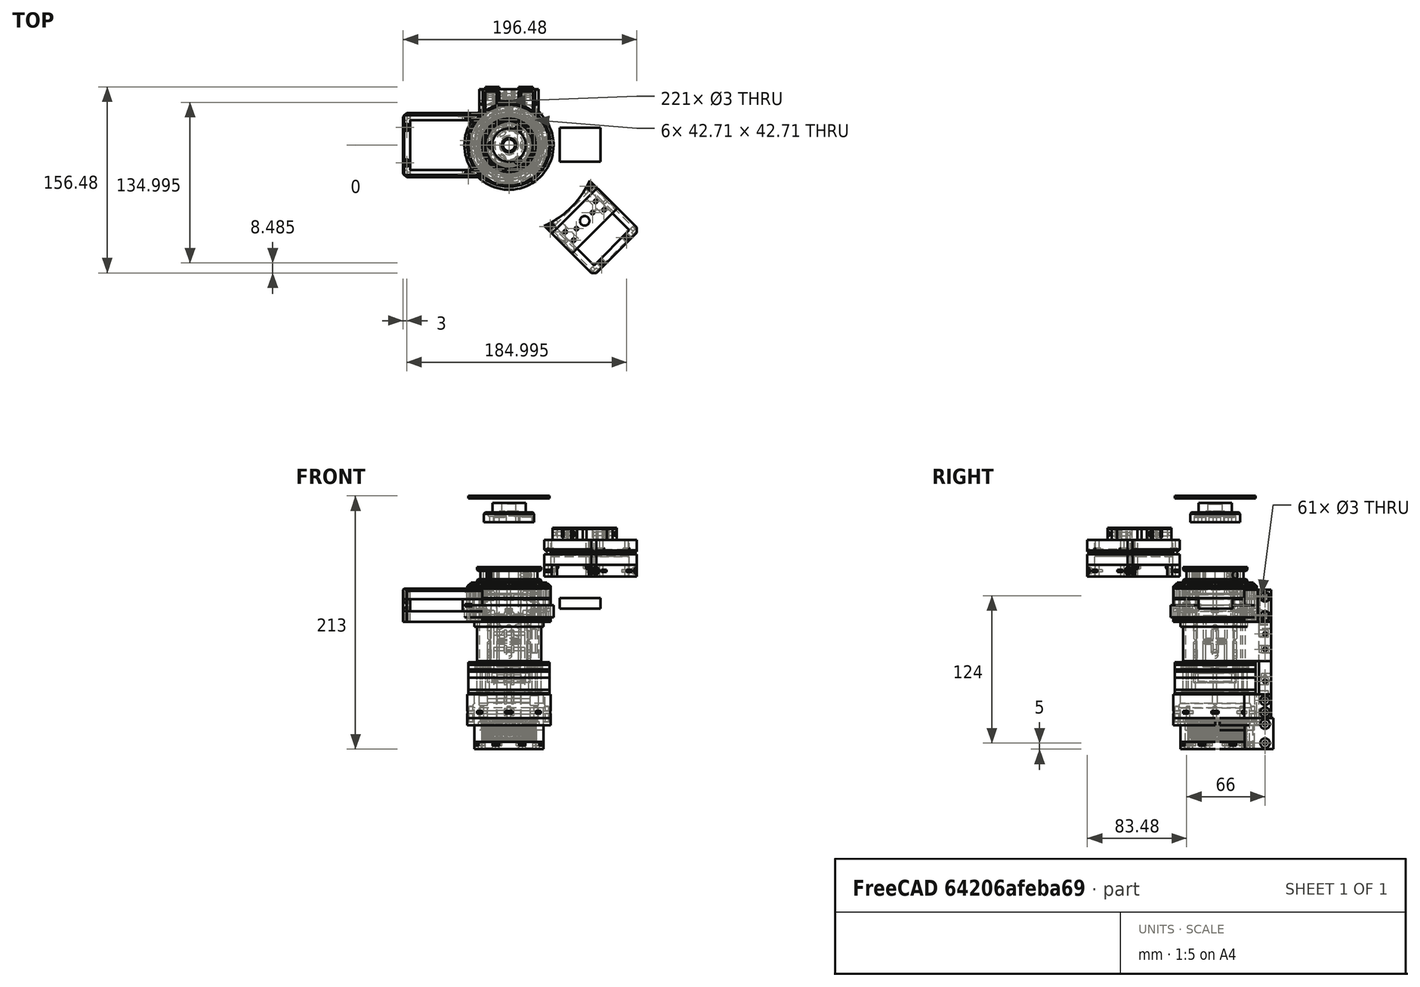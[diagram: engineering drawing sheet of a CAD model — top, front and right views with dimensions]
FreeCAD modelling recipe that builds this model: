
FCSTD DOCUMENT  (FreeCAD 0.19R24276 (Git))
Label: G-midi_rotators_066
License: All rights reserved
LicenseURL: http://en.wikipedia.org/wiki/All_rights_reserved
objects: Part::Cylinder×403, Part::Box×196, Part::Cut×177, Part::Compound×164, Part::FeaturePython×42, Part::Chamfer×41, Mesh::Feature×25, Part::Torus×3
note: 1026 computed .brp shape members not serialized (recipe doc carries the construction recipe); baked Part::Feature solids carry a one-line shape summary decoded from their .brp

FEATURE [Part::Box] Box313  label="Krychle313"
  AttacherType = Attacher::AttachEngine3D
  Height = 7
  Length = 1.4
  Placement = pos=(0,0,-22) rot=(0,0,1;0.099484rad)
  Width = 60
FEATURE [Part::Box] Box314  label="Krychle314"
  AttacherType = Attacher::AttachEngine3D
  Height = 7
  Length = 1.4
  Placement = pos=(0,0,-22) rot=(0,0,-1;0.05236rad)
  Width = 60
FEATURE [Part::FeaturePython] Tube084  # WARN: FeaturePython — macro-defined, semantics opaque (R4)
  AttacherType = Attacher::AttachEngine3D
  Height = 7
  InnerRadius = 20
  OuterRadius = 21.4
  Placement = pos=(0,0,-22) rot=(0,0,1;0rad)
FEATURE [Part::FeaturePython] Tube085  # WARN: FeaturePython — macro-defined, semantics opaque (R4)
  AttacherType = Attacher::AttachEngine3D
  Height = 7
  InnerRadius = 20
  OuterRadius = 21.4
  Placement = pos=(0,0,-22) rot=(0,0,1;0rad)
FEATURE [Part::Box] Box307  label="Krychle307"
  AttacherType = Attacher::AttachEngine3D
  Height = 7
  Length = 60
  Placement = pos=(0,0,-22) rot=(0,0,-1;0.349066rad)
  Width = 60
FEATURE [Part::Box] Box308  label="Krychle308"
  AttacherType = Attacher::AttachEngine3D
  Height = 7
  Length = 60
  Placement = pos=(-56.3816,-20.5212,-22) rot=(0,0,1;0.349066rad)
  Width = 60
FEATURE [Part::Compound] Compound718
  Links = -> [Box307,Box308]
FEATURE [Part::Box] Box309  label="Krychle309"
  AttacherType = Attacher::AttachEngine3D
  Height = 7
  Length = 120
  Placement = pos=(-60,-60,-22) rot=(0,0,-1;0rad)
  Width = 60
FEATURE [Part::Cut] Cut334
  Base = -> Tube085
  Tool = -> Box309
FEATURE [Part::Box] Box310  label="Krychle310"
  AttacherType = Attacher::AttachEngine3D
  Height = 7
  Length = 120
  Placement = pos=(-60,-60,-22) rot=(0,0,-1;0rad)
  Width = 60
FEATURE [Part::Cut] Cut337
  Base = -> Tube084
  Tool = -> Box310
FEATURE [Part::Box] Box311  label="Krychle311"
  AttacherType = Attacher::AttachEngine3D
  Height = 7
  Length = 60
  Placement = pos=(-59.9909,-1.04714,-22) rot=(0,0,1;0.017453rad)
  Width = 60
FEATURE [Part::Box] Box312  label="Krychle312"
  AttacherType = Attacher::AttachEngine3D
  Height = 7
  Length = 60
  Placement = pos=(0,0,-22) rot=(0,0,-1;0.034907rad)
  Width = 60
FEATURE [Part::Compound] Compound719
  Links = -> [Box312,Box311]
FEATURE [Part::Cylinder] Cylinder805  label="Válec805"
  Angle = 360
  AttacherType = Attacher::AttachEngine3D
  Height = 3
  Placement = pos=(0,0,-25) rot=(0,0,1;0rad)
  Radius = 27
FEATURE [Part::Chamfer] Chamfer
  Base = -> Cylinder805
  Edges = 1 edges r=1: [Edge1]
FEATURE [Part::Box] Box315  label="Krychle315"
  AttacherType = Attacher::AttachEngine3D
  Height = 100
  Length = 30.2
  Placement = pos=(0,-21.3546,-30) rot=(0,0,1;0.785398rad)
  Width = 30.2
FEATURE [Part::Cut] Cut340
  Base = -> Chamfer
  Tool = -> Box315
FEATURE [Part::Cylinder] Cylinder806  label="Válec806"
  Angle = 360
  AttacherType = Attacher::AttachEngine3D
  Height = 3
  Placement = pos=(0,0,-15) rot=(0,0,1;0rad)
  Radius = 27
FEATURE [Part::Box] Box316  label="Krychle316"
  AttacherType = Attacher::AttachEngine3D
  Height = 100
  Length = 30.2
  Placement = pos=(0,-21.3546,-30) rot=(0,0,1;0.785398rad)
  Width = 30.2
FEATURE [Part::Cut] Cut341
  Base = -> Cylinder806
  Tool = -> Box316
FEATURE [Part::Chamfer] Chamfer001
  Base = -> Cut341
  Edges = 1 edges r=1: [Edge3]
FEATURE [Part::Box] Box317  label="Krychle317"
  AttacherType = Attacher::AttachEngine3D
  Height = 20
  Length = 6
  Placement = pos=(18,-3,-30) rot=(0,0,1;0rad)
  Width = 6
FEATURE [Part::Cylinder] Cylinder807  label="Válec807"
  Angle = 360
  AttacherType = Attacher::AttachEngine3D
  Height = 20
  Placement = pos=(21,0,-30) rot=(0,0,1;0rad)
  Radius = 1.5
FEATURE [Part::Box] Box318  label="Krychle318"
  AttacherType = Attacher::AttachEngine3D
  Height = 20
  Length = 6
  Placement = pos=(9.89949,-14.1421,-30) rot=(0,0,-1;0.785398rad)
  Width = 6
FEATURE [Part::Cylinder] Cylinder808  label="Válec808"
  Angle = 360
  AttacherType = Attacher::AttachEngine3D
  Height = 20
  Placement = pos=(14.1421,-14.1421,-30) rot=(0,0,-1;0.785398rad)
  Radius = 1.5
FEATURE [Part::Box] Box319  label="Krychle319"
  AttacherType = Attacher::AttachEngine3D
  Height = 20
  Length = 6
  Placement = pos=(-9.89949,14.1421,-30) rot=(0,0,1;2.35619rad)
  Width = 6
FEATURE [Part::Cylinder] Cylinder809  label="Válec809"
  Angle = 360
  AttacherType = Attacher::AttachEngine3D
  Height = 20
  Placement = pos=(-14.1421,14.1421,-30) rot=(0,0,1;2.35619rad)
  Radius = 1.5
FEATURE [Part::Compound] Compound
  Links = -> [Cylinder808,Cylinder809]
FEATURE [Part::Cut] Cut342
  Base = -> Cut340
  Tool = -> Compound
FEATURE [Part::Compound] Compound722
  Links = -> [Box319,Box318]
  Placement = pos=(0,0,-13) rot=(0,0,1;0rad)
FEATURE [Part::Cut] Cut344
  Base = -> Cut342
  Tool = -> Compound722
FEATURE [Part::Cylinder] Cylinder812  label="Válec812"
  Angle = 360
  AttacherType = Attacher::AttachEngine3D
  Height = 3
  Placement = pos=(-14.1421,14.1421,-30) rot=(0,0,1;2.35619rad)
  Radius = 3
FEATURE [Part::Cylinder] Cylinder813  label="Válec813"
  Angle = 360
  AttacherType = Attacher::AttachEngine3D
  Height = 3
  Placement = pos=(14.1421,-14.1421,-30) rot=(0,0,-1;0.785398rad)
  Radius = 3
FEATURE [Part::Compound] Compound723
  Links = -> [Cylinder813,Cylinder812]
  Placement = pos=(0,0,17) rot=(0,0,1;0rad)
FEATURE [Part::Cut] Cut345
  Base = -> Chamfer001
  Tool = -> Compound723
FEATURE [Part::Cylinder] Cylinder814  label="Válec814"
  Angle = 360
  AttacherType = Attacher::AttachEngine3D
  Height = 20
  Placement = pos=(-14.1421,14.1421,-30) rot=(0,0,1;2.35619rad)
  Radius = 1.5
FEATURE [Part::Cylinder] Cylinder815  label="Válec815"
  Angle = 360
  AttacherType = Attacher::AttachEngine3D
  Height = 20
  Placement = pos=(14.1421,-14.1421,-30) rot=(0,0,-1;0.785398rad)
  Radius = 1.5
FEATURE [Part::Compound] Compound724
  Links = -> [Cylinder815,Cylinder814]
FEATURE [Part::Cut] Cut346  label="G-midi_belt-wheel-front"
  Base = -> Cut345
  Placement = pos=(0,0,54) rot=(0,0,1;0rad)
  Tool = -> Compound724
FEATURE [Part::Box] Box320  label="Krychle320"
  AttacherType = Attacher::AttachEngine3D
  Height = 20
  Length = 30.2
  Placement = pos=(-15.1,-15.1,0) rot=(0,0,1;0rad)
  Width = 30.2
FEATURE [Part::Cylinder] Cylinder816  label="Válec816"
  Angle = 360
  AttacherType = Attacher::AttachEngine3D
  Height = 20
  Radius = 24.65
FEATURE [Part::Cut] Cut349
  Base = -> Cylinder816
  Tool = -> Box320
FEATURE [Part::Box] Box001  label="Krychle001"
  AttacherType = Attacher::AttachEngine3D
  Height = 20
  Length = 20
  Placement = pos=(-10,15.1,20) rot=(0,0,1;0rad)
  Width = 3
FEATURE [Part::Box] Box002  label="Krychle002"
  AttacherType = Attacher::AttachEngine3D
  Height = 20
  Length = 20
  Placement = pos=(-15.1,-10,20) rot=(0,0,1;1.5708rad)
  Width = 3
FEATURE [Part::Box] Box003  label="Krychle003"
  AttacherType = Attacher::AttachEngine3D
  Height = 20
  Length = 20
  Placement = pos=(10,-15.1,20) rot=(0,0,1;3.14159rad)
  Width = 3
FEATURE [Part::Box] Box004  label="Krychle004"
  AttacherType = Attacher::AttachEngine3D
  Height = 20
  Length = 20
  Placement = pos=(15.1,10,20) rot=(0,0,-1;1.5708rad)
  Width = 3
FEATURE [Part::Cylinder] Cylinder001  label="Válec001"
  Angle = 360
  AttacherType = Attacher::AttachEngine3D
  Height = 10
  Placement = pos=(0,-12,30) rot=(1,0,0;1.5708rad)
  Radius = 2.5
FEATURE [Part::Cylinder] Cylinder002  label="Válec002"
  Angle = 360
  AttacherType = Attacher::AttachEngine3D
  Height = 10
  Placement = pos=(12,6e-15,30) rot=(0.57735,0.57735,0.57735;2.0944rad)
  Radius = 2.5
FEATURE [Part::Cylinder] Cylinder003  label="Válec003"
  Angle = 360
  AttacherType = Attacher::AttachEngine3D
  Height = 10
  Placement = pos=(-1.5e-14,12,30) rot=(0,0.707107,0.707107;3.14159rad)
  Radius = 2.5
FEATURE [Part::Cylinder] Cylinder004  label="Válec004"
  Angle = 360
  AttacherType = Attacher::AttachEngine3D
  Height = 10
  Placement = pos=(-12,-2.4e-14,30) rot=(-0.57735,0.57735,0.57735;4.18879rad)
  Radius = 2.5
FEATURE [Part::Compound] Compound725
  Links = -> [Box001,Box002,Box003,Box004]
FEATURE [Part::Compound] Compound001
  Links = -> [Cylinder001,Cylinder002,Cylinder003,Cylinder004]
FEATURE [Part::Cut] Cut001
  Base = -> Compound725
  Tool = -> Compound001
FEATURE [Part::Chamfer] Chamfer002
  Base = -> Cut001
  Edges = 5 edges r=2: [Edge3,Edge12,Edge18,Edge27,Edge42]
FEATURE [Part::Chamfer] Chamfer003
  Base = -> Chamfer002
  Edges = 3 edges r=2: [Edge49,Edge63,Edge72]
FEATURE [Part::Chamfer] Chamfer004
  Base = -> Chamfer003
  Edges = 4 edges r=1: [Edge1,Edge29,Edge50,Edge71]
FEATURE [Part::Chamfer] Chamfer006
  Base = -> Cut349
  Edges = 2 edges r=0.5: [Edge9,Edge11]
FEATURE [Part::Chamfer] Chamfer005
  Base = -> Chamfer006
  Edges = 1 edges r=1: [Edge22]
FEATURE [Part::Chamfer] Chamfer007
  Base = -> Chamfer005
  Edges = 1 edges r=0.5: [Edge3]
FEATURE [Part::Compound] Compound002  label="G-midi_rotator-fix1"
  Links = -> [Chamfer004,Chamfer007,Chamfer003]
FEATURE [Part::Box] Box671  label="Krychle671"
  AttacherType = Attacher::AttachEngine3D
  Height = 50
  Length = 42
  Placement = pos=(-21.0011,60.0051,31) rot=(0,0,1;0rad)
  Width = 62
FEATURE [Part::Compound] Compound846
  Links = -> [Box671]
  Placement = pos=(0,0,1) rot=(0,0,1;3.92699rad)
FEATURE [Part::Box] Box672  label="Krychle672"
  AttacherType = Attacher::AttachEngine3D
  Height = 9
  Length = 54
  Placement = pos=(-27.0044,59.998,75) rot=(0,0,1;0rad)
  Width = 68
FEATURE [Part::Cylinder] Cylinder1708  label="Válec1708"
  Angle = 360
  AttacherType = Attacher::AttachEngine3D
  Height = 40
  Placement = pos=(0,0,44) rot=(0,0,1;0rad)
  Radius = 74
FEATURE [Part::Box] Box673  label="Krychle673"
  AttacherType = Attacher::AttachEngine3D
  Height = 10
  Length = 54
  Placement = pos=(-27.0044,59.998,75) rot=(0,0,1;0rad)
  Width = 68
FEATURE [Part::Box] Box674  label="Krychle674"
  AttacherType = Attacher::AttachEngine3D
  Height = 10
  Length = 56
  Placement = pos=(-28,78,75) rot=(0,0,1;0rad)
  Width = 44
FEATURE [Part::Compound] Compound847
  Links = -> [Box672]
  Placement = pos=(0,0,0) rot=(0,0,1;3.92699rad)
FEATURE [Part::Cut] Cut489
  Base = -> Compound847
  Tool = -> Compound846
FEATURE [Part::Cut] Cut490
  Base = -> Cut489
  Tool = -> Cylinder1708
FEATURE [Part::Compound] Compound848
  Links = -> [Box673]
  Placement = pos=(0,0,-10) rot=(0,0,1;3.92699rad)
FEATURE [Part::Compound] Compound849
  Links = -> [Box674]
  Placement = pos=(0,0,-10) rot=(0,0,1;3.92699rad)
FEATURE [Part::Cut] Cut491
  Base = -> Compound848
  Tool = -> Compound849
FEATURE [Part::Chamfer] Chamfer053
  Base = -> Cut490
  Edges = 2 edges r=3: [Edge2,Edge9]
FEATURE [Part::Box] Box675  label="Krychle675"
  AttacherType = Attacher::AttachEngine3D
  Height = 50
  Length = 42
  Placement = pos=(-21.0011,60.0051,31) rot=(0,0,1;0rad)
  Width = 62
FEATURE [Part::Compound] Compound850
  Links = -> [Box675]
  Placement = pos=(0,0,0) rot=(0,0,1;3.92699rad)
FEATURE [Part::Cut] Cut492
  Base = -> Cut491
  Tool = -> Compound850
FEATURE [Part::Cylinder] Cylinder1709  label="Válec1709"
  Angle = 360
  AttacherType = Attacher::AttachEngine3D
  Height = 40
  Placement = pos=(0,0,44) rot=(0,0,1;0rad)
  Radius = 74
FEATURE [Part::Cut] Cut493
  Base = -> Cut492
  Tool = -> Cylinder1709
FEATURE [Part::Chamfer] Chamfer052
  Base = -> Cut493
  Edges = 2 edges r=3: [Edge26,Edge37]
FEATURE [Part::Cylinder] Cylinder1710  label="Válec1710"
  Angle = 360
  AttacherType = Attacher::AttachEngine3D
  Height = 50
  Placement = pos=(-24,140,72) rot=(1,0,0;1.5708rad)
  Radius = 1.5
FEATURE [Part::Compound] Compound851
  Links = -> [Cylinder1710]
  Placement = pos=(0,0,0) rot=(0,0,1;3.92699rad)
FEATURE [Part::Cylinder] Cylinder1711  label="Válec1711"
  Angle = 360
  AttacherType = Attacher::AttachEngine3D
  Height = 50
  Placement = pos=(24,140,72) rot=(1,0,0;1.5708rad)
  Radius = 1.5
FEATURE [Part::Compound] Compound852
  Links = -> [Cylinder1711]
  Placement = pos=(0,0,0) rot=(0,0,1;3.92699rad)
FEATURE [Part::Compound] Compound853
  Links = -> [Compound851,Compound852]
  Placement = pos=(0,0,-2) rot=(0,0,1;0rad)
FEATURE [Part::Cylinder] Cylinder1712  label="Válec1712"
  Angle = 360
  AttacherType = Attacher::AttachEngine3D
  Height = 3
  Placement = pos=(-24,128,72) rot=(1,0,0;1.5708rad)
  Radius = 3
FEATURE [Part::Compound] Compound854
  Links = -> [Cylinder1712]
  Placement = pos=(0,0,0) rot=(0,0,1;3.92699rad)
FEATURE [Part::Cylinder] Cylinder1713  label="Válec1713"
  Angle = 360
  AttacherType = Attacher::AttachEngine3D
  Height = 3
  Placement = pos=(24,128,72) rot=(1,0,0;1.5708rad)
  Radius = 3
FEATURE [Part::Compound] Compound855
  Links = -> [Cylinder1713]
  Placement = pos=(0,0,0) rot=(0,0,1;3.92699rad)
FEATURE [Part::Compound] Compound856
  Links = -> [Compound854,Compound855]
  Placement = pos=(0,0,-2) rot=(0,0,1;0rad)
FEATURE [Part::Box] Box680  label="Krychle680"
  AttacherType = Attacher::AttachEngine3D
  Height = 2
  Length = 6
  Placement = pos=(21,70,-48) rot=(0,0,1;0rad)
  Width = 6
FEATURE [Part::Box] Box681  label="Krychle681"
  AttacherType = Attacher::AttachEngine3D
  Height = 2
  Length = 7
  Placement = pos=(-28,70,-48) rot=(0,0,1;0rad)
  Width = 6
FEATURE [Part::Box] Box682  label="Krychle682"
  AttacherType = Attacher::AttachEngine3D
  Height = 2
  Length = 6
  Placement = pos=(-18,122,-48) rot=(0,0,1;0rad)
  Width = 6
FEATURE [Part::Box] Box683  label="Krychle683"
  AttacherType = Attacher::AttachEngine3D
  Height = 2
  Length = 6
  Placement = pos=(12,122,-48) rot=(0,0,1;0rad)
  Width = 6
FEATURE [Part::Cylinder] Cylinder1718  label="Válec1718"
  Angle = 360
  AttacherType = Attacher::AttachEngine3D
  Height = 60
  Placement = pos=(-15,125,-80) rot=(0,0,1;0rad)
  Radius = 1.5
FEATURE [Part::Cylinder] Cylinder1719  label="Válec1719"
  Angle = 360
  AttacherType = Attacher::AttachEngine3D
  Height = 60
  Placement = pos=(15,125,-80) rot=(0,0,1;0rad)
  Radius = 1.5
FEATURE [Part::Cylinder] Cylinder1720  label="Válec1720"
  Angle = 360
  AttacherType = Attacher::AttachEngine3D
  Height = 60
  Placement = pos=(24,73,-80) rot=(0,0,1;0rad)
  Radius = 1.5
FEATURE [Part::Cylinder] Cylinder1721  label="Válec1721"
  Angle = 360
  AttacherType = Attacher::AttachEngine3D
  Height = 60
  Placement = pos=(-24,73,-80) rot=(0,0,1;0rad)
  Radius = 1.5
FEATURE [Part::Cut] Cut494
  Base = -> Chamfer052
  Tool = -> Compound856
FEATURE [Part::Cut] Cut495
  Base = -> Cut494
  Tool = -> Compound853
FEATURE [Part::Compound] Compound859
  Links = -> [Box681,Box682,Box680,Box683]
  Placement = pos=(0,0,117) rot=(0,0,1;3.92699rad)
FEATURE [Part::Cut] Cut496
  Base = -> Cut495
  Tool = -> Compound859
FEATURE [Part::Compound] Compound860
  Links = -> [Cylinder1720,Cylinder1721,Cylinder1718,Cylinder1719]
  Placement = pos=(0,0,100) rot=(0,0,1;3.92699rad)
FEATURE [Part::Cut] Cut497
  Base = -> Cut496
  Tool = -> Compound860
FEATURE [Part::Box] Box685  label="Krychle685"
  AttacherType = Attacher::AttachEngine3D
  Height = 18
  Length = 42
  Placement = pos=(-21,-23,22) rot=(0,0,1;0rad)
  Width = 8
FEATURE [Part::Compound] Compound862
  Links = -> [Box685]
  Placement = pos=(63.64,-63.64,43) rot=(0,0,1;3.92699rad)
FEATURE [Part::Cylinder] Cylinder1724  label="Válec1724"
  Angle = 360
  AttacherType = Attacher::AttachEngine3D
  Height = 40
  Placement = pos=(0,0,44) rot=(0,0,1;0rad)
  Radius = 74
FEATURE [Part::Cylinder] Cylinder1725  label="Válec1725"
  Angle = 360
  AttacherType = Attacher::AttachEngine3D
  Height = 50
  Placement = pos=(-18,100,72) rot=(1,0,0;1.5708rad)
  Radius = 1.5
FEATURE [Part::Cylinder] Cylinder1726  label="Válec1726"
  Angle = 360
  AttacherType = Attacher::AttachEngine3D
  Height = 50
  Placement = pos=(18,100,72) rot=(1,0,0;1.5708rad)
  Radius = 1.5
FEATURE [Part::Cut] Cut498
  Base = -> Compound862
  Tool = -> Cylinder1724
FEATURE [Part::Compound] Compound868
  Links = -> [Cylinder1726]
  Placement = pos=(0,0,0) rot=(0,0,1;3.92699rad)
FEATURE [Part::Compound] Compound869
  Links = -> [Cylinder1725]
  Placement = pos=(0,0,0) rot=(0,0,1;3.92699rad)
FEATURE [Part::Compound] Compound867
  Links = -> [Compound869,Compound868]
  Placement = pos=(0,0,1) rot=(0,0,1;0rad)
FEATURE [Part::Cut] Cut499
  Base = -> Cut498
  Tool = -> Compound867
FEATURE [Part::Compound] Compound870  label="Base_encoder-lowhold"
  Links = -> [Cut497,Chamfer053,Cut499]
  Placement = pos=(0,0,-31) rot=(0,0,1;0rad)
FEATURE [Part::FeaturePython] Tube011  # WARN: FeaturePython — macro-defined, semantics opaque (R4)
  AttacherType = Attacher::AttachEngine3D
  Height = 10
  InnerRadius = 26
  OuterRadius = 32
FEATURE [Part::Cylinder] Cylinder195  label="Válec195"
  Angle = 360
  AttacherType = Attacher::AttachEngine3D
  Height = 30
  Placement = pos=(29,4e-15,0) rot=(0,0,1;1.5708rad)
  Radius = 1.5
FEATURE [Part::Cylinder] Cylinder196  label="Válec196"
  Angle = 360
  AttacherType = Attacher::AttachEngine3D
  Height = 30
  Placement = pos=(0,-29,0) rot=(0,0,1;0rad)
  Radius = 1.5
FEATURE [Part::Cylinder] Cylinder197  label="Válec197"
  Angle = 360
  AttacherType = Attacher::AttachEngine3D
  Height = 30
  Placement = pos=(20.5061,20.5061,0) rot=(0,0,1;2.35619rad)
  Radius = 1.5
FEATURE [Part::FeaturePython] Tube014  # WARN: FeaturePython — macro-defined, semantics opaque (R4)
  AttacherType = Attacher::AttachEngine3D
  Height = 3
  InnerRadius = 23
  OuterRadius = 32
  Placement = pos=(0,0,-3) rot=(0,0,1;0rad)
FEATURE [Part::Cylinder] Cylinder198  label="Válec198"
  Angle = 360
  AttacherType = Attacher::AttachEngine3D
  Height = 30
  Placement = pos=(20.5061,-20.5061,0) rot=(0,0,1;0.785398rad)
  Radius = 1.5
FEATURE [Part::Cylinder] Cylinder199  label="Válec199"
  Angle = 360
  AttacherType = Attacher::AttachEngine3D
  Height = 30
  Placement = pos=(-1.1e-14,29,0) rot=(0,0,1;3.14159rad)
  Radius = 1.5
FEATURE [Part::Cylinder] Cylinder200  label="Válec200"
  Angle = 360
  AttacherType = Attacher::AttachEngine3D
  Height = 30
  Placement = pos=(-20.5061,20.5061,0) rot=(0,0,1;3.92699rad)
  Radius = 1.5
FEATURE [Part::Cylinder] Cylinder201  label="Válec201"
  Angle = 360
  AttacherType = Attacher::AttachEngine3D
  Height = 30
  Placement = pos=(-29,-1.1e-14,0) rot=(0,0,-1;1.5708rad)
  Radius = 1.5
FEATURE [Part::Cylinder] Cylinder202  label="Válec202"
  Angle = 360
  AttacherType = Attacher::AttachEngine3D
  Height = 30
  Placement = pos=(-20.5061,-20.5061,0) rot=(0,0,-1;0.785398rad)
  Radius = 1.5
FEATURE [Part::Compound] Compound545
  Links = -> [Cylinder196,Cylinder198,Cylinder195,Cylinder197,Cylinder199,Cylinder200,Cylinder201,Cylinder202]
FEATURE [Part::Cut] Cut319
  Base = -> Tube011
  Tool = -> Compound545
FEATURE [Part::Box] Box084  label="Krychle084"
  AttacherType = Attacher::AttachEngine3D
  Height = 2
  Length = 6
  Placement = pos=(-3,-32,4) rot=(0,0,1;0rad)
  Width = 6
FEATURE [Part::Box] Box085  label="Krychle085"
  AttacherType = Attacher::AttachEngine3D
  Height = 2
  Length = 6
  Placement = pos=(20.5061,-24.7487,4) rot=(0,0,1;0.785398rad)
  Width = 6
FEATURE [Part::Box] Box086  label="Krychle086"
  AttacherType = Attacher::AttachEngine3D
  Height = 2
  Length = 6
  Placement = pos=(32,-3,4) rot=(0,0,1;1.5708rad)
  Width = 6
FEATURE [Part::Compound] Compound548
  Links = -> [Tube014,Cut319]
FEATURE [Part::Box] Box087  label="Krychle087"
  AttacherType = Attacher::AttachEngine3D
  Height = 2
  Length = 6
  Placement = pos=(24.7487,20.5061,4) rot=(0,0,1;2.35619rad)
  Width = 6
FEATURE [Part::Box] Box088  label="Krychle088"
  AttacherType = Attacher::AttachEngine3D
  Height = 2
  Length = 6
  Placement = pos=(3,32,4) rot=(0,0,1;3.14159rad)
  Width = 6
FEATURE [Part::Box] Box089  label="Krychle089"
  AttacherType = Attacher::AttachEngine3D
  Height = 2
  Length = 6
  Placement = pos=(-20.5061,24.7487,4) rot=(0,0,1;3.92699rad)
  Width = 6
FEATURE [Part::Box] Box090  label="Krychle090"
  AttacherType = Attacher::AttachEngine3D
  Height = 2
  Length = 6
  Placement = pos=(-32,3,4) rot=(0,0,-1;1.5708rad)
  Width = 6
FEATURE [Part::Box] Box091  label="Krychle091"
  AttacherType = Attacher::AttachEngine3D
  Height = 2
  Length = 6
  Placement = pos=(-24.7487,-20.5061,4) rot=(0,0,-1;0.785398rad)
  Width = 6
FEATURE [Part::Compound] Compound549
  Links = -> [Box084,Box085,Box086,Box087,Box088,Box089,Box090,Box091]
FEATURE [Part::Cut] Cut321
  Base = -> Compound548
  Tool = -> Compound549
FEATURE [Part::Box] Box093  label="Krychle093"
  AttacherType = Attacher::AttachEngine3D
  Height = 26
  Length = 40
  Placement = pos=(-20,15,-3) rot=(0,0,1;0rad)
  Width = 30
FEATURE [Part::Box] Box094  label="Krychle094"
  AttacherType = Attacher::AttachEngine3D
  Height = 26
  Length = 16
  Placement = pos=(-8,20,-3) rot=(0,0,1;0rad)
  Width = 25
FEATURE [Part::Cut] Cut322
  Base = -> Box093
  Tool = -> Box094
FEATURE [Part::Cylinder] Cylinder211  label="Válec211"
  Angle = 360
  AttacherType = Attacher::AttachEngine3D
  Height = 40
  Placement = pos=(0,0,-8) rot=(0,0,1;0rad)
  Radius = 32
FEATURE [Part::Cut] Cut323
  Base = -> Cut322
  Tool = -> Cylinder211
FEATURE [Part::Cylinder] Cylinder212  label="Válec212"
  Angle = 360
  AttacherType = Attacher::AttachEngine3D
  Height = 20
  Placement = pos=(-32,38,2) rot=(0,1,0;1.5708rad)
  Radius = 4
FEATURE [Part::Cylinder] Cylinder214  label="Válec214"
  Angle = 360
  AttacherType = Attacher::AttachEngine3D
  Height = 20
  Placement = pos=(-24,38,2) rot=(0,1,0;1.5708rad)
  Radius = 1.5
FEATURE [Part::Cylinder] Cylinder216  label="Válec216"
  Angle = 360
  AttacherType = Attacher::AttachEngine3D
  Height = 20
  Placement = pos=(-24,38,18) rot=(0,1,0;1.5708rad)
  Radius = 1.5
FEATURE [Part::Compound] Compound551
  Links = -> [Cylinder214,Cylinder216]
FEATURE [Part::Cut] Cut324
  Base = -> Cut323
  Tool = -> Compound551
FEATURE [Part::Cylinder] Cylinder217  label="Válec217"
  Angle = 360
  AttacherType = Attacher::AttachEngine3D
  Height = 20
  Placement = pos=(-32,38,18) rot=(0,1,0;1.5708rad)
  Radius = 4
FEATURE [Part::Compound] Compound550
  Links = -> [Cylinder217,Cylinder212]
FEATURE [Part::Cut] Cut325
  Base = -> Cut324
  Tool = -> Compound550
FEATURE [Part::Cylinder] Cylinder218  label="Válec218"
  Angle = 360
  AttacherType = Attacher::AttachEngine3D
  Height = 20
  Placement = pos=(12,38,18) rot=(0,1,0;1.5708rad)
  Radius = 4
FEATURE [Part::Cylinder] Cylinder219  label="Válec219"
  Angle = 360
  AttacherType = Attacher::AttachEngine3D
  Height = 20
  Placement = pos=(12,38,2) rot=(0,1,0;1.5708rad)
  Radius = 4
FEATURE [Part::Cylinder] Cylinder220  label="Válec220"
  Angle = 360
  AttacherType = Attacher::AttachEngine3D
  Height = 20
  Placement = pos=(4,38,2) rot=(0,1,0;1.5708rad)
  Radius = 1.5
FEATURE [Part::Cylinder] Cylinder221  label="Válec221"
  Angle = 360
  AttacherType = Attacher::AttachEngine3D
  Height = 20
  Placement = pos=(4,38,18) rot=(0,1,0;1.5708rad)
  Radius = 1.5
FEATURE [Part::Compound] Compound552
  Links = -> [Cylinder218,Cylinder219]
FEATURE [Part::Cut] Cut326
  Base = -> Cut325
  Tool = -> Compound552
FEATURE [Part::Compound] Compound553
  Links = -> [Cylinder220,Cylinder221]
FEATURE [Part::Cut] Cut327
  Base = -> Cut326
  Tool = -> Compound553
FEATURE [Part::Compound] Compound572  label="adapto_midi_lozohold"
  Links = -> [Cut327,Cut321]
FEATURE [Part::Box] Box686  label="Krychle686"
  AttacherType = Attacher::AttachEngine3D
  Height = 10
  Length = 54
  Placement = pos=(-27.0044,59.998,75) rot=(0,0,1;0rad)
  Width = 68
FEATURE [Part::Box] Box688  label="Krychle688"
  AttacherType = Attacher::AttachEngine3D
  Height = 50
  Length = 42
  Placement = pos=(-21,58,38) rot=(0,0,1;0rad)
  Width = 64
FEATURE [Part::Cut] Cut500
  Base = -> Box686
  Tool = -> Box688
FEATURE [Part::Cylinder] Cylinder1727  label="Válec1727"
  Angle = 360
  AttacherType = Attacher::AttachEngine3D
  Height = 3
  Placement = pos=(-24,128,72) rot=(1,0,0;1.5708rad)
  Radius = 3
FEATURE [Part::Cylinder] Cylinder1728  label="Válec1728"
  Angle = 360
  AttacherType = Attacher::AttachEngine3D
  Height = 3
  Placement = pos=(24,128,72) rot=(1,0,0;1.5708rad)
  Radius = 3
FEATURE [Part::Compound] Compound871
  Links = -> [Cylinder1727,Cylinder1728]
  Placement = pos=(0,0,8) rot=(0,0,1;0rad)
FEATURE [Part::Box] Box689  label="Krychle689"
  AttacherType = Attacher::AttachEngine3D
  Height = 2
  Length = 7
  Placement = pos=(-28,70,-48) rot=(0,0,1;0rad)
  Width = 6
FEATURE [Part::Box] Box690  label="Krychle690"
  AttacherType = Attacher::AttachEngine3D
  Height = 2
  Length = 6
  Placement = pos=(-18,122,-48) rot=(0,0,1;0rad)
  Width = 6
FEATURE [Part::Box] Box691  label="Krychle691"
  AttacherType = Attacher::AttachEngine3D
  Height = 2
  Length = 6
  Placement = pos=(21,70,-48) rot=(0,0,1;0rad)
  Width = 6
FEATURE [Part::Box] Box692  label="Krychle692"
  AttacherType = Attacher::AttachEngine3D
  Height = 2
  Length = 6
  Placement = pos=(12,122,-48) rot=(0,0,1;0rad)
  Width = 6
FEATURE [Part::Compound] Compound872
  Links = -> [Box689,Box690,Box691,Box692]
  Placement = pos=(0,0,127) rot=(0,0,1;0rad)
FEATURE [Part::Cylinder] Cylinder1729  label="Válec1729"
  Angle = 360
  AttacherType = Attacher::AttachEngine3D
  Height = 50
  Placement = pos=(-24,140,72) rot=(1,0,0;1.5708rad)
  Radius = 1.5
FEATURE [Part::Cylinder] Cylinder1730  label="Válec1730"
  Angle = 360
  AttacherType = Attacher::AttachEngine3D
  Height = 50
  Placement = pos=(24,140,72) rot=(1,0,0;1.5708rad)
  Radius = 1.5
FEATURE [Part::Compound] Compound873
  Links = -> [Cylinder1729,Cylinder1730]
  Placement = pos=(0,0,8) rot=(0,0,1;0rad)
FEATURE [Part::Cylinder] Cylinder1731  label="Válec1731"
  Angle = 360
  AttacherType = Attacher::AttachEngine3D
  Height = 60
  Placement = pos=(24,73,-80) rot=(0,0,1;0rad)
  Radius = 1.5
FEATURE [Part::Cylinder] Cylinder1732  label="Válec1732"
  Angle = 360
  AttacherType = Attacher::AttachEngine3D
  Height = 60
  Placement = pos=(-24,73,-80) rot=(0,0,1;0rad)
  Radius = 1.5
FEATURE [Part::Cylinder] Cylinder1733  label="Válec1733"
  Angle = 360
  AttacherType = Attacher::AttachEngine3D
  Height = 60
  Placement = pos=(-15,125,-80) rot=(0,0,1;0rad)
  Radius = 1.5
FEATURE [Part::Cylinder] Cylinder1734  label="Válec1734"
  Angle = 360
  AttacherType = Attacher::AttachEngine3D
  Height = 60
  Placement = pos=(15,125,-80) rot=(0,0,1;0rad)
  Radius = 1.5
FEATURE [Part::Compound] Compound874
  Links = -> [Cylinder1731,Cylinder1732,Cylinder1733,Cylinder1734]
  Placement = pos=(0,0,120) rot=(0,0,1;0rad)
FEATURE [Part::Box] Box693  label="Krychle693"
  AttacherType = Attacher::AttachEngine3D
  Height = 10
  Length = 56
  Placement = pos=(-28,78,75) rot=(0,0,1;0rad)
  Width = 44
FEATURE [Part::Cut] Cut501
  Base = -> Cut500
  Tool = -> Box693
FEATURE [Part::Box] Box694  label="Krychle694"
  AttacherType = Attacher::AttachEngine3D
  Height = 9
  Length = 54
  Placement = pos=(-27.0044,59.998,75) rot=(0,0,1;0rad)
  Width = 68
FEATURE [Part::Box] Box695  label="Krychle695"
  AttacherType = Attacher::AttachEngine3D
  Height = 50
  Length = 42
  Placement = pos=(-21,58,40) rot=(0,0,1;0rad)
  Width = 64
FEATURE [Part::Cut] Cut502
  Base = -> Box694
  Placement = pos=(0,0,-9) rot=(0,0,1;0rad)
  Tool = -> Box695
FEATURE [Part::Cylinder] Cylinder1735  label="Válec1735"
  Angle = 360
  AttacherType = Attacher::AttachEngine3D
  Height = 60
  Placement = pos=(15,125,-80) rot=(0,0,1;0rad)
  Radius = 1.5
FEATURE [Part::Cylinder] Cylinder1736  label="Válec1736"
  Angle = 360
  AttacherType = Attacher::AttachEngine3D
  Height = 60
  Placement = pos=(24,73,-80) rot=(0,0,1;0rad)
  Radius = 1.5
FEATURE [Part::Cylinder] Cylinder1737  label="Válec1737"
  Angle = 360
  AttacherType = Attacher::AttachEngine3D
  Height = 60
  Placement = pos=(-24,73,-80) rot=(0,0,1;0rad)
  Radius = 1.5
FEATURE [Part::Cylinder] Cylinder1738  label="Válec1738"
  Angle = 360
  AttacherType = Attacher::AttachEngine3D
  Height = 60
  Placement = pos=(-15,125,-80) rot=(0,0,1;0rad)
  Radius = 1.5
FEATURE [Part::Compound] Compound875
  Links = -> [Cylinder1736,Cylinder1737,Cylinder1738,Cylinder1735]
  Placement = pos=(0,0,120) rot=(0,0,1;0rad)
FEATURE [Part::Cut] Cut503
  Base = -> Cut501
  Tool = -> Compound875
FEATURE [Part::Cut] Cut504
  Base = -> Cut503
  Tool = -> Compound872
FEATURE [Part::Chamfer] Chamfer054
  Base = -> Cut504
  Edges = 2 edges r=3: [Edge32,Edge43]
FEATURE [Part::Cut] Cut505
  Base = -> Chamfer054
  Tool = -> Compound871
FEATURE [Part::Cut] Cut506
  Base = -> Cut505
  Tool = -> Compound873
FEATURE [Part::Chamfer] Chamfer055
  Base = -> Cut502
  Edges = 2 edges r=3: [Edge3,Edge15]
FEATURE [Part::Cut] Cut507
  Base = -> Chamfer055
  Tool = -> Compound874
FEATURE [Part::Compound] Compound876
  Links = -> [Cut506,Cut507]
  Placement = pos=(-39,0,-69) rot=(0,0,-1;1.5708rad)
FEATURE [Part::Cylinder] Cylinder1739  label="Válec1739"
  Angle = 360
  AttacherType = Attacher::AttachEngine3D
  Height = 19
  Placement = pos=(0,0,-3) rot=(0,0,1;0rad)
  Radius = 35
FEATURE [Part::FeaturePython] Tube086  # WARN: FeaturePython — macro-defined, semantics opaque (R4)
  AttacherType = Attacher::AttachEngine3D
  Height = 16
  InnerRadius = 29.1
  OuterRadius = 35
FEATURE [Part::FeaturePython] Tube087  # WARN: FeaturePython — macro-defined, semantics opaque (R4)
  AttacherType = Attacher::AttachEngine3D
  Height = 10
  InnerRadius = 31.5
  OuterRadius = 37.5
FEATURE [Part::FeaturePython] Tube088  # WARN: FeaturePython — macro-defined, semantics opaque (R4)
  AttacherType = Attacher::AttachEngine3D
  Height = 3
  InnerRadius = 26
  OuterRadius = 35
  Placement = pos=(0,0,-3) rot=(0,0,1;0rad)
FEATURE [Part::Cylinder] Cylinder1740  label="Válec1740"
  Angle = 360
  AttacherType = Attacher::AttachEngine3D
  Height = 30
  Placement = pos=(0,-32,0) rot=(0,0,1;0rad)
  Radius = 1.5
FEATURE [Part::Box] Box696  label="Krychle696"
  AttacherType = Attacher::AttachEngine3D
  Height = 2
  Length = 6
  Placement = pos=(-3,-35,6) rot=(0,0,1;0rad)
  Width = 6
FEATURE [Part::Cylinder] Cylinder1741  label="Válec1741"
  Angle = 360
  AttacherType = Attacher::AttachEngine3D
  Height = 30
  Placement = pos=(22.6274,-22.6274,0) rot=(0,0,1;0.785398rad)
  Radius = 1.5
FEATURE [Part::Cylinder] Cylinder1742  label="Válec1742"
  Angle = 360
  AttacherType = Attacher::AttachEngine3D
  Height = 30
  Placement = pos=(32,0,0) rot=(0,0,1;1.5708rad)
  Radius = 1.5
FEATURE [Part::Cylinder] Cylinder1743  label="Válec1743"
  Angle = 360
  AttacherType = Attacher::AttachEngine3D
  Height = 30
  Placement = pos=(22.6274,22.6274,0) rot=(0,0,1;2.35619rad)
  Radius = 1.5
FEATURE [Part::Cylinder] Cylinder1744  label="Válec1744"
  Angle = 360
  AttacherType = Attacher::AttachEngine3D
  Height = 30
  Placement = pos=(-1e-14,32,0) rot=(0,0,1;3.14159rad)
  Radius = 1.5
FEATURE [Part::Cylinder] Cylinder1745  label="Válec1745"
  Angle = 360
  AttacherType = Attacher::AttachEngine3D
  Height = 30
  Placement = pos=(-22.6274,22.6274,0) rot=(0,0,1;3.92699rad)
  Radius = 1.5
FEATURE [Part::Cylinder] Cylinder1746  label="Válec1746"
  Angle = 360
  AttacherType = Attacher::AttachEngine3D
  Height = 30
  Placement = pos=(-32,-1.1e-14,0) rot=(0,0,-1;1.5708rad)
  Radius = 1.5
FEATURE [Part::Cylinder] Cylinder1747  label="Válec1747"
  Angle = 360
  AttacherType = Attacher::AttachEngine3D
  Height = 30
  Placement = pos=(-22.6274,-22.6274,0) rot=(0,0,-1;0.785398rad)
  Radius = 1.5
FEATURE [Part::Compound] Compound877
  Links = -> [Cylinder1740,Cylinder1741,Cylinder1742,Cylinder1743,Cylinder1744,Cylinder1745,Cylinder1746,Cylinder1747]
FEATURE [Part::Box] Box697  label="Krychle697"
  AttacherType = Attacher::AttachEngine3D
  Height = 2
  Length = 6
  Placement = pos=(22.6274,-26.8701,6) rot=(0,0,1;0.785398rad)
  Width = 6
FEATURE [Part::Box] Box698  label="Krychle698"
  AttacherType = Attacher::AttachEngine3D
  Height = 2
  Length = 6
  Placement = pos=(35,-3,6) rot=(0,0,1;1.5708rad)
  Width = 6
FEATURE [Part::Box] Box699  label="Krychle699"
  AttacherType = Attacher::AttachEngine3D
  Height = 2
  Length = 6
  Placement = pos=(26.8701,22.6274,6) rot=(0,0,1;2.35619rad)
  Width = 6
FEATURE [Part::Box] Box700  label="Krychle700"
  AttacherType = Attacher::AttachEngine3D
  Height = 2
  Length = 6
  Placement = pos=(3,35,6) rot=(0,0,1;3.14159rad)
  Width = 6
FEATURE [Part::Box] Box701  label="Krychle701"
  AttacherType = Attacher::AttachEngine3D
  Height = 2
  Length = 6
  Placement = pos=(-22.6274,26.8701,6) rot=(0,0,1;3.92699rad)
  Width = 6
FEATURE [Part::Box] Box702  label="Krychle702"
  AttacherType = Attacher::AttachEngine3D
  Height = 2
  Length = 6
  Placement = pos=(-35,3,6) rot=(0,0,-1;1.5708rad)
  Width = 6
FEATURE [Part::Box] Box703  label="Krychle703"
  AttacherType = Attacher::AttachEngine3D
  Height = 2
  Length = 6
  Placement = pos=(-26.8701,-22.6274,6) rot=(0,0,-1;0.785398rad)
  Width = 6
FEATURE [Part::Compound] Compound878
  Links = -> [Box696,Box697,Box703,Box702,Box701,Box700,Box699,Box698]
FEATURE [Part::FeaturePython] Tube013  # WARN: FeaturePython — macro-defined, semantics opaque (R4)
  AttacherType = Attacher::AttachEngine3D
  Height = 3
  InnerRadius = 23
  OuterRadius = 32
  Placement = pos=(0,0,20) rot=(0,0,1;0rad)
FEATURE [Part::FeaturePython] Tube012  # WARN: FeaturePython — macro-defined, semantics opaque (R4)
  AttacherType = Attacher::AttachEngine3D
  Height = 10
  InnerRadius = 26
  OuterRadius = 32
  Placement = pos=(0,0,10) rot=(0,0,1;0rad)
FEATURE [Part::Cylinder] Cylinder204  label="Válec204"
  Angle = 360
  AttacherType = Attacher::AttachEngine3D
  Height = 3
  Placement = pos=(0,-29,20) rot=(0,0,1;0rad)
  Radius = 3
FEATURE [Part::Cylinder] Cylinder189  label="Válec189"
  Angle = 360
  AttacherType = Attacher::AttachEngine3D
  Height = 30
  Placement = pos=(29,4e-15,0) rot=(0,0,1;1.5708rad)
  Radius = 1.5
FEATURE [Part::Cylinder] Cylinder187  label="Válec187"
  Angle = 360
  AttacherType = Attacher::AttachEngine3D
  Height = 30
  Placement = pos=(0,-29,0) rot=(0,0,1;0rad)
  Radius = 1.5
FEATURE [Part::Cylinder] Cylinder193  label="Válec193"
  Angle = 360
  AttacherType = Attacher::AttachEngine3D
  Height = 30
  Placement = pos=(-29,-1.1e-14,0) rot=(0,0,-1;1.5708rad)
  Radius = 1.5
FEATURE [Part::Cylinder] Cylinder188  label="Válec188"
  Angle = 360
  AttacherType = Attacher::AttachEngine3D
  Height = 30
  Placement = pos=(20.5061,-20.5061,0) rot=(0,0,1;0.785398rad)
  Radius = 1.5
FEATURE [Part::Cylinder] Cylinder191  label="Válec191"
  Angle = 360
  AttacherType = Attacher::AttachEngine3D
  Height = 30
  Placement = pos=(-1.1e-14,29,0) rot=(0,0,1;3.14159rad)
  Radius = 1.5
FEATURE [Part::Cylinder] Cylinder192  label="Válec192"
  Angle = 360
  AttacherType = Attacher::AttachEngine3D
  Height = 30
  Placement = pos=(-20.5061,20.5061,0) rot=(0,0,1;3.92699rad)
  Radius = 1.5
FEATURE [Part::Cylinder] Cylinder190  label="Válec190"
  Angle = 360
  AttacherType = Attacher::AttachEngine3D
  Height = 30
  Placement = pos=(20.5061,20.5061,0) rot=(0,0,1;2.35619rad)
  Radius = 1.5
FEATURE [Part::Cylinder] Cylinder194  label="Válec194"
  Angle = 360
  AttacherType = Attacher::AttachEngine3D
  Height = 30
  Placement = pos=(-20.5061,-20.5061,0) rot=(0,0,-1;0.785398rad)
  Radius = 1.5
FEATURE [Part::Compound] Compound544
  Links = -> [Cylinder187,Cylinder188,Cylinder189,Cylinder190,Cylinder191,Cylinder192,Cylinder193,Cylinder194]
FEATURE [Part::Cut] Cut318
  Base = -> Tube012
  Tool = -> Compound544
FEATURE [Part::Cylinder] Cylinder203  label="Válec203"
  Angle = 360
  AttacherType = Attacher::AttachEngine3D
  Height = 3
  Placement = pos=(29,4e-15,20) rot=(0,0,1;1.5708rad)
  Radius = 3
FEATURE [Part::Cylinder] Cylinder206  label="Válec206"
  Angle = 360
  AttacherType = Attacher::AttachEngine3D
  Height = 3
  Placement = pos=(20.51,-20.51,20) rot=(0,0,1;0.785398rad)
  Radius = 3
FEATURE [Part::Cylinder] Cylinder208  label="Válec208"
  Angle = 360
  AttacherType = Attacher::AttachEngine3D
  Height = 3
  Placement = pos=(-20.51,20.51,20) rot=(0,0,1;3.92699rad)
  Radius = 3
FEATURE [Part::Cylinder] Cylinder205  label="Válec205"
  Angle = 360
  AttacherType = Attacher::AttachEngine3D
  Height = 3
  Placement = pos=(20.51,20.51,20) rot=(0,0,1;2.35619rad)
  Radius = 3
FEATURE [Part::Cylinder] Cylinder210  label="Válec210"
  Angle = 360
  AttacherType = Attacher::AttachEngine3D
  Height = 3
  Placement = pos=(-20.51,-20.51,20) rot=(0,0,-1;0.785398rad)
  Radius = 3
FEATURE [Part::Cylinder] Cylinder209  label="Válec209"
  Angle = 360
  AttacherType = Attacher::AttachEngine3D
  Height = 3
  Placement = pos=(-29,0,20) rot=(0,0,-1;1.5708rad)
  Radius = 3
FEATURE [Part::Cylinder] Cylinder207  label="Válec207"
  Angle = 360
  AttacherType = Attacher::AttachEngine3D
  Height = 3
  Placement = pos=(0,29,20) rot=(0,0,1;3.14159rad)
  Radius = 3
FEATURE [Part::Compound] Compound546
  Links = -> [Cylinder204,Cylinder206,Cylinder203,Cylinder205,Cylinder207,Cylinder208,Cylinder209,Cylinder210]
FEATURE [Part::Cut] Cut320
  Base = -> Tube013
  Tool = -> Compound546
FEATURE [Part::Compound] Compound547  label="adapto_midi_lozofixo"
  Links = -> [Cut318,Cut320]
  Placement = pos=(0,0,6) rot=(0,0,1;0rad)
FEATURE [Part::FeaturePython] Tube089  # WARN: FeaturePython — macro-defined, semantics opaque (R4)
  AttacherType = Attacher::AttachEngine3D
  Height = 9
  InnerRadius = 29.1
  OuterRadius = 35
  Placement = pos=(0,0,16) rot=(0,0,1;0rad)
FEATURE [Part::Cylinder] Cylinder1748  label="Válec1748"
  Angle = 360
  AttacherType = Attacher::AttachEngine3D
  Height = 30
  Placement = pos=(-22.6274,22.6274,0) rot=(0,0,1;3.92699rad)
  Radius = 1.5
FEATURE [Part::Cylinder] Cylinder1749  label="Válec1749"
  Angle = 360
  AttacherType = Attacher::AttachEngine3D
  Height = 30
  Placement = pos=(-22.6274,-22.6274,0) rot=(0,0,-1;0.785398rad)
  Radius = 1.5
FEATURE [Part::Cylinder] Cylinder1750  label="Válec1750"
  Angle = 360
  AttacherType = Attacher::AttachEngine3D
  Height = 30
  Placement = pos=(-1e-14,32,0) rot=(0,0,1;3.14159rad)
  Radius = 1.5
FEATURE [Part::Cylinder] Cylinder1751  label="Válec1751"
  Angle = 360
  AttacherType = Attacher::AttachEngine3D
  Height = 30
  Placement = pos=(-32,-1.1e-14,0) rot=(0,0,-1;1.5708rad)
  Radius = 1.5
FEATURE [Part::Cylinder] Cylinder1752  label="Válec1752"
  Angle = 360
  AttacherType = Attacher::AttachEngine3D
  Height = 30
  Placement = pos=(22.6274,-22.6274,0) rot=(0,0,1;0.785398rad)
  Radius = 1.5
FEATURE [Part::Cylinder] Cylinder1753  label="Válec1753"
  Angle = 360
  AttacherType = Attacher::AttachEngine3D
  Height = 30
  Placement = pos=(32,0,0) rot=(0,0,1;1.5708rad)
  Radius = 1.5
FEATURE [Part::Cylinder] Cylinder1754  label="Válec1754"
  Angle = 360
  AttacherType = Attacher::AttachEngine3D
  Height = 30
  Placement = pos=(22.6274,22.6274,0) rot=(0,0,1;2.35619rad)
  Radius = 1.5
FEATURE [Part::Cylinder] Cylinder1755  label="Válec1755"
  Angle = 360
  AttacherType = Attacher::AttachEngine3D
  Height = 30
  Placement = pos=(0,-32,0) rot=(0,0,1;0rad)
  Radius = 1.5
FEATURE [Part::Compound] Compound879
  Links = -> [Cylinder1755,Cylinder1752,Cylinder1753,Cylinder1754,Cylinder1750,Cylinder1748,Cylinder1751,Cylinder1749]
FEATURE [Part::Cylinder] Cylinder1756  label="Válec1756"
  Angle = 360
  AttacherType = Attacher::AttachEngine3D
  Height = 3
  Placement = pos=(-22.6274,22.6274,0) rot=(0,0,1;3.92699rad)
  Radius = 3
FEATURE [Part::Cylinder] Cylinder1757  label="Válec1757"
  Angle = 360
  AttacherType = Attacher::AttachEngine3D
  Height = 3
  Placement = pos=(-22.6274,-22.6274,0) rot=(0,0,-1;0.785398rad)
  Radius = 3
FEATURE [Part::Cylinder] Cylinder1758  label="Válec1758"
  Angle = 360
  AttacherType = Attacher::AttachEngine3D
  Height = 3
  Placement = pos=(-1e-14,32,0) rot=(0,0,1;3.14159rad)
  Radius = 3
FEATURE [Part::Cylinder] Cylinder1759  label="Válec1759"
  Angle = 360
  AttacherType = Attacher::AttachEngine3D
  Height = 3
  Placement = pos=(-32,-1.1e-14,0) rot=(0,0,-1;1.5708rad)
  Radius = 3
FEATURE [Part::Cylinder] Cylinder1760  label="Válec1760"
  Angle = 360
  AttacherType = Attacher::AttachEngine3D
  Height = 3
  Placement = pos=(22.6274,-22.6274,0) rot=(0,0,1;0.785398rad)
  Radius = 3
FEATURE [Part::Cylinder] Cylinder1761  label="Válec1761"
  Angle = 360
  AttacherType = Attacher::AttachEngine3D
  Height = 3
  Placement = pos=(32,0,0) rot=(0,0,1;1.5708rad)
  Radius = 3
FEATURE [Part::Cylinder] Cylinder1762  label="Válec1762"
  Angle = 360
  AttacherType = Attacher::AttachEngine3D
  Height = 3
  Placement = pos=(22.6274,22.6274,0) rot=(0,0,1;2.35619rad)
  Radius = 3
FEATURE [Part::Cylinder] Cylinder1763  label="Válec1763"
  Angle = 360
  AttacherType = Attacher::AttachEngine3D
  Height = 3
  Placement = pos=(0,-32,0) rot=(0,0,1;0rad)
  Radius = 3
FEATURE [Part::Compound] Compound880
  Links = -> [Cylinder1763,Cylinder1760,Cylinder1761,Cylinder1762,Cylinder1758,Cylinder1756,Cylinder1759,Cylinder1757]
  Placement = pos=(0,0,27) rot=(0,0,1;0rad)
FEATURE [Part::FeaturePython] Tube090  # WARN: FeaturePython — macro-defined, semantics opaque (R4)
  AttacherType = Attacher::AttachEngine3D
  Height = 4
  InnerRadius = 26
  OuterRadius = 35
  Placement = pos=(0,0,25) rot=(0,0,1;0rad)
FEATURE [Part::Cut] Cut508
  Base = -> Tube089
  Tool = -> Compound879
FEATURE [Part::Cylinder] Cylinder1764  label="Válec1764"
  Angle = 360
  AttacherType = Attacher::AttachEngine3D
  Height = 30
  Placement = pos=(22.6274,22.6274,0) rot=(0,0,1;2.35619rad)
  Radius = 1.5
FEATURE [Part::Cylinder] Cylinder1765  label="Válec1765"
  Angle = 360
  AttacherType = Attacher::AttachEngine3D
  Height = 30
  Placement = pos=(-22.6274,22.6274,0) rot=(0,0,1;3.92699rad)
  Radius = 1.5
FEATURE [Part::Cylinder] Cylinder1766  label="Válec1766"
  Angle = 360
  AttacherType = Attacher::AttachEngine3D
  Height = 30
  Placement = pos=(-22.6274,-22.6274,0) rot=(0,0,-1;0.785398rad)
  Radius = 1.5
FEATURE [Part::Cylinder] Cylinder1767  label="Válec1767"
  Angle = 360
  AttacherType = Attacher::AttachEngine3D
  Height = 30
  Placement = pos=(-1e-14,32,0) rot=(0,0,1;3.14159rad)
  Radius = 1.5
FEATURE [Part::Cylinder] Cylinder1768  label="Válec1768"
  Angle = 360
  AttacherType = Attacher::AttachEngine3D
  Height = 30
  Placement = pos=(32,0,0) rot=(0,0,1;1.5708rad)
  Radius = 1.5
FEATURE [Part::Cylinder] Cylinder1769  label="Válec1769"
  Angle = 360
  AttacherType = Attacher::AttachEngine3D
  Height = 30
  Placement = pos=(-32,-1.1e-14,0) rot=(0,0,-1;1.5708rad)
  Radius = 1.5
FEATURE [Part::Cylinder] Cylinder1770  label="Válec1770"
  Angle = 360
  AttacherType = Attacher::AttachEngine3D
  Height = 30
  Placement = pos=(22.6274,-22.6274,0) rot=(0,0,1;0.785398rad)
  Radius = 1.5
FEATURE [Part::Cylinder] Cylinder1771  label="Válec1771"
  Angle = 360
  AttacherType = Attacher::AttachEngine3D
  Height = 30
  Placement = pos=(0,-32,0) rot=(0,0,1;0rad)
  Radius = 1.5
FEATURE [Part::Compound] Compound881
  Links = -> [Cylinder1771,Cylinder1770,Cylinder1768,Cylinder1764,Cylinder1767,Cylinder1765,Cylinder1769,Cylinder1766]
FEATURE [Part::Cut] Cut511
  Base = -> Tube086
  Tool = -> Compound881
FEATURE [Part::Cut] Cut512
  Base = -> Cut511
  Tool = -> Compound878
FEATURE [Part::Box] Box646  label="Krychle646"
  AttacherType = Attacher::AttachEngine3D
  Height = 9
  Length = 28.8
  Placement = pos=(-14.4,-14,34) rot=(0,0,1;0rad)
  Width = 34.4
FEATURE [Part::Box] Box651  label="Krychle651"
  AttacherType = Attacher::AttachEngine3D
  Height = 9
  Length = 42
  Placement = pos=(-21,-12,34) rot=(0,0,1;0rad)
  Width = 24
FEATURE [Part::Box] Box653  label="Krychle653"
  AttacherType = Attacher::AttachEngine3D
  Height = 1
  Length = 54
  Placement = pos=(-27,-12,34) rot=(0,0,1;0rad)
  Width = 24
FEATURE [Part::Cylinder] Cylinder1643  label="Válec1643"
  Angle = 360
  AttacherType = Attacher::AttachEngine3D
  Height = 1
  Placement = pos=(63.64,-63.64,76) rot=(0,0,1;3.92699rad)
  Radius = 4
FEATURE [Part::Compound] Compound804
  Links = -> [Box646]
  Placement = pos=(63.64,-63.64,33) rot=(0,0,1;3.92699rad)
FEATURE [Part::Compound] Compound811
  Links = -> [Box653]
  Placement = pos=(63.64,-63.64,42) rot=(0,0,1;3.92699rad)
FEATURE [Part::Cut] Cut470
  Base = -> Compound811
  Tool = -> Cylinder1643
FEATURE [Part::Box] Box659  label="Krychle659"
  AttacherType = Attacher::AttachEngine3D
  Height = 9
  Length = 42
  Placement = pos=(-21,-14,34) rot=(0,0,1;0rad)
  Width = 28
FEATURE [Part::Box] Box660  label="Krychle660"
  AttacherType = Attacher::AttachEngine3D
  Height = 9
  Length = 54
  Placement = pos=(-27,-12,34) rot=(0,0,1;0rad)
  Width = 24
FEATURE [Part::Compound] Compound824
  Links = -> [Box659]
  Placement = pos=(63.64,-63.64,33) rot=(0,0,1;3.92699rad)
FEATURE [Part::Compound] Compound825
  Links = -> [Box660]
  Placement = pos=(63.64,-63.64,33) rot=(0,0,1;3.92699rad)
FEATURE [Part::Cut] Cut475
  Base = -> Compound825
  Tool = -> Compound824
FEATURE [Part::Cylinder] Cylinder1621  label="Válec1621"
  Angle = 360
  AttacherType = Attacher::AttachEngine3D
  Height = 60
  Placement = pos=(18,95,-57) rot=(0,0,1;0rad)
  Radius = 1.5
FEATURE [Part::Cylinder] Cylinder1676  label="Válec1676"
  Angle = 360
  AttacherType = Attacher::AttachEngine3D
  Height = 60
  Placement = pos=(-18,95,-57) rot=(0,0,1;0rad)
  Radius = 1.5
FEATURE [Part::Cylinder] Cylinder1674  label="Válec1674"
  Angle = 360
  AttacherType = Attacher::AttachEngine3D
  Height = 60
  Placement = pos=(18,85,-57) rot=(0,0,1;0rad)
  Radius = 1.5
FEATURE [Part::Cylinder] Cylinder1675  label="Válec1675"
  Angle = 360
  AttacherType = Attacher::AttachEngine3D
  Height = 60
  Placement = pos=(-18,85,-57) rot=(0,0,1;0rad)
  Radius = 1.5
FEATURE [Part::Compound] Compound806
  Links = -> [Cylinder1621,Cylinder1674,Cylinder1675,Cylinder1676]
  Placement = pos=(0,0,100) rot=(0,0,1;3.92699rad)
FEATURE [Part::Cylinder] Cylinder1670  label="Válec1670"
  Angle = 360
  AttacherType = Attacher::AttachEngine3D
  Height = 20
  Placement = pos=(15.75,114,39.48) rot=(0,0.707107,0.707107;3.14159rad)
  Radius = 1.5
FEATURE [Part::Cylinder] Cylinder1671  label="Válec1671"
  Angle = 360
  AttacherType = Attacher::AttachEngine3D
  Height = 20
  Placement = pos=(15.75,114,58.525) rot=(0,0.707107,0.707107;3.14159rad)
  Radius = 1.5
FEATURE [Part::Compound] Compound826
  Links = -> [Cylinder1670,Cylinder1671]
  Placement = pos=(-49,0,-96) rot=(0.57735,0.57735,0.57735;2.0944rad)
FEATURE [Part::Compound] Compound827
  Links = -> [Compound826]
  Placement = pos=(52.33,-52.33,52) rot=(0,0,1;3.92699rad)
FEATURE [Part::Cut] Cut477
  Base = -> Cut470
  Tool = -> Compound827
FEATURE [Part::Cylinder] Cylinder1683  label="Válec1683"
  Angle = 360
  AttacherType = Attacher::AttachEngine3D
  Height = 60
  Placement = pos=(18,95,-57) rot=(0,0,1;0rad)
  Radius = 1.5
FEATURE [Part::Cylinder] Cylinder1681  label="Válec1681"
  Angle = 360
  AttacherType = Attacher::AttachEngine3D
  Height = 60
  Placement = pos=(-18,85,-57) rot=(0,0,1;0rad)
  Radius = 1.5
FEATURE [Part::Cylinder] Cylinder1684  label="Válec1684"
  Angle = 360
  AttacherType = Attacher::AttachEngine3D
  Height = 60
  Placement = pos=(18,85,-57) rot=(0,0,1;0rad)
  Radius = 1.5
FEATURE [Part::Cylinder] Cylinder1682  label="Válec1682"
  Angle = 360
  AttacherType = Attacher::AttachEngine3D
  Height = 60
  Placement = pos=(-18,95,-57) rot=(0,0,1;0rad)
  Radius = 1.5
FEATURE [Part::Compound] Compound831
  Links = -> [Cylinder1683,Cylinder1684,Cylinder1681,Cylinder1682]
  Placement = pos=(0,0,100) rot=(0,0,1;3.92699rad)
FEATURE [Part::Cut] Cut480
  Base = -> Cut477
  Tool = -> Compound831
FEATURE [Part::Cylinder] Cylinder1772  label="Válec1772"
  Angle = 360
  AttacherType = Attacher::AttachEngine3D
  Height = 100
  Placement = pos=(-24,110,72) rot=(1,0,0;1.5708rad)
  Radius = 1.5
FEATURE [Part::Compound] Compound839
  Links = -> [Cylinder1772]
  Placement = pos=(0,0,0) rot=(0,0,1;3.92699rad)
FEATURE [Part::Cylinder] Cylinder1697  label="Válec1697"
  Angle = 360
  AttacherType = Attacher::AttachEngine3D
  Height = 100
  Placement = pos=(24,110,72) rot=(1,0,0;1.5708rad)
  Radius = 1.5
FEATURE [Part::Compound] Compound840
  Links = -> [Cylinder1697]
  Placement = pos=(0,0,0) rot=(0,0,1;3.92699rad)
FEATURE [Part::Box] Box704  label="Krychle704"
  AttacherType = Attacher::AttachEngine3D
  Height = 6
  Length = 6
  Placement = pos=(21,90,69) rot=(0,0,1;0rad)
  Width = 2
FEATURE [Part::Compound] Compound837
  Links = -> [Box704]
  Placement = pos=(0,0,0) rot=(0,0,1;3.92699rad)
FEATURE [Part::Box] Box665  label="Krychle665"
  AttacherType = Attacher::AttachEngine3D
  Height = 6
  Length = 6
  Placement = pos=(-27,90,69) rot=(0,0,1;0rad)
  Width = 2
FEATURE [Part::Compound] Compound838
  Links = -> [Box665]
  Placement = pos=(0,0,0) rot=(0,0,1;3.92699rad)
FEATURE [Part::Compound] Compound842
  Links = -> [Compound839,Compound840]
FEATURE [Part::Compound] Compound841
  Links = -> [Compound837,Compound838]
FEATURE [Part::Compound] Compound809
  Links = -> [Box651]
  Placement = pos=(63.64,-63.64,33) rot=(0,0,1;3.92699rad)
FEATURE [Part::Cut] Cut469
  Base = -> Compound809
  Tool = -> Compound804
FEATURE [Part::Compound] Compound835
  Links = -> [Cut469,Cut475]
FEATURE [Part::Cut] Cut483
  Base = -> Compound835
  Tool = -> Compound806
FEATURE [Part::Compound] Compound836  label="Base_encoder-sidehold2"
  Links = -> [Cut483,Cut480]
FEATURE [Part::Cut] Cut484
  Base = -> Compound836
  Tool = -> Compound841
FEATURE [Part::Cut] Cut485  label="Base_encoder-sidehold004"
  Base = -> Cut484
  Tool = -> Compound842
FEATURE [Part::Chamfer] Chamfer049
  Base = -> Cut485
  Edges = 4 edges r=1: [Edge48,Edge82,Edge99,Edge114]
FEATURE [Part::Chamfer] Chamfer050
  Base = -> Chamfer049
  Edges = 2 edges r=1: [Edge3,Edge68]
FEATURE [Part::Chamfer] Chamfer051  label="Base_encoder-sidehold"
  Base = -> Chamfer050
  Edges = 2 edges r=1: [Edge69,Edge97]
  Placement = pos=(0,0,-2) rot=(0,0,1;0rad)
FEATURE [Part::Box] Box705  label="Krychle705"
  AttacherType = Attacher::AttachEngine3D
  Height = 9
  Length = 28.8
  Placement = pos=(77,-14,7) rot=(0,0,1;1.5708rad)
  Width = 34.4
FEATURE [Part::Cylinder] Cylinder1773  label="Válec1773"
  Angle = 360
  AttacherType = Attacher::AttachEngine3D
  Height = 3
  Placement = pos=(-15,125,-80) rot=(0,0,1;0rad)
  Radius = 3
FEATURE [Part::Cylinder] Cylinder1774  label="Válec1774"
  Angle = 360
  AttacherType = Attacher::AttachEngine3D
  Height = 60
  Placement = pos=(-15,125,-80) rot=(0,0,1;0rad)
  Radius = 1.5
FEATURE [Part::Cylinder] Cylinder1775  label="Válec1775"
  Angle = 360
  AttacherType = Attacher::AttachEngine3D
  Height = 60
  Placement = pos=(15,125,-80) rot=(0,0,1;0rad)
  Radius = 1.5
FEATURE [Part::Box] Box706  label="Krychle706"
  AttacherType = Attacher::AttachEngine3D
  Height = 50
  Length = 42
  Placement = pos=(-21.0011,60.0051,31) rot=(0,0,1;0rad)
  Width = 62
FEATURE [Part::Compound] Compound883
  Links = -> [Box706]
  Placement = pos=(0,0,0) rot=(0,0,1;3.92699rad)
FEATURE [Part::Cylinder] Cylinder1777  label="Válec1777"
  Angle = 360
  AttacherType = Attacher::AttachEngine3D
  Height = 3
  Placement = pos=(24,73,-80) rot=(0,0,1;0rad)
  Radius = 3
FEATURE [Part::Cylinder] Cylinder1778  label="Válec1778"
  Angle = 360
  AttacherType = Attacher::AttachEngine3D
  Height = 60
  Placement = pos=(-24,73,-80) rot=(0,0,1;0rad)
  Radius = 1.5
FEATURE [Part::Cylinder] Cylinder1779  label="Válec1779"
  Angle = 360
  AttacherType = Attacher::AttachEngine3D
  Height = 40
  Placement = pos=(0,0,44) rot=(0,0,1;0rad)
  Radius = 74
FEATURE [Part::Box] Box708  label="Krychle708"
  AttacherType = Attacher::AttachEngine3D
  Height = 10
  Length = 54
  Placement = pos=(-27.0044,59.998,75) rot=(0,0,1;0rad)
  Width = 68
FEATURE [Part::Compound] Compound884
  Links = -> [Box708]
  Placement = pos=(0,0,-20) rot=(0,0,1;3.92699rad)
FEATURE [Part::Cut] Cut513
  Base = -> Compound884
  Tool = -> Compound883
FEATURE [Part::Cylinder] Cylinder1781  label="Válec1781"
  Angle = 360
  AttacherType = Attacher::AttachEngine3D
  Height = 3
  Placement = pos=(-24,73,-80) rot=(0,0,1;0rad)
  Radius = 3
FEATURE [Part::Cylinder] Cylinder1782  label="Válec1782"
  Angle = 360
  AttacherType = Attacher::AttachEngine3D
  Height = 3
  Placement = pos=(15,125,-80) rot=(0,0,1;0rad)
  Radius = 3
FEATURE [Part::Compound] Compound885
  Links = -> [Cylinder1777,Cylinder1781,Cylinder1773,Cylinder1782]
  Placement = pos=(0,0,135) rot=(0,0,1;3.92699rad)
FEATURE [Part::Cylinder] Cylinder1783  label="Válec1783"
  Angle = 360
  AttacherType = Attacher::AttachEngine3D
  Height = 60
  Placement = pos=(24,73,-80) rot=(0,0,1;0rad)
  Radius = 1.5
FEATURE [Part::Compound] Compound886
  Links = -> [Cylinder1783,Cylinder1778,Cylinder1774,Cylinder1775]
  Placement = pos=(0,0,100) rot=(0,0,1;3.92699rad)
FEATURE [Part::Cut] Cut517
  Base = -> Cut513
  Tool = -> Cylinder1779
FEATURE [Part::Chamfer] Chamfer057
  Base = -> Cut517
  Edges = 2 edges r=3: [Edge2,Edge13]
FEATURE [Part::Chamfer] Chamfer056
  Base = -> Chamfer057
  Edges = 2 edges r=2: [Edge3,Edge22]
FEATURE [Part::Chamfer] Chamfer058
  Base = -> Chamfer056
  Edges = 1 edges r=1: [Edge27]
FEATURE [Part::Cut] Cut516
  Base = -> Chamfer058
  Tool = -> Compound886
FEATURE [Part::Cut] Cut518
  Base = -> Cut516
  Tool = -> Compound885
FEATURE [Part::Box] Box709  label="Krychle709"
  AttacherType = Attacher::AttachEngine3D
  Height = 9
  Length = 54
  Placement = pos=(-27.0044,59.998,75) rot=(0,0,1;0rad)
  Width = 68
FEATURE [Part::Box] Box710  label="Krychle710"
  AttacherType = Attacher::AttachEngine3D
  Height = 50
  Length = 42
  Placement = pos=(-21,58,38) rot=(0,0,1;0rad)
  Width = 64
FEATURE [Part::Cut] Cut519
  Base = -> Box709
  Tool = -> Box710
FEATURE [Part::Cylinder] Cylinder1784  label="Válec1784"
  Angle = 360
  AttacherType = Attacher::AttachEngine3D
  Height = 60
  Placement = pos=(24,73,-80) rot=(0,0,1;0rad)
  Radius = 1.5
FEATURE [Part::Cylinder] Cylinder1785  label="Válec1785"
  Angle = 360
  AttacherType = Attacher::AttachEngine3D
  Height = 60
  Placement = pos=(-24,73,-80) rot=(0,0,1;0rad)
  Radius = 1.5
FEATURE [Part::Cylinder] Cylinder1786  label="Válec1786"
  Angle = 360
  AttacherType = Attacher::AttachEngine3D
  Height = 60
  Placement = pos=(-15,125,-80) rot=(0,0,1;0rad)
  Radius = 1.5
FEATURE [Part::Cylinder] Cylinder1787  label="Válec1787"
  Angle = 360
  AttacherType = Attacher::AttachEngine3D
  Height = 60
  Placement = pos=(15,125,-80) rot=(0,0,1;0rad)
  Radius = 1.5
FEATURE [Part::Compound] Compound887
  Links = -> [Cylinder1784,Cylinder1785,Cylinder1786,Cylinder1787]
  Placement = pos=(0,0,120) rot=(0,0,1;0rad)
FEATURE [Part::Cylinder] Cylinder1788  label="Válec1788"
  Angle = 360
  AttacherType = Attacher::AttachEngine3D
  Height = 3
  Placement = pos=(24,73,-80) rot=(0,0,1;0rad)
  Radius = 3
FEATURE [Part::Cylinder] Cylinder1789  label="Válec1789"
  Angle = 360
  AttacherType = Attacher::AttachEngine3D
  Height = 3
  Placement = pos=(-24,73,-80) rot=(0,0,1;0rad)
  Radius = 3
FEATURE [Part::Cylinder] Cylinder1790  label="Válec1790"
  Angle = 360
  AttacherType = Attacher::AttachEngine3D
  Height = 3
  Placement = pos=(-15,125,-80) rot=(0,0,1;0rad)
  Radius = 3
FEATURE [Part::Cylinder] Cylinder1791  label="Válec1791"
  Angle = 360
  AttacherType = Attacher::AttachEngine3D
  Height = 3
  Placement = pos=(15,125,-80) rot=(0,0,1;0rad)
  Radius = 3
FEATURE [Part::Compound] Compound888
  Links = -> [Cylinder1788,Cylinder1789,Cylinder1790,Cylinder1791]
  Placement = pos=(0,0,161) rot=(0,0,1;0rad)
FEATURE [Part::Chamfer] Chamfer059
  Base = -> Cut519
  Edges = 2 edges r=3: [Edge3,Edge15]
FEATURE [Part::Chamfer] Chamfer060
  Base = -> Chamfer059
  Edges = 2 edges r=2: [Edge1,Edge12]
FEATURE [Part::Chamfer] Chamfer061
  Base = -> Chamfer060
  Edges = 1 edges r=1: [Edge27]
FEATURE [Part::Cut] Cut520
  Base = -> Chamfer061
  Tool = -> Compound887
FEATURE [Part::Cut] Cut521
  Base = -> Cut520
  Placement = pos=(-39,0,-59) rot=(0,0,-1;1.5708rad)
  Tool = -> Compound888
FEATURE [Part::Box] Box183  label="Krychle183"
  AttacherType = Attacher::AttachEngine3D
  Height = 2
  Length = 16
  Placement = pos=(60,2,16) rot=(0,0,1;0rad)
  Width = 6
FEATURE [Part::Box] Box182  label="Krychle182"
  AttacherType = Attacher::AttachEngine3D
  Height = 2
  Length = 16
  Placement = pos=(60,2,10) rot=(0,0,1;0rad)
  Width = 6
FEATURE [Part::Box] Box181  label="Krychle181"
  AttacherType = Attacher::AttachEngine3D
  Height = 20
  Length = 10
  Placement = pos=(97,-29,7) rot=(0,0,1;0rad)
  Width = 108
FEATURE [Part::Box] Box184  label="Krychle184"
  AttacherType = Attacher::AttachEngine3D
  Height = 2
  Length = 16
  Placement = pos=(60,-25,10) rot=(0,0,1;0rad)
  Width = 6
FEATURE [Part::Box] Box185  label="Krychle185"
  AttacherType = Attacher::AttachEngine3D
  Height = 2
  Length = 16
  Placement = pos=(60,-25,16) rot=(0,0,1;0rad)
  Width = 6
FEATURE [Part::Box] Box186  label="Krychle186"
  AttacherType = Attacher::AttachEngine3D
  Height = 2
  Length = 16
  Placement = pos=(60,-36,10) rot=(0,0,1;0rad)
  Width = 6
FEATURE [Part::Box] Box191  label="Krychle191"
  AttacherType = Attacher::AttachEngine3D
  Height = 2
  Length = 16
  Placement = pos=(60,30,10) rot=(0,0,1;0rad)
  Width = 6
FEATURE [Part::Box] Box193  label="Krychle193"
  AttacherType = Attacher::AttachEngine3D
  Height = 2
  Length = 16
  Placement = pos=(60,15,16) rot=(0,0,1;0rad)
  Width = 6
FEATURE [Part::Box] Box195  label="Krychle195"
  AttacherType = Attacher::AttachEngine3D
  Height = 2
  Length = 16
  Placement = pos=(60,46,16) rot=(0,0,1;0rad)
  Width = 6
FEATURE [Part::Box] Box194  label="Krychle194"
  AttacherType = Attacher::AttachEngine3D
  Height = 2
  Length = 16
  Placement = pos=(60,30,16) rot=(0,0,1;0rad)
  Width = 6
FEATURE [Part::Box] Box188  label="Krychle188"
  AttacherType = Attacher::AttachEngine3D
  Height = 2
  Length = 16
  Placement = pos=(60,-51,10) rot=(0,0,1;0rad)
  Width = 6
FEATURE [Part::Box] Box190  label="Krychle190"
  AttacherType = Attacher::AttachEngine3D
  Height = 2
  Length = 16
  Placement = pos=(60,15,10) rot=(0,0,1;0rad)
  Width = 6
FEATURE [Part::Box] Box187  label="Krychle187"
  AttacherType = Attacher::AttachEngine3D
  Height = 2
  Length = 16
  Placement = pos=(60,-36,16) rot=(0,0,1;0rad)
  Width = 6
FEATURE [Part::Box] Box189  label="Krychle189"
  AttacherType = Attacher::AttachEngine3D
  Height = 2
  Length = 16
  Placement = pos=(60,-51,16) rot=(0,0,1;0rad)
  Width = 6
FEATURE [Part::Box] Box192  label="Krychle192"
  AttacherType = Attacher::AttachEngine3D
  Height = 2
  Length = 16
  Placement = pos=(60,46,10) rot=(0,0,1;0rad)
  Width = 6
FEATURE [Part::Compound] Compound585
  Links = -> [Box182,Box183,Box184,Box185,Box186,Box187,Box188,Box189,Box190,Box191,Box192,Box193,Box194,Box195]
  Placement = pos=(39,24,3) rot=(0,0,1;0rad)
FEATURE [Part::Cylinder] Cylinder431  label="Válec431"
  Angle = 360
  AttacherType = Attacher::AttachEngine3D
  Height = 100
  Placement = pos=(24,51,25) rot=(0,1,0;1.5708rad)
  Radius = 5
FEATURE [Part::Cylinder] Cylinder433  label="Válec433"
  Angle = 360
  AttacherType = Attacher::AttachEngine3D
  Height = 100
  Placement = pos=(24,36,34) rot=(0,1,0;1.5708rad)
  Radius = 5
FEATURE [Part::Cylinder] Cylinder437  label="Válec437"
  Angle = 360
  AttacherType = Attacher::AttachEngine3D
  Height = 100
  Placement = pos=(24,23,-5) rot=(0,1,0;1.5708rad)
  Radius = 5
FEATURE [Part::Cylinder] Cylinder442  label="Válec442"
  Angle = 360
  AttacherType = Attacher::AttachEngine3D
  Height = 50
  Placement = pos=(63,-48,-12) rot=(0,0,1;0rad)
  Radius = 1.5
FEATURE [Part::Cylinder] Cylinder434  label="Válec434"
  Angle = 360
  AttacherType = Attacher::AttachEngine3D
  Height = 100
  Placement = pos=(24,-36,34) rot=(0,1,0;1.5708rad)
  Radius = 5
FEATURE [Part::Cylinder] Cylinder440  label="Válec440"
  Angle = 360
  AttacherType = Attacher::AttachEngine3D
  Height = 50
  Placement = pos=(63,-22,-12) rot=(0,0,1;0rad)
  Radius = 1.5
FEATURE [Part::Cylinder] Cylinder435  label="Válec435"
  Angle = 360
  AttacherType = Attacher::AttachEngine3D
  Height = 100
  Placement = pos=(24,-23,-5) rot=(0,1,0;1.5708rad)
  Radius = 5
FEATURE [Part::Cylinder] Cylinder439  label="Válec439"
  Angle = 360
  AttacherType = Attacher::AttachEngine3D
  Height = 50
  Placement = pos=(63,5,-12) rot=(0,0,1;0rad)
  Radius = 1.5
FEATURE [Part::Cylinder] Cylinder445  label="Válec445"
  Angle = 360
  AttacherType = Attacher::AttachEngine3D
  Height = 50
  Placement = pos=(63,49,-12) rot=(0,0,1;0rad)
  Radius = 1.5
FEATURE [Part::Cylinder] Cylinder432  label="Válec432"
  Angle = 360
  AttacherType = Attacher::AttachEngine3D
  Height = 100
  Placement = pos=(24,-51,25) rot=(0,1,0;1.5708rad)
  Radius = 5
FEATURE [Part::Cylinder] Cylinder436  label="Válec436"
  Angle = 360
  AttacherType = Attacher::AttachEngine3D
  Height = 100
  Placement = pos=(24,51,7) rot=(0,1,0;1.5708rad)
  Radius = 5
FEATURE [Part::Cylinder] Cylinder444  label="Válec444"
  Angle = 360
  AttacherType = Attacher::AttachEngine3D
  Height = 50
  Placement = pos=(63,33,-12) rot=(0,0,1;0rad)
  Radius = 1.5
FEATURE [Part::Cylinder] Cylinder438  label="Válec438"
  Angle = 360
  AttacherType = Attacher::AttachEngine3D
  Height = 100
  Placement = pos=(24,-51,7) rot=(0,1,0;1.5708rad)
  Radius = 5
FEATURE [Part::Cylinder] Cylinder441  label="Válec441"
  Angle = 360
  AttacherType = Attacher::AttachEngine3D
  Height = 50
  Placement = pos=(63,-38,-12) rot=(0,0,1;0rad)
  Radius = 1.5
FEATURE [Part::Cylinder] Cylinder443  label="Válec443"
  Angle = 360
  AttacherType = Attacher::AttachEngine3D
  Height = 50
  Placement = pos=(63,18,-12) rot=(0,0,1;0rad)
  Radius = 1.5
FEATURE [Part::Compound] Compound590
  Links = -> [Cylinder439,Cylinder440,Cylinder441,Cylinder442,Cylinder443,Cylinder444,Cylinder445]
  Placement = pos=(39,24,0) rot=(0,0,1;0rad)
FEATURE [Part::Compound] Compound589
  Links = -> [Cylinder431,Cylinder432,Cylinder433,Cylinder434,Cylinder435,Cylinder436,Cylinder437,Cylinder438]
  Placement = pos=(32,0,0) rot=(0,0,1;0rad)
FEATURE [Part::Cut] Cut363
  Base = -> Box181
  Tool = -> Compound589
FEATURE [Part::Cut] Cut364
  Base = -> Cut363
  Tool = -> Compound590
FEATURE [Part::Cut] Cut365  label="subshift"
  Base = -> Cut364
  Placement = pos=(17,144,-56) rot=(0.57735,-0.57735,-0.57735;2.0944rad)
  Tool = -> Compound585
FEATURE [Part::Chamfer] Chamfer062
  Base = -> Tube090
  Edges = 1 edges r=2: [Edge1]
FEATURE [Part::Cut] Cut522
  Base = -> Chamfer062
  Tool = -> Compound877
FEATURE [Part::Cut] Cut523  label="G-midi_bear-fix"
  Base = -> Cut522
  Placement = pos=(0,0,-1) rot=(0,0,1;0rad)
  Tool = -> Compound880
FEATURE [Part::Box] Box711  label="Krychle711"
  AttacherType = Attacher::AttachEngine3D
  Height = 27
  Length = 44
  Placement = pos=(-22,15,-3) rot=(0,0,1;0rad)
  Width = 32
FEATURE [Part::Box] Box712  label="Krychle712"
  AttacherType = Attacher::AttachEngine3D
  Height = 28
  Length = 20.4
  Placement = pos=(-10.2,20,-3) rot=(0,0,1;0rad)
  Width = 27
FEATURE [Part::Cut] Cut524
  Base = -> Box711
  Tool = -> Box712
FEATURE [Part::Cylinder] Cylinder1792  label="Válec1792"
  Angle = 360
  AttacherType = Attacher::AttachEngine3D
  Height = 32
  Placement = pos=(0,0,-3) rot=(0,0,1;0rad)
  Radius = 35
FEATURE [Part::Cylinder] Cylinder1793  label="Válec1793"
  Angle = 360
  AttacherType = Attacher::AttachEngine3D
  Height = 32
  Placement = pos=(0,0,-3) rot=(0,0,1;0rad)
  Radius = 35
FEATURE [Part::Cylinder] Cylinder1794  label="Válec1794"
  Angle = 360
  AttacherType = Attacher::AttachEngine3D
  Height = 32
  Placement = pos=(0,0,-3) rot=(0,0,1;0rad)
  Radius = 35
FEATURE [Part::Cut] Cut525
  Base = -> Cut521
  Placement = pos=(0,0,0) rot=(0,0,1;3.14159rad)
  Tool = -> Cylinder1792
FEATURE [Part::Cut] Cut526
  Base = -> Compound876
  Placement = pos=(0,0,0) rot=(0,0,1;3.14159rad)
  Tool = -> Cylinder1794
FEATURE [Part::Compound] Compound889  label="G-midi_bear-hold-encoder-rear1"
  Links = -> [Cut512,Cut526,Tube088]
  Placement = pos=(0,0,-1) rot=(0,0,1;0rad)
FEATURE [Part::Compound] Compound890  label="G-midi_bear-hold-encoder-front"
  Links = -> [Cut508,Cut525]
  Placement = pos=(0,0,-1) rot=(0,0,1;0rad)
FEATURE [Part::Cut] Cut527
  Base = -> Cut524
  Placement = pos=(0,0,-1) rot=(0,0,1;0rad)
  Tool = -> Cylinder1793
FEATURE [Part::Cylinder] Cylinder1795  label="Válec1795"
  Angle = 360
  AttacherType = Attacher::AttachEngine3D
  Height = 64
  Placement = pos=(-32,42,1) rot=(0,1,0;1.5708rad)
  Radius = 1.5
FEATURE [Part::Cylinder] Cylinder1796  label="Válec1796"
  Angle = 360
  AttacherType = Attacher::AttachEngine3D
  Height = 64
  Placement = pos=(-32,42,17) rot=(0,1,0;1.5708rad)
  Radius = 1.5
FEATURE [Part::Compound] Compound891
  Links = -> [Cylinder1795,Cylinder1796]
FEATURE [Part::Cylinder] Cylinder1797  label="Válec1797"
  Angle = 360
  AttacherType = Attacher::AttachEngine3D
  Height = 16
  Placement = pos=(-34,42,1) rot=(0,1,0;1.5708rad)
  Radius = 4
FEATURE [Part::Cylinder] Cylinder1798  label="Válec1798"
  Angle = 360
  AttacherType = Attacher::AttachEngine3D
  Height = 16
  Placement = pos=(-34,42,17) rot=(0,1,0;1.5708rad)
  Radius = 4
FEATURE [Part::Cylinder] Cylinder1799  label="Válec1799"
  Angle = 360
  AttacherType = Attacher::AttachEngine3D
  Height = 16
  Placement = pos=(18,42,1) rot=(0,1,0;1.5708rad)
  Radius = 4
FEATURE [Part::Cylinder] Cylinder1800  label="Válec1800"
  Angle = 360
  AttacherType = Attacher::AttachEngine3D
  Height = 16
  Placement = pos=(18,42,17) rot=(0,1,0;1.5708rad)
  Radius = 4
FEATURE [Part::Compound] Compound892
  Links = -> [Cylinder1797,Cylinder1800,Cylinder1799,Cylinder1798]
FEATURE [Part::Cut] Cut528
  Base = -> Cut527
  Tool = -> Compound892
FEATURE [Part::Cut] Cut529
  Base = -> Cut528
  Tool = -> Compound891
FEATURE [Part::Box] Box713  label="Krychle713"
  AttacherType = Attacher::AttachEngine3D
  Height = 20
  Length = 20
  Placement = pos=(-10,15.1,20) rot=(0,0,1;0rad)
  Width = 3
FEATURE [Part::Box] Box714  label="Krychle714"
  AttacherType = Attacher::AttachEngine3D
  Height = 20
  Length = 20
  Placement = pos=(-15.1,-10,20) rot=(0,0,1;1.5708rad)
  Width = 3
FEATURE [Part::Box] Box715  label="Krychle715"
  AttacherType = Attacher::AttachEngine3D
  Height = 20
  Length = 20
  Placement = pos=(10,-15.1,20) rot=(0,0,1;3.14159rad)
  Width = 3
FEATURE [Part::Box] Box716  label="Krychle716"
  AttacherType = Attacher::AttachEngine3D
  Height = 20
  Length = 20
  Placement = pos=(15.1,10,20) rot=(0,0,-1;1.5708rad)
  Width = 3
FEATURE [Part::Compound] Compound893
  Links = -> [Box713,Box714,Box715,Box716]
  Placement = pos=(0,0,-2) rot=(0,0,1;0rad)
FEATURE [Part::Cylinder] Cylinder1801  label="Válec1801"
  Angle = 360
  AttacherType = Attacher::AttachEngine3D
  Height = 10
  Placement = pos=(0,-12,30) rot=(1,0,0;1.5708rad)
  Radius = 2.5
FEATURE [Part::Cylinder] Cylinder1802  label="Válec1802"
  Angle = 360
  AttacherType = Attacher::AttachEngine3D
  Height = 10
  Placement = pos=(12,6e-15,30) rot=(0.57735,0.57735,0.57735;2.0944rad)
  Radius = 2.5
FEATURE [Part::Cylinder] Cylinder1803  label="Válec1803"
  Angle = 360
  AttacherType = Attacher::AttachEngine3D
  Height = 10
  Placement = pos=(-1.5e-14,12,30) rot=(0,0.707107,0.707107;3.14159rad)
  Radius = 2.5
FEATURE [Part::Cylinder] Cylinder1804  label="Válec1804"
  Angle = 360
  AttacherType = Attacher::AttachEngine3D
  Height = 10
  Placement = pos=(-12,-2.4e-14,30) rot=(-0.57735,0.57735,0.57735;4.18879rad)
  Radius = 2.5
FEATURE [Part::Compound] Compound894
  Links = -> [Cylinder1801,Cylinder1802,Cylinder1803,Cylinder1804]
  Placement = pos=(0,0,-2) rot=(0,0,1;0rad)
FEATURE [Part::Cut] Cut530
  Base = -> Compound893
  Placement = pos=(0,0,5) rot=(0,0,1;0rad)
  Tool = -> Compound894
FEATURE [Part::Chamfer] Chamfer063
  Base = -> Cut530
  Edges = 5 edges r=2: [Edge18,Edge27,Edge33,Edge42,Edge57]
FEATURE [Part::Chamfer] Chamfer064
  Base = -> Chamfer063
  Edges = 3 edges r=2: [Edge49,Edge63,Edge72]
FEATURE [Part::Chamfer] Chamfer065
  Base = -> Chamfer064
  Edges = 4 edges r=1: [Edge1,Edge29,Edge50,Edge71]
FEATURE [Part::Box] Box717  label="Krychle717"
  AttacherType = Attacher::AttachEngine3D
  Height = 25
  Length = 30.2
  Placement = pos=(-15.1,-15.1,0) rot=(0,0,1;0rad)
  Width = 30.2
FEATURE [Part::Cylinder] Cylinder1805  label="Válec1805"
  Angle = 360
  AttacherType = Attacher::AttachEngine3D
  Height = 25
  Radius = 25.15
FEATURE [Part::Cut] Cut531
  Base = -> Cylinder1805
  Tool = -> Box717
FEATURE [Part::Chamfer] Chamfer067
  Base = -> Cut531
  Edges = 2 edges r=0.5: [Edge9,Edge11]
FEATURE [Part::Chamfer] Chamfer066
  Base = -> Chamfer067
  Edges = 1 edges r=1: [Edge22]
FEATURE [Part::Chamfer] Chamfer068
  Base = -> Chamfer066
  Edges = 1 edges r=0.5: [Edge3]
FEATURE [Part::Compound] Compound895  label="G-midi_rotator-fix"
  Links = -> [Chamfer065,Chamfer068]
  Placement = pos=(0,0,24) rot=(0,1,0;3.14159rad)
FEATURE [Mesh::Feature] Mesh  label="G-midi_bear-fix (Meshed)"
FEATURE [Part::Cylinder] Cylinder154  label="Válec154"
  Angle = 360
  AttacherType = Attacher::AttachEngine3D
  Height = 10
  Placement = pos=(22.6274,22.6274,10) rot=(0,0,-1;0.785398rad)
  Radius = 1.5
FEATURE [Part::Cylinder] Cylinder156  label="Válec156"
  Angle = 360
  AttacherType = Attacher::AttachEngine3D
  Height = 20
  Placement = pos=(4,38,25) rot=(0,1,0;1.5708rad)
  Radius = 1.5
FEATURE [Part::Cylinder] Cylinder157  label="Válec157"
  Angle = 360
  AttacherType = Attacher::AttachEngine3D
  Height = 20
  Placement = pos=(18,38,25) rot=(0,1,0;1.5708rad)
  Radius = 4
FEATURE [Part::Box] Box067  label="Krychle067"
  AttacherType = Attacher::AttachEngine3D
  Height = 20
  Length = 20.4
  Placement = pos=(-10.2,20,10) rot=(0,0,1;0rad)
  Width = 27
FEATURE [Part::Cylinder] Cylinder152  label="Válec152"
  Angle = 360
  AttacherType = Attacher::AttachEngine3D
  Height = 10
  Placement = pos=(22.6274,-22.6274,10) rot=(0,0,1;3.92699rad)
  Radius = 1.5
FEATURE [Part::Box] Box059  label="Krychle059"
  AttacherType = Attacher::AttachEngine3D
  Height = 2
  Length = 6
  Placement = pos=(-22.6274,18.3848,14) rot=(0,0,1;0.785398rad)
  Width = 6
FEATURE [Part::Cylinder] Cylinder151  label="Válec151"
  Angle = 360
  AttacherType = Attacher::AttachEngine3D
  Height = 10
  Placement = pos=(1e-14,-32,10) rot=(0,0,1;3.14159rad)
  Radius = 1.5
FEATURE [Part::Cylinder] Cylinder153  label="Válec153"
  Angle = 360
  AttacherType = Attacher::AttachEngine3D
  Height = 10
  Placement = pos=(32,1.1e-14,10) rot=(0,0,-1;1.5708rad)
  Radius = 1.5
FEATURE [Part::Box] Box063  label="Krychle063"
  AttacherType = Attacher::AttachEngine3D
  Height = 2
  Length = 6
  Placement = pos=(22.6274,-18.3848,14) rot=(0,0,1;3.92699rad)
  Width = 6
FEATURE [Part::Box] Box065  label="Krychle065"
  AttacherType = Attacher::AttachEngine3D
  Height = 2
  Length = 6
  Placement = pos=(18.3848,22.6274,14) rot=(0,0,-1;0.785398rad)
  Width = 6
FEATURE [Part::Box] Box062  label="Krychle062"
  AttacherType = Attacher::AttachEngine3D
  Height = 2
  Length = 6
  Placement = pos=(3,-29,14) rot=(0,0,1;3.14159rad)
  Width = 6
FEATURE [Part::Box] Box060  label="Krychle060"
  AttacherType = Attacher::AttachEngine3D
  Height = 2
  Length = 6
  Placement = pos=(-29,-3,14) rot=(0,0,1;1.5708rad)
  Width = 6
FEATURE [Part::Box] Box061  label="Krychle061"
  AttacherType = Attacher::AttachEngine3D
  Height = 2
  Length = 6
  Placement = pos=(-18.3848,-22.6274,14) rot=(0,0,1;2.35619rad)
  Width = 6
FEATURE [Part::Box] Box064  label="Krychle064"
  AttacherType = Attacher::AttachEngine3D
  Height = 2
  Length = 6
  Placement = pos=(29,3,14) rot=(0,0,-1;1.5708rad)
  Width = 6
FEATURE [Part::Box] Box066  label="Krychle066"
  AttacherType = Attacher::AttachEngine3D
  Height = 20
  Length = 50
  Placement = pos=(-25,15,10) rot=(0,0,1;0rad)
  Width = 32
FEATURE [Part::Cylinder] Cylinder155  label="Válec155"
  Angle = 360
  AttacherType = Attacher::AttachEngine3D
  Height = 20
  Placement = pos=(0,0,10) rot=(0,0,1;0rad)
  Radius = 35
FEATURE [Part::Cut] Cut056
  Base = -> Box066
  Tool = -> Cylinder155
FEATURE [Part::Cut] Cut057
  Base = -> Cut056
  Tool = -> Box067
FEATURE [Part::Cylinder] Cylinder158  label="Válec158"
  Angle = 360
  AttacherType = Attacher::AttachEngine3D
  Height = 20
  Placement = pos=(-24,38,25) rot=(0,1,0;1.5708rad)
  Radius = 1.5
FEATURE [Part::Cylinder] Cylinder159  label="Válec159"
  Angle = 360
  AttacherType = Attacher::AttachEngine3D
  Height = 20
  Placement = pos=(-38,38,25) rot=(0,1,0;1.5708rad)
  Radius = 4
FEATURE [Part::Torus] Torus002  label="Anuloid002"
  Angle1 = -180
  Angle2 = 180
  Angle3 = 360
  AttacherType = Attacher::AttachEngine3D
  Placement = pos=(0,0,23.5) rot=(0,0,1;0rad)
  Radius1 = 28
  Radius2 = 2.2
FEATURE [Part::FeaturePython] Tube009  # WARN: FeaturePython — macro-defined, semantics opaque (R4)
  AttacherType = Attacher::AttachEngine3D
  Height = 20
  InnerRadius = 29
  OuterRadius = 35
  Placement = pos=(0,0,10) rot=(0,0,1;0rad)
FEATURE [Part::Cut] Cut052
  Base = -> Tube009
  Tool = -> Torus002
FEATURE [Part::Cylinder] Cylinder146  label="Válec146"
  Angle = 360
  AttacherType = Attacher::AttachEngine3D
  Height = 10
  Placement = pos=(28,0,23.5) rot=(0,0,1;0rad)
  Radius = 2.2
FEATURE [Part::Cut] Cut053
  Base = -> Cut052
  Tool = -> Cylinder146
FEATURE [Part::Cylinder] Cylinder147  label="Válec147"
  Angle = 360
  AttacherType = Attacher::AttachEngine3D
  Height = 10
  Placement = pos=(0,32,10) rot=(0,0,1;0rad)
  Radius = 1.5
FEATURE [Part::Box] Box058  label="Krychle058"
  AttacherType = Attacher::AttachEngine3D
  Height = 2
  Length = 6
  Placement = pos=(-3,29,14) rot=(0,0,1;0rad)
  Width = 6
FEATURE [Part::Compound] Compound048
  Links = -> [Box059,Box060,Box061,Box062,Box063,Box064,Box065,Box058]
FEATURE [Part::Cylinder] Cylinder148  label="Válec148"
  Angle = 360
  AttacherType = Attacher::AttachEngine3D
  Height = 10
  Placement = pos=(-22.6274,22.6274,10) rot=(0,0,1;0.785398rad)
  Radius = 1.5
FEATURE [Part::Cylinder] Cylinder150  label="Válec150"
  Angle = 360
  AttacherType = Attacher::AttachEngine3D
  Height = 10
  Placement = pos=(-22.6274,-22.6274,10) rot=(0,0,1;2.35619rad)
  Radius = 1.5
FEATURE [Part::Cylinder] Cylinder149  label="Válec149"
  Angle = 360
  AttacherType = Attacher::AttachEngine3D
  Height = 10
  Placement = pos=(-32,0,10) rot=(0,0,1;1.5708rad)
  Radius = 1.5
FEATURE [Part::Compound] Compound047
  Links = -> [Cylinder148,Cylinder149,Cylinder150,Cylinder151,Cylinder152,Cylinder153,Cylinder154,Cylinder147]
FEATURE [Part::Cut] Cut054
  Base = -> Cut053
  Tool = -> Compound047
FEATURE [Part::Cut] Cut055  label="gearovina-midi_loziskovina1"
  Base = -> Cut054
  Tool = -> Compound048
FEATURE [Part::Cylinder] Cylinder116  label="Válec116"
  Angle = 360
  AttacherType = Attacher::AttachEngine3D
  Height = 15
  Placement = pos=(18.3848,-18.3848,-20) rot=(0,0,1;3.92699rad)
  Radius = 1.5
FEATURE [Part::Cylinder] Cylinder117  label="Válec117"
  Angle = 360
  AttacherType = Attacher::AttachEngine3D
  Height = 15
  Placement = pos=(26,1e-14,-20) rot=(0,0,-1;1.5708rad)
  Radius = 1.5
FEATURE [Part::Cylinder] Cylinder115  label="Válec115"
  Angle = 360
  AttacherType = Attacher::AttachEngine3D
  Height = 15
  Placement = pos=(1.1e-14,-26,-20) rot=(0,0,1;3.14159rad)
  Radius = 1.5
FEATURE [Part::Cylinder] Cylinder112  label="Válec112"
  Angle = 360
  AttacherType = Attacher::AttachEngine3D
  Height = 15
  Placement = pos=(-18.3848,18.3848,-20) rot=(0,0,1;0.785398rad)
  Radius = 1.5
FEATURE [Part::Box] Box053  label="Krychle053"
  AttacherType = Attacher::AttachEngine3D
  Height = 2
  Length = 6
  Placement = pos=(23,3,-13) rot=(0,0,-1;1.5708rad)
  Width = 6
FEATURE [Part::Cylinder] Cylinder111  label="Válec111"
  Angle = 360
  AttacherType = Attacher::AttachEngine3D
  Height = 15
  Placement = pos=(0,26,-20) rot=(0,0,1;0rad)
  Radius = 1.5
FEATURE [Part::Cylinder] Cylinder114  label="Válec114"
  Angle = 360
  AttacherType = Attacher::AttachEngine3D
  Height = 15
  Placement = pos=(-18.3848,-18.3848,-20) rot=(0,0,1;2.35619rad)
  Radius = 1.5
FEATURE [Part::Box] Box051  label="Krychle051"
  AttacherType = Attacher::AttachEngine3D
  Height = 2
  Length = 6
  Placement = pos=(3,-23,-13) rot=(0,0,1;3.14159rad)
  Width = 6
FEATURE [Part::Box] Box047  label="Krychle047"
  AttacherType = Attacher::AttachEngine3D
  Height = 2
  Length = 6
  Placement = pos=(-3,23,-13) rot=(0,0,1;0rad)
  Width = 6
FEATURE [Part::Cylinder] Cylinder113  label="Válec113"
  Angle = 360
  AttacherType = Attacher::AttachEngine3D
  Height = 15
  Placement = pos=(-26,-4e-15,-20) rot=(0,0,1;1.5708rad)
  Radius = 1.5
FEATURE [Part::Box] Box048  label="Krychle048"
  AttacherType = Attacher::AttachEngine3D
  Height = 2
  Length = 6
  Placement = pos=(-18.3848,14.1421,-13) rot=(0,0,1;0.785398rad)
  Width = 6
FEATURE [Part::Box] Box049  label="Krychle049"
  AttacherType = Attacher::AttachEngine3D
  Height = 2
  Length = 6
  Placement = pos=(-23,-3,-13) rot=(0,0,1;1.5708rad)
  Width = 6
FEATURE [Part::Box] Box050  label="Krychle050"
  AttacherType = Attacher::AttachEngine3D
  Height = 2
  Length = 6
  Placement = pos=(-14.1421,-18.3848,-13) rot=(0,0,1;2.35619rad)
  Width = 6
FEATURE [Part::Cylinder] Cylinder118  label="Válec118"
  Angle = 360
  AttacherType = Attacher::AttachEngine3D
  Height = 15
  Placement = pos=(18.3848,18.3848,-20) rot=(0,0,-1;0.785398rad)
  Radius = 1.5
FEATURE [Part::Compound] Compound897
  Links = -> [Cylinder111,Cylinder112,Cylinder113,Cylinder114,Cylinder115,Cylinder116,Cylinder117,Cylinder118]
  Placement = pos=(0,0,0) rot=(0,0,1;0.392699rad)
FEATURE [Part::Box] Box052  label="Krychle052"
  AttacherType = Attacher::AttachEngine3D
  Height = 2
  Length = 6
  Placement = pos=(18.3848,-14.1421,-13) rot=(0,0,1;3.92699rad)
  Width = 6
FEATURE [Part::Box] Box054  label="Krychle054"
  AttacherType = Attacher::AttachEngine3D
  Height = 2
  Length = 6
  Placement = pos=(14.1421,18.3848,-13) rot=(0,0,-1;0.785398rad)
  Width = 6
FEATURE [Part::Compound] Compound039
  Links = -> [Box048,Box049,Box050,Box051,Box052,Box053,Box054,Box047]
  Placement = pos=(0,0,0) rot=(0,0,1;0.392699rad)
FEATURE [Part::Cylinder] Cylinder110  label="Válec110"
  Angle = 360
  AttacherType = Attacher::AttachEngine3D
  Height = 10
  Radius = 29
FEATURE [Part::Cylinder] Cylinder122  label="Válec122"
  Angle = 360
  AttacherType = Attacher::AttachEngine3D
  Height = 3
  Placement = pos=(-22.6274,-22.6274,4) rot=(0,0,1;2.35619rad)
  Radius = 3
FEATURE [Part::Cylinder] Cylinder121  label="Válec121"
  Angle = 360
  AttacherType = Attacher::AttachEngine3D
  Height = 3
  Placement = pos=(-32,0,4) rot=(0,0,1;1.5708rad)
  Radius = 3
FEATURE [Part::Cylinder] Cylinder123  label="Válec123"
  Angle = 360
  AttacherType = Attacher::AttachEngine3D
  Height = 3
  Placement = pos=(1e-14,-32,4) rot=(0,0,1;3.14159rad)
  Radius = 3
FEATURE [Part::Cylinder] Cylinder119  label="Válec119"
  Angle = 360
  AttacherType = Attacher::AttachEngine3D
  Height = 3
  Placement = pos=(0,32,4) rot=(0,0,1;0rad)
  Radius = 3
FEATURE [Part::Cylinder] Cylinder109  label="Válec109"
  Angle = 360
  AttacherType = Attacher::AttachEngine3D
  Height = 10
  Radius = 29
FEATURE [Part::Cylinder] Cylinder120  label="Válec120"
  Angle = 360
  AttacherType = Attacher::AttachEngine3D
  Height = 3
  Placement = pos=(-22.6274,22.6274,4) rot=(0,0,1;0.785398rad)
  Radius = 3
FEATURE [Part::Cylinder] Cylinder124  label="Válec124"
  Angle = 360
  AttacherType = Attacher::AttachEngine3D
  Height = 3
  Placement = pos=(22.6274,-22.6274,4) rot=(0,0,1;3.92699rad)
  Radius = 3
FEATURE [Part::Cylinder] Cylinder125  label="Válec125"
  Angle = 360
  AttacherType = Attacher::AttachEngine3D
  Height = 3
  Placement = pos=(32,1.1e-14,4) rot=(0,0,-1;1.5708rad)
  Radius = 3
FEATURE [Part::FeaturePython] wormgear041  # WARN: FeaturePython — macro-defined, semantics opaque (R4)
  AttacherType = Attacher::AttachEngine3D
  Placement = pos=(0,0,0) rot=(0,0,1;1.13796rad)
  beta = 30.9638
  clearance = 0.25
  diameter = 44
  head = 0
  height = 12
  module = 0.8
  pressure_angle = 20
  reverse_pitch = false
  teeth = 33
  version = 0.0.3
FEATURE [Part::Cut] Cut038
  Base = -> Cylinder110
  Placement = pos=(0,0,-10) rot=(0,0,1;0rad)
  Tool = -> wormgear041
FEATURE [Part::FeaturePython] wormgear042  # WARN: FeaturePython — macro-defined, semantics opaque (R4)
  AttacherType = Attacher::AttachEngine3D
  Placement = pos=(0,0,0) rot=(0,0,1;1.13446rad)
  beta = 30.9638
  clearance = 0.25
  diameter = 44
  head = 0
  height = 12
  module = 0.8
  pressure_angle = 20
  reverse_pitch = true
  teeth = 33
  version = 0.0.3
FEATURE [Part::Cut] Cut039
  Base = -> Cylinder109
  Tool = -> wormgear042
FEATURE [Part::Compound] Compound038  label="superokruh"
  Links = -> [Cut038,Cut039]
FEATURE [Part::FeaturePython] Tube008  # WARN: FeaturePython — macro-defined, semantics opaque (R4)
  AttacherType = Attacher::AttachEngine3D
  Height = 6
  InnerRadius = 29
  OuterRadius = 35
  Placement = pos=(0,0,4) rot=(0,0,1;0rad)
FEATURE [Part::Cylinder] Cylinder126  label="Válec126"
  Angle = 360
  AttacherType = Attacher::AttachEngine3D
  Height = 3
  Placement = pos=(22.6274,22.6274,4) rot=(0,0,-1;0.785398rad)
  Radius = 3
FEATURE [Part::Compound] Compound040
  Links = -> [Cylinder119,Cylinder120,Cylinder121,Cylinder122,Cylinder123,Cylinder124,Cylinder125,Cylinder126]
FEATURE [Part::Cut] Cut041
  Base = -> Tube008
  Tool = -> Compound040
FEATURE [Part::Cylinder] Cylinder127  label="Válec127"
  Angle = 360
  AttacherType = Attacher::AttachEngine3D
  Height = 15
  Placement = pos=(0,32,0) rot=(0,0,1;0rad)
  Radius = 1.5
FEATURE [Part::Cylinder] Cylinder129  label="Válec129"
  Angle = 360
  AttacherType = Attacher::AttachEngine3D
  Height = 15
  Placement = pos=(-32,0,0) rot=(0,0,1;1.5708rad)
  Radius = 1.5
FEATURE [Part::Box] Box055  label="Krychle055"
  AttacherType = Attacher::AttachEngine3D
  Height = 26
  Length = 40
  Placement = pos=(-20,15,-16) rot=(0,0,1;0rad)
  Width = 30
FEATURE [Part::Cylinder] Cylinder136  label="Válec136"
  Angle = 360
  AttacherType = Attacher::AttachEngine3D
  Height = 26
  Placement = pos=(0,0,-16) rot=(0,0,1;0rad)
  Radius = 29
FEATURE [Part::Cut] Cut045
  Base = -> Box055
  Tool = -> Cylinder136
FEATURE [Part::Cylinder] Cylinder133  label="Válec133"
  Angle = 360
  AttacherType = Attacher::AttachEngine3D
  Height = 15
  Placement = pos=(32,1.1e-14,0) rot=(0,0,-1;1.5708rad)
  Radius = 1.5
FEATURE [Part::Cylinder] Cylinder132  label="Válec132"
  Angle = 360
  AttacherType = Attacher::AttachEngine3D
  Height = 15
  Placement = pos=(22.6274,-22.6274,0) rot=(0,0,1;3.92699rad)
  Radius = 1.5
FEATURE [Part::Cylinder] Cylinder128  label="Válec128"
  Angle = 360
  AttacherType = Attacher::AttachEngine3D
  Height = 15
  Placement = pos=(-22.6274,22.6274,0) rot=(0,0,1;0.785398rad)
  Radius = 1.5
FEATURE [Part::Cylinder] Cylinder130  label="Válec130"
  Angle = 360
  AttacherType = Attacher::AttachEngine3D
  Height = 15
  Placement = pos=(-22.6274,-22.6274,0) rot=(0,0,1;2.35619rad)
  Radius = 1.5
FEATURE [Part::Cylinder] Cylinder131  label="Válec131"
  Angle = 360
  AttacherType = Attacher::AttachEngine3D
  Height = 15
  Placement = pos=(1e-14,-32,0) rot=(0,0,1;3.14159rad)
  Radius = 1.5
FEATURE [Part::Cylinder] Cylinder134  label="Válec134"
  Angle = 360
  AttacherType = Attacher::AttachEngine3D
  Height = 15
  Placement = pos=(22.6274,22.6274,0) rot=(0,0,-1;0.785398rad)
  Radius = 1.5
FEATURE [Part::Compound] Compound041
  Links = -> [Cylinder127,Cylinder128,Cylinder129,Cylinder130,Cylinder131,Cylinder132,Cylinder133,Cylinder134]
FEATURE [Part::Cut] Cut042
  Base = -> Cut041
  Tool = -> Compound041
FEATURE [Part::Cylinder] Cylinder141  label="Válec141"
  Angle = 360
  AttacherType = Attacher::AttachEngine3D
  Height = 20
  Placement = pos=(-34,38,-11) rot=(0,1,0;1.5708rad)
  Radius = 4
FEATURE [Part::Cylinder] Cylinder142  label="Válec142"
  Angle = 360
  AttacherType = Attacher::AttachEngine3D
  Height = 20
  Placement = pos=(4,38,5) rot=(0,1,0;1.5708rad)
  Radius = 1.5
FEATURE [Part::Cylinder] Cylinder143  label="Válec143"
  Angle = 360
  AttacherType = Attacher::AttachEngine3D
  Height = 20
  Placement = pos=(4,38,-11) rot=(0,1,0;1.5708rad)
  Radius = 1.5
FEATURE [Part::Compound] Compound045
  Links = -> [Cylinder142,Cylinder143]
FEATURE [Part::Cylinder] Cylinder144  label="Válec144"
  Angle = 360
  AttacherType = Attacher::AttachEngine3D
  Height = 20
  Placement = pos=(14,38,5) rot=(0,1,0;1.5708rad)
  Radius = 4
FEATURE [Part::Cylinder] Cylinder138  label="Válec138"
  Angle = 360
  AttacherType = Attacher::AttachEngine3D
  Height = 20
  Placement = pos=(-24,38,5) rot=(0,1,0;1.5708rad)
  Radius = 1.5
FEATURE [Part::Cylinder] Cylinder139  label="Válec139"
  Angle = 360
  AttacherType = Attacher::AttachEngine3D
  Height = 20
  Placement = pos=(-24,38,-11) rot=(0,1,0;1.5708rad)
  Radius = 1.5
FEATURE [Part::Compound] Compound043
  Links = -> [Cylinder138,Cylinder139]
FEATURE [Part::Cylinder] Cylinder140  label="Válec140"
  Angle = 360
  AttacherType = Attacher::AttachEngine3D
  Height = 20
  Placement = pos=(-34,38,5) rot=(0,1,0;1.5708rad)
  Radius = 4
FEATURE [Part::Compound] Compound042
  Links = -> [Cylinder140,Cylinder141]
FEATURE [Part::Cylinder] Cylinder145  label="Válec145"
  Angle = 360
  AttacherType = Attacher::AttachEngine3D
  Height = 20
  Placement = pos=(14,38,-11) rot=(0,1,0;1.5708rad)
  Radius = 4
FEATURE [Part::Compound] Compound044
  Links = -> [Cylinder144,Cylinder145]
FEATURE [Part::Box] Box057  label="Krychle057"
  AttacherType = Attacher::AttachEngine3D
  Height = 26
  Length = 16
  Placement = pos=(-8,20,-16) rot=(0,0,1;0rad)
  Width = 25
FEATURE [Part::Cut] Cut047
  Base = -> Cut045
  Tool = -> Box057
FEATURE [Part::Cut] Cut048
  Base = -> Cut047
  Tool = -> Compound042
FEATURE [Part::Cut] Cut049
  Base = -> Cut048
  Tool = -> Compound043
FEATURE [Part::Cut] Cut050
  Base = -> Cut049
  Tool = -> Compound044
FEATURE [Part::Cut] Cut051
  Base = -> Cut050
  Tool = -> Compound045
FEATURE [Part::Compound] Compound046  label="gearovina_midi_superokruh1"
  Links = -> [Cut051,Cut042,Compound038]
FEATURE [Part::FeaturePython] Tube007  # WARN: FeaturePython — macro-defined, semantics opaque (R4)
  AttacherType = Attacher::AttachEngine3D
  Height = 6
  InnerRadius = 23
  OuterRadius = 29
  Placement = pos=(0,0,-16) rot=(0,0,1;0rad)
FEATURE [Part::Cut] Cut532
  Base = -> Tube007
  Tool = -> Compound897
FEATURE [Part::Cut] Cut311
  Base = -> Cut532
  Tool = -> Compound039
FEATURE [Part::Compound] Compound538  label="gearovina_midi_superokruh"
  Links = -> [Compound046,Cut311]
  Placement = pos=(0,4,-95) rot=(0,0,1;0rad)
FEATURE [Part::Cylinder] Cylinder795  label="Válec795"
  Angle = 360
  AttacherType = Attacher::AttachEngine3D
  Height = 3
  Placement = pos=(0,25.5,3) rot=(0,0,1;0rad)
  Radius = 3
FEATURE [Part::Cylinder] Cylinder797  label="Válec797"
  Angle = 360
  AttacherType = Attacher::AttachEngine3D
  Height = 20
  Placement = pos=(-25.5,-1e-15,-4) rot=(0,0,1;1.5708rad)
  Radius = 1.5
FEATURE [Part::Cylinder] Cylinder799  label="Válec799"
  Angle = 360
  AttacherType = Attacher::AttachEngine3D
  Height = 20
  Placement = pos=(4e-15,-25.5,-4) rot=(0,0,1;3.14159rad)
  Radius = 1.5
FEATURE [Part::Cylinder] Cylinder800  label="Válec800"
  Angle = 360
  AttacherType = Attacher::AttachEngine3D
  Height = 20
  Placement = pos=(18.0312,-18.0312,-4) rot=(0,0,1;3.92699rad)
  Radius = 1.5
FEATURE [Part::Cylinder] Cylinder801  label="Válec801"
  Angle = 360
  AttacherType = Attacher::AttachEngine3D
  Height = 20
  Placement = pos=(25.5,1e-14,-4) rot=(0,0,-1;1.5708rad)
  Radius = 1.5
FEATURE [Part::Cylinder] Cylinder257  label="Válec257"
  Angle = 360
  AttacherType = Attacher::AttachEngine3D
  Height = 6
  Radius = 34
FEATURE [Part::Cylinder] Cylinder794  label="Válec794"
  Angle = 360
  AttacherType = Attacher::AttachEngine3D
  Height = 20
  Placement = pos=(0,25.5,-4) rot=(0,0,1;0rad)
  Radius = 1.5
FEATURE [Part::Cylinder] Cylinder796  label="Válec796"
  Angle = 360
  AttacherType = Attacher::AttachEngine3D
  Height = 20
  Placement = pos=(-18.0312,18.0312,-4) rot=(0,0,1;0.785398rad)
  Radius = 1.5
FEATURE [Part::Cylinder] Cylinder798  label="Válec798"
  Angle = 360
  AttacherType = Attacher::AttachEngine3D
  Height = 20
  Placement = pos=(-18.0312,-18.0312,-4) rot=(0,0,1;2.35619rad)
  Radius = 1.5
FEATURE [Part::Cylinder] Cylinder1806  label="Válec1806"
  Angle = 360
  AttacherType = Attacher::AttachEngine3D
  Height = 3
  Placement = pos=(4e-15,-25.5,3) rot=(0,0,1;3.14159rad)
  Radius = 3
FEATURE [Part::Cylinder] Cylinder1807  label="Válec1807"
  Angle = 360
  AttacherType = Attacher::AttachEngine3D
  Height = 3
  Placement = pos=(25.5,1e-14,3) rot=(0,0,-1;1.5708rad)
  Radius = 3
FEATURE [Part::Cylinder] Cylinder1808  label="Válec1808"
  Angle = 360
  AttacherType = Attacher::AttachEngine3D
  Height = 3
  Placement = pos=(18.0312,18.0312,3) rot=(0,0,-1;0.785398rad)
  Radius = 3
FEATURE [Part::Box] Box005  label="Krychle005"
  AttacherType = Attacher::AttachEngine3D
  Height = 20
  Length = 20
  Placement = pos=(-10,15.1,20) rot=(0,0,1;0rad)
  Width = 3
FEATURE [Part::Box] Box006  label="Krychle006"
  AttacherType = Attacher::AttachEngine3D
  Height = 20
  Length = 20
  Placement = pos=(10,-15.1,20) rot=(0,0,1;3.14159rad)
  Width = 3
FEATURE [Part::Box] Box007  label="Krychle007"
  AttacherType = Attacher::AttachEngine3D
  Height = 20
  Length = 20
  Placement = pos=(-15.1,-10,20) rot=(0,0,1;1.5708rad)
  Width = 3
FEATURE [Part::Box] Box008  label="Krychle008"
  AttacherType = Attacher::AttachEngine3D
  Height = 20
  Length = 20
  Placement = pos=(15.1,10,20) rot=(0,0,-1;1.5708rad)
  Width = 3
FEATURE [Part::Cylinder] Cylinder1809  label="Válec1809"
  Angle = 360
  AttacherType = Attacher::AttachEngine3D
  Height = 10
  Placement = pos=(0,-12,30) rot=(1,0,0;1.5708rad)
  Radius = 2.5
FEATURE [Part::Cylinder] Cylinder1810  label="Válec1810"
  Angle = 360
  AttacherType = Attacher::AttachEngine3D
  Height = 3
  Placement = pos=(18.0312,-18.0312,3) rot=(0,0,1;3.92699rad)
  Radius = 3
FEATURE [Part::Cylinder] Cylinder1811  label="Válec1811"
  Angle = 360
  AttacherType = Attacher::AttachEngine3D
  Height = 10
  Placement = pos=(12,6e-15,30) rot=(0.57735,0.57735,0.57735;2.0944rad)
  Radius = 2.5
FEATURE [Part::Cylinder] Cylinder1812  label="Válec1812"
  Angle = 360
  AttacherType = Attacher::AttachEngine3D
  Height = 10
  Placement = pos=(-12,-2.4e-14,30) rot=(-0.57735,0.57735,0.57735;4.18879rad)
  Radius = 2.5
FEATURE [Part::Cylinder] Cylinder1813  label="Válec1813"
  Angle = 360
  AttacherType = Attacher::AttachEngine3D
  Height = 10
  Placement = pos=(-1.5e-14,12,30) rot=(0,0.707107,0.707107;3.14159rad)
  Radius = 2.5
FEATURE [Part::Cylinder] Cylinder802  label="Válec802"
  Angle = 360
  AttacherType = Attacher::AttachEngine3D
  Height = 20
  Placement = pos=(18.0312,18.0312,-4) rot=(0,0,-1;0.785398rad)
  Radius = 1.5
FEATURE [Part::Cylinder] Cylinder1814  label="Válec1814"
  Angle = 360
  AttacherType = Attacher::AttachEngine3D
  Height = 3
  Placement = pos=(-18.0312,-18.0312,3) rot=(0,0,1;2.35619rad)
  Radius = 3
FEATURE [Part::Cylinder] Cylinder803  label="Válec803"
  Angle = 360
  AttacherType = Attacher::AttachEngine3D
  Height = 3
  Placement = pos=(-18.0312,18.0312,3) rot=(0,0,1;0.785398rad)
  Radius = 3
FEATURE [Part::Cylinder] Cylinder1815  label="Válec1815"
  Angle = 360
  AttacherType = Attacher::AttachEngine3D
  Height = 3
  Placement = pos=(-25.5,-1e-15,3) rot=(0,0,1;1.5708rad)
  Radius = 3
FEATURE [Part::Compound] Compound004
  Links = -> [Cylinder795,Cylinder803,Cylinder1815,Cylinder1814,Cylinder1806,Cylinder1810,Cylinder1807,Cylinder1808]
FEATURE [Part::Cut] Cut002
  Base = -> Cylinder257
  Tool = -> Compound004
FEATURE [Part::Compound] Compound005
  Links = -> [Box005,Box007,Box006,Box008]
  Placement = pos=(0,0,-2) rot=(0,0,1;0rad)
FEATURE [Part::Compound] Compound006
  Links = -> [Cylinder1809,Cylinder1811,Cylinder1813,Cylinder1812]
  Placement = pos=(0,0,-2) rot=(0,0,1;0rad)
FEATURE [Part::Cut] Cut004
  Base = -> Compound005
  Tool = -> Compound006
FEATURE [Part::Chamfer] Chamfer069
  Base = -> Cut004
  Edges = 5 edges r=2: [Edge3,Edge12,Edge18,Edge27,Edge42]
FEATURE [Part::Chamfer] Chamfer070
  Base = -> Chamfer069
  Edges = 3 edges r=2: [Edge49,Edge63,Edge72]
FEATURE [Part::Chamfer] Chamfer008
  Base = -> Chamfer070
  Edges = 4 edges r=1: [Edge1,Edge29,Edge50,Edge71]
  Placement = pos=(0,0,-14) rot=(0,0,1;0rad)
FEATURE [Part::Compound] Compound003
  Links = -> [Cylinder794,Cylinder796,Cylinder797,Cylinder798,Cylinder799,Cylinder800,Cylinder801,Cylinder802]
FEATURE [Part::Cut] Cut003
  Base = -> Cut002
  Tool = -> Compound003
FEATURE [Part::Compound] Compound007  label="hornero_fix_armo"
  Links = -> [Cut003,Chamfer008]
  Placement = pos=(0,0,-46) rot=(0,0,1;0rad)
FEATURE [Part::FeaturePython] Tube003  # WARN: FeaturePython — macro-defined, semantics opaque (R4)
  AttacherType = Attacher::AttachEngine3D
  Height = 10
  InnerRadius = 22.5
  OuterRadius = 34
  Placement = pos=(0,0,-1) rot=(0,0,1;0rad)
FEATURE [Part::FeaturePython] Tube002  # WARN: FeaturePython — macro-defined, semantics opaque (R4)
  AttacherType = Attacher::AttachEngine3D
  Height = 1
  InnerRadius = 22.5
  OuterRadius = 28.5
  Placement = pos=(0,0,-2) rot=(0,0,1;0rad)
FEATURE [Part::Compound] Compound011
  Links = -> [Tube002,Tube003]
FEATURE [Part::Cylinder] Cylinder834  label="Válec834"
  Angle = 360
  AttacherType = Attacher::AttachEngine3D
  Height = 20
  Placement = pos=(18.0312,18.0312,-4) rot=(0,0,-1;0.785398rad)
  Radius = 1.5
FEATURE [Part::Cylinder] Cylinder837  label="Válec837"
  Angle = 360
  AttacherType = Attacher::AttachEngine3D
  Height = 20
  Placement = pos=(4e-15,-25.5,-4) rot=(0,0,1;3.14159rad)
  Radius = 1.5
FEATURE [Part::Cylinder] Cylinder831  label="Válec831"
  Angle = 360
  AttacherType = Attacher::AttachEngine3D
  Height = 20
  Placement = pos=(-18.0312,18.0312,-4) rot=(0,0,1;0.785398rad)
  Radius = 1.5
FEATURE [Part::Cylinder] Cylinder832  label="Válec832"
  Angle = 360
  AttacherType = Attacher::AttachEngine3D
  Height = 20
  Placement = pos=(-18.0312,-18.0312,-4) rot=(0,0,1;2.35619rad)
  Radius = 1.5
FEATURE [Part::Cylinder] Cylinder830  label="Válec830"
  Angle = 360
  AttacherType = Attacher::AttachEngine3D
  Height = 20
  Placement = pos=(0,25.5,-4) rot=(0,0,1;0rad)
  Radius = 1.5
FEATURE [Part::Cylinder] Cylinder836  label="Válec836"
  Angle = 360
  AttacherType = Attacher::AttachEngine3D
  Height = 20
  Placement = pos=(-25.5,-1e-15,-4) rot=(0,0,1;1.5708rad)
  Radius = 1.5
FEATURE [Part::Cylinder] Cylinder835  label="Válec835"
  Angle = 360
  AttacherType = Attacher::AttachEngine3D
  Height = 20
  Placement = pos=(25.5,1e-14,-4) rot=(0,0,-1;1.5708rad)
  Radius = 1.5
FEATURE [Part::Cylinder] Cylinder833  label="Válec833"
  Angle = 360
  AttacherType = Attacher::AttachEngine3D
  Height = 20
  Placement = pos=(18.0312,-18.0312,-4) rot=(0,0,1;3.92699rad)
  Radius = 1.5
FEATURE [Part::Compound] Compound010
  Links = -> [Cylinder830,Cylinder831,Cylinder836,Cylinder832,Cylinder837,Cylinder833,Cylinder835,Cylinder834]
FEATURE [Part::Cut] Cut006  label="hornero_fix_superpodloch"
  Base = -> Compound011
  Placement = pos=(0,0,-60) rot=(0,0,1;0rad)
  Tool = -> Compound010
FEATURE [Part::Cylinder] Cylinder1816  label="Válec1816"
  Angle = 360
  AttacherType = Attacher::AttachEngine3D
  Height = 20
  Placement = pos=(18,38,15) rot=(0,1,0;1.5708rad)
  Radius = 4
FEATURE [Part::Cylinder] Cylinder1817  label="Válec1817"
  Angle = 360
  AttacherType = Attacher::AttachEngine3D
  Height = 20
  Placement = pos=(-38,38,15) rot=(0,1,0;1.5708rad)
  Radius = 4
FEATURE [Part::Compound] Compound049
  Links = -> [Cylinder157,Cylinder159,Cylinder1816,Cylinder1817]
  Placement = pos=(0,4,0) rot=(0,0,1;0rad)
FEATURE [Part::Cut] Cut058
  Base = -> Cut057
  Tool = -> Compound049
FEATURE [Part::Cylinder] Cylinder1818  label="Válec1818"
  Angle = 360
  AttacherType = Attacher::AttachEngine3D
  Height = 20
  Placement = pos=(4,38,15) rot=(0,1,0;1.5708rad)
  Radius = 1.5
FEATURE [Part::Cylinder] Cylinder1819  label="Válec1819"
  Angle = 360
  AttacherType = Attacher::AttachEngine3D
  Height = 20
  Placement = pos=(-24,38,15) rot=(0,1,0;1.5708rad)
  Radius = 1.5
FEATURE [Part::Compound] Compound050
  Links = -> [Cylinder156,Cylinder158,Cylinder1818,Cylinder1819]
  Placement = pos=(0,4,0) rot=(0,0,1;0rad)
FEATURE [Part::Cut] Cut059
  Base = -> Cut058
  Tool = -> Compound050
FEATURE [Part::Compound] Compound051  label="G-midi_bearing-ring"
  Links = -> [Cut059,Cut055]
  Placement = pos=(0,0,-95) rot=(0,1,0;0rad)
FEATURE [Part::Box] Box719  label="Krychle719"
  AttacherType = Attacher::AttachEngine3D
  Height = 28
  Length = 44
  Placement = pos=(-22,20,-4) rot=(0,0,1;0rad)
  Width = 27
FEATURE [Part::Box] Box720  label="Krychle720"
  AttacherType = Attacher::AttachEngine3D
  Height = 27
  Length = 50
  Placement = pos=(-25,33,-4) rot=(0,0,1;0rad)
  Width = 14
FEATURE [Part::Cut] Cut533
  Base = -> Box720
  Tool = -> Box719
FEATURE [Part::Cylinder] Cylinder1820  label="Válec1820"
  Angle = 360
  AttacherType = Attacher::AttachEngine3D
  Height = 16
  Placement = pos=(18,42,1) rot=(0,1,0;1.5708rad)
  Radius = 4
FEATURE [Part::Cylinder] Cylinder1821  label="Válec1821"
  Angle = 360
  AttacherType = Attacher::AttachEngine3D
  Height = 16
  Placement = pos=(-34,42,1) rot=(0,1,0;1.5708rad)
  Radius = 4
FEATURE [Part::Cylinder] Cylinder1822  label="Válec1822"
  Angle = 360
  AttacherType = Attacher::AttachEngine3D
  Height = 16
  Placement = pos=(-34,42,17) rot=(0,1,0;1.5708rad)
  Radius = 4
FEATURE [Part::Cylinder] Cylinder1823  label="Válec1823"
  Angle = 360
  AttacherType = Attacher::AttachEngine3D
  Height = 16
  Placement = pos=(18,42,17) rot=(0,1,0;1.5708rad)
  Radius = 4
FEATURE [Part::Compound] Compound899
  Links = -> [Cylinder1821,Cylinder1823,Cylinder1820,Cylinder1822]
FEATURE [Part::Cut] Cut534
  Base = -> Cut533
  Tool = -> Compound899
FEATURE [Part::Chamfer] Chamfer071
  Base = -> Cut534
  Edges = 1 edges r=2.9: [Edge20]
FEATURE [Part::Chamfer] Chamfer072
  Base = -> Chamfer071
  Edges = 1 edges r=2.9: [Edge22]
FEATURE [Part::Box] Box721  label="Krychle721"
  AttacherType = Attacher::AttachEngine3D
  Height = 27
  Length = 3
  Placement = pos=(22,22,-4) rot=(0,0,1;0rad)
  Width = 14
FEATURE [Part::Cylinder] Cylinder1824  label="Válec1824"
  Angle = 360
  AttacherType = Attacher::AttachEngine3D
  Height = 32
  Placement = pos=(0,0,-4) rot=(0,0,1;0rad)
  Radius = 35
FEATURE [Part::Cut] Cut535
  Base = -> Box721
  Tool = -> Cylinder1824
FEATURE [Part::Compound] Compound896  label="G-midi_bear-hold-encoder-rear"
  Links = -> [Cut529,Compound889,Chamfer072,Cut535]
FEATURE [Mesh::Feature] Mesh001  label="G-midi_bear-hold-encoder-rear (Meshed)"
FEATURE [Part::Cylinder] Cylinder1825  label="Válec1825"
  Angle = 360
  AttacherType = Attacher::AttachEngine3D
  Height = 50
  Placement = pos=(0,0,-18.5) rot=(-0.357407,0.862856,0.357407;1.71775rad)
  Radius = 1.5
FEATURE [Part::Cylinder] Cylinder1826  label="Válec1826"
  Angle = 360
  AttacherType = Attacher::AttachEngine3D
  Height = 10
  Placement = pos=(14.8492,14.8492,-18.5) rot=(-0.357407,0.862856,0.357407;1.71777rad)
  Radius = 3
FEATURE [Part::Cylinder] Cylinder1827  label="Válec1827"
  Angle = 360
  AttacherType = Attacher::AttachEngine3D
  Height = 7
  Placement = pos=(0,0,-22) rot=(0,0,1;0rad)
  Radius = 24
FEATURE [Part::Box] Box722  label="Krychle722"
  AttacherType = Attacher::AttachEngine3D
  Height = 7
  Length = 1.4
  Placement = pos=(0,0,-22) rot=(0,0,1;0.099484rad)
  Width = 60
FEATURE [Part::Box] Box723  label="Krychle723"
  AttacherType = Attacher::AttachEngine3D
  Height = 100
  Length = 30.2
  Placement = pos=(0,-21.3546,-30) rot=(0,0,1;0.785398rad)
  Width = 30.2
FEATURE [Part::Cut] Cut542
  Base = -> Cylinder1827
  Tool = -> Box723
FEATURE [Part::Box] Box724  label="Krychle724"
  AttacherType = Attacher::AttachEngine3D
  Height = 7
  Length = 60
  Placement = pos=(-59.9909,-1.04714,-22) rot=(0,0,1;0.017453rad)
  Width = 60
FEATURE [Part::Cylinder] Cylinder1828  label="Válec1828"
  Angle = 360
  AttacherType = Attacher::AttachEngine3D
  Height = 7
  Placement = pos=(0,0,-22) rot=(0,0,1;0rad)
  Radius = 20
FEATURE [Part::Box] Box725  label="Krychle725"
  AttacherType = Attacher::AttachEngine3D
  Height = 7
  Length = 1.4
  Placement = pos=(0,0,-22) rot=(0,0,-1;0.05236rad)
  Width = 60
FEATURE [Part::Compound] Compound903
  Links = -> [Box725,Box722]
FEATURE [Part::Cut] Cut543
  Base = -> Compound903
  Placement = pos=(0,0,0) rot=(0,0,1;2.35445rad)
  Tool = -> Cylinder1828
FEATURE [Part::Box] Box726  label="Krychle726"
  AttacherType = Attacher::AttachEngine3D
  Height = 7
  Length = 120
  Placement = pos=(-60,-60,-22) rot=(0,0,-1;0rad)
  Width = 60
FEATURE [Part::Box] Box727  label="Krychle727"
  AttacherType = Attacher::AttachEngine3D
  Height = 7
  Length = 60
  Placement = pos=(0,0,-22) rot=(0,0,-1;0.349066rad)
  Width = 60
FEATURE [Part::Box] Box728  label="Krychle728"
  AttacherType = Attacher::AttachEngine3D
  Height = 7
  Length = 120
  Placement = pos=(-60,-60,-22) rot=(0,0,-1;0rad)
  Width = 60
FEATURE [Part::Box] Box729  label="Krychle729"
  AttacherType = Attacher::AttachEngine3D
  Height = 7
  Length = 60
  Placement = pos=(-56.3816,-20.5212,-22) rot=(0,0,1;0.349066rad)
  Width = 60
FEATURE [Part::Compound] Compound901
  Links = -> [Box727,Box729]
FEATURE [Part::Box] Box730  label="Krychle730"
  AttacherType = Attacher::AttachEngine3D
  Height = 7
  Length = 60
  Placement = pos=(0,0,-22) rot=(0,0,-1;0.034907rad)
  Width = 60
FEATURE [Part::Compound] Compound900
  Links = -> [Box730,Box724]
FEATURE [Part::FeaturePython] Tube091  # WARN: FeaturePython — macro-defined, semantics opaque (R4)
  AttacherType = Attacher::AttachEngine3D
  Height = 7
  InnerRadius = 20
  OuterRadius = 21.4
  Placement = pos=(0,0,-22) rot=(0,0,1;0rad)
FEATURE [Part::Cut] Cut544
  Base = -> Tube091
  Tool = -> Box728
FEATURE [Part::Cut] Cut539
  Base = -> Cut544
  Placement = pos=(0,0,-7) rot=(0,0,1;0rad)
  Tool = -> Compound900
FEATURE [Part::FeaturePython] Tube092  # WARN: FeaturePython — macro-defined, semantics opaque (R4)
  AttacherType = Attacher::AttachEngine3D
  Height = 7
  InnerRadius = 20
  OuterRadius = 21.4
  Placement = pos=(0,0,-22) rot=(0,0,1;0rad)
FEATURE [Part::Cut] Cut538
  Base = -> Tube092
  Tool = -> Box726
FEATURE [Part::Cut] Cut540
  Base = -> Cut538
  Placement = pos=(0,0,-7) rot=(0,0,1;0rad)
  Tool = -> Compound901
FEATURE [Part::Cut] Cut541
  Base = -> Cut540
  Placement = pos=(0,0,7) rot=(0,0,1;2.35619rad)
  Tool = -> Cut539
FEATURE [Part::Cylinder] Cylinder1829  label="Válec1829"
  Angle = 360
  AttacherType = Attacher::AttachEngine3D
  Height = 20
  Placement = pos=(14.1421,-14.1421,-30) rot=(0,0,-1;0.785398rad)
  Radius = 1.5
FEATURE [Part::Cylinder] Cylinder1830  label="Válec1830"
  Angle = 360
  AttacherType = Attacher::AttachEngine3D
  Height = 20
  Placement = pos=(-14.1421,14.1421,-30) rot=(0,0,1;2.35619rad)
  Radius = 1.5
FEATURE [Part::Compound] Compound902
  Links = -> [Cylinder1829,Cylinder1830]
FEATURE [Part::Cut] Cut537
  Base = -> Cut542
  Tool = -> Compound902
FEATURE [Part::Cut] Cut536
  Base = -> Cut537
  Tool = -> Cut541
FEATURE [Part::Cut] Cut545
  Base = -> Cut536
  Tool = -> Cut543
FEATURE [Part::Cut] Cut546
  Base = -> Cut545
  Tool = -> Cylinder1826
FEATURE [Part::Cut] Cut547
  Base = -> Cut546
  Tool = -> Cylinder1825
FEATURE [Part::Cylinder] Cylinder  label="Válec"
  Angle = 360
  AttacherType = Attacher::AttachEngine3D
  Height = 7
  Placement = pos=(0,0,-22) rot=(0,0,1;0rad)
  Radius = 24
FEATURE [Part::Box] Box  label="Krychle"
  AttacherType = Attacher::AttachEngine3D
  Height = 100
  Length = 30.2
  Placement = pos=(0,-21.3546,-30) rot=(0,0,1;0.785398rad)
  Width = 30.2
FEATURE [Part::Cut] Cut
  Base = -> Cylinder
  Tool = -> Box
FEATURE [Part::Cylinder] Cylinder810  label="Válec810"
  Angle = 360
  AttacherType = Attacher::AttachEngine3D
  Height = 20
  Placement = pos=(14.1421,-14.1421,-30) rot=(0,0,-1;0.785398rad)
  Radius = 1.5
FEATURE [Part::Cylinder] Cylinder811  label="Válec811"
  Angle = 360
  AttacherType = Attacher::AttachEngine3D
  Height = 20
  Placement = pos=(-14.1421,14.1421,-30) rot=(0,0,1;2.35619rad)
  Radius = 1.5
FEATURE [Part::Compound] Compound721
  Links = -> [Cylinder810,Cylinder811]
FEATURE [Part::Cut] Cut343
  Base = -> Cut
  Tool = -> Compound721
FEATURE [Part::Cut] Cut336
  Base = -> Cut334
  Placement = pos=(0,0,-7) rot=(0,0,1;0rad)
  Tool = -> Compound718
FEATURE [Part::Cut] Cut338
  Base = -> Cut337
  Placement = pos=(0,0,-7) rot=(0,0,1;0rad)
  Tool = -> Compound719
FEATURE [Part::Cut] Cut335
  Base = -> Cut336
  Placement = pos=(0,0,7) rot=(0,0,1;2.35619rad)
  Tool = -> Cut338
FEATURE [Part::Cut] Cut347
  Base = -> Cut343
  Tool = -> Cut335
FEATURE [Part::Compound] Compound720
  Links = -> [Box314,Box313]
FEATURE [Part::Cylinder] Cylinder804  label="Válec804"
  Angle = 360
  AttacherType = Attacher::AttachEngine3D
  Height = 7
  Placement = pos=(0,0,-22) rot=(0,0,1;0rad)
  Radius = 20
FEATURE [Part::Cut] Cut339
  Base = -> Compound720
  Placement = pos=(0,0,0) rot=(0,0,1;2.35445rad)
  Tool = -> Cylinder804
FEATURE [Part::Cut] Cut348
  Base = -> Cut347
  Tool = -> Cut339
FEATURE [Part::Compound] Compound898  label="G-midi_belt-wheel-rear-old"
  Links = -> [Cut344,Cut348,Cut547]
  Placement = pos=(0,0,54) rot=(0,0,1;0rad)
FEATURE [Part::Cylinder] Cylinder1831  label="Válec1831"
  Angle = 360
  AttacherType = Attacher::AttachEngine3D
  Height = 50
  Placement = pos=(0,0,-18.5) rot=(-0.357407,0.862856,0.357407;1.71775rad)
  Radius = 1.5
FEATURE [Part::Box] Box731  label="Krychle731"
  AttacherType = Attacher::AttachEngine3D
  Height = 7
  Length = 60
  Placement = pos=(0,0,-22) rot=(0,0,-1;0.349066rad)
  Width = 60
FEATURE [Part::Box] Box732  label="Krychle732"
  AttacherType = Attacher::AttachEngine3D
  Height = 7
  Length = 60
  Placement = pos=(-56.3816,-20.5212,-22) rot=(0,0,1;0.349066rad)
  Width = 60
FEATURE [Part::Cylinder] Cylinder1832  label="Válec1832"
  Angle = 360
  AttacherType = Attacher::AttachEngine3D
  Height = 7
  Placement = pos=(0,0,-22) rot=(0,0,1;0rad)
  Radius = 20
FEATURE [Part::Box] Box733  label="Krychle733"
  AttacherType = Attacher::AttachEngine3D
  Height = 7
  Length = 60
  Placement = pos=(0,0,-22) rot=(0,0,-1;0.034907rad)
  Width = 60
FEATURE [Part::Cylinder] Cylinder1833  label="Válec1833"
  Angle = 360
  AttacherType = Attacher::AttachEngine3D
  Height = 20
  Placement = pos=(14.1421,-14.1421,-30) rot=(0,0,-1;0.785398rad)
  Radius = 1.5
FEATURE [Part::Box] Box734  label="Krychle734"
  AttacherType = Attacher::AttachEngine3D
  Height = 7
  Length = 1.4
  Placement = pos=(0,0,-22) rot=(0,0,-1;0.05236rad)
  Width = 60
FEATURE [Part::Cylinder] Cylinder1834  label="Válec1834"
  Angle = 360
  AttacherType = Attacher::AttachEngine3D
  Height = 20
  Placement = pos=(-14.1421,14.1421,-30) rot=(0,0,1;2.35619rad)
  Radius = 1.5
FEATURE [Part::Box] Box735  label="Krychle735"
  AttacherType = Attacher::AttachEngine3D
  Height = 7
  Length = 1.4
  Placement = pos=(0,0,-22) rot=(0,0,1;0.099484rad)
  Width = 60
FEATURE [Part::Box] Box736  label="Krychle736"
  AttacherType = Attacher::AttachEngine3D
  Height = 100
  Length = 30.2
  Placement = pos=(0,-21.3546,-30) rot=(0,0,1;0.785398rad)
  Width = 30.2
FEATURE [Part::Cylinder] Cylinder1835  label="Válec1835"
  Angle = 360
  AttacherType = Attacher::AttachEngine3D
  Height = 10
  Placement = pos=(14.8492,14.8492,-18.5) rot=(-0.357407,0.862856,0.357407;1.71777rad)
  Radius = 3
FEATURE [Part::Cylinder] Cylinder1836  label="Válec1836"
  Angle = 360
  AttacherType = Attacher::AttachEngine3D
  Height = 7
  Placement = pos=(0,0,-22) rot=(0,0,1;0rad)
  Radius = 24
FEATURE [Part::Box] Box737  label="Krychle737"
  AttacherType = Attacher::AttachEngine3D
  Height = 7
  Length = 120
  Placement = pos=(-60,-60,-22) rot=(0,0,-1;0rad)
  Width = 60
FEATURE [Part::Box] Box738  label="Krychle738"
  AttacherType = Attacher::AttachEngine3D
  Height = 7
  Length = 60
  Placement = pos=(-59.9909,-1.04714,-22) rot=(0,0,1;0.017453rad)
  Width = 60
FEATURE [Part::Compound] Compound904
  Links = -> [Box733,Box738]
FEATURE [Part::Box] Box739  label="Krychle739"
  AttacherType = Attacher::AttachEngine3D
  Height = 7
  Length = 120
  Placement = pos=(-60,-60,-22) rot=(0,0,-1;0rad)
  Width = 60
FEATURE [Part::Cut] Cut553
  Base = -> Cylinder1836
  Tool = -> Box736
FEATURE [Part::Compound] Compound905
  Links = -> [Box734,Box735]
FEATURE [Part::Cut] Cut548
  Base = -> Compound905
  Placement = pos=(0,0,0) rot=(0,0,1;2.35445rad)
  Tool = -> Cylinder1832
FEATURE [Part::Compound] Compound906
  Links = -> [Cylinder1833,Cylinder1834]
FEATURE [Part::Cut] Cut558
  Base = -> Cut553
  Tool = -> Compound906
FEATURE [Part::Compound] Compound907
  Links = -> [Box731,Box732]
FEATURE [Part::FeaturePython] Tube093  # WARN: FeaturePython — macro-defined, semantics opaque (R4)
  AttacherType = Attacher::AttachEngine3D
  Height = 7
  InnerRadius = 20
  OuterRadius = 21.4
  Placement = pos=(0,0,-22) rot=(0,0,1;0rad)
FEATURE [Part::Cut] Cut559
  Base = -> Tube093
  Tool = -> Box737
FEATURE [Part::Cut] Cut556
  Base = -> Cut559
  Placement = pos=(0,0,-7) rot=(0,0,1;0rad)
  Tool = -> Compound907
FEATURE [Part::FeaturePython] Tube094  # WARN: FeaturePython — macro-defined, semantics opaque (R4)
  AttacherType = Attacher::AttachEngine3D
  Height = 7
  InnerRadius = 20
  OuterRadius = 21.4
  Placement = pos=(0,0,-22) rot=(0,0,1;0rad)
FEATURE [Part::Cut] Cut555
  Base = -> Tube094
  Tool = -> Box739
FEATURE [Part::Cut] Cut554
  Base = -> Cut555
  Placement = pos=(0,0,-7) rot=(0,0,1;0rad)
  Tool = -> Compound904
FEATURE [Part::Cut] Cut552
  Base = -> Cut556
  Placement = pos=(0,0,7) rot=(0,0,1;2.35619rad)
  Tool = -> Cut554
FEATURE [Part::Cut] Cut557
  Base = -> Cut558
  Tool = -> Cut552
FEATURE [Part::Cut] Cut549
  Base = -> Cut557
  Tool = -> Cut548
FEATURE [Part::Cut] Cut550
  Base = -> Cut549
  Tool = -> Cylinder1835
FEATURE [Part::Cut] Cut551
  Base = -> Cut550
  Tool = -> Cylinder1831
FEATURE [Part::Cylinder] Cylinder1837  label="Válec1837"
  Angle = 360
  AttacherType = Attacher::AttachEngine3D
  Height = 20
  Placement = pos=(14.1421,-14.1421,-30) rot=(0,0,-1;0.785398rad)
  Radius = 1.5
FEATURE [Part::Box] Box740  label="Krychle740"
  AttacherType = Attacher::AttachEngine3D
  Height = 20
  Length = 6
  Placement = pos=(9.89949,-14.1421,-30) rot=(0,0,-1;0.785398rad)
  Width = 6
FEATURE [Part::Cylinder] Cylinder1838  label="Válec1838"
  Angle = 360
  AttacherType = Attacher::AttachEngine3D
  Height = 3
  Placement = pos=(0,0,-25) rot=(0,0,1;0rad)
  Radius = 27
FEATURE [Part::Chamfer] Chamfer073
  Base = -> Cylinder1838
  Edges = 1 edges r=1: [Edge1]
FEATURE [Part::Box] Box741  label="Krychle741"
  AttacherType = Attacher::AttachEngine3D
  Height = 100
  Length = 30.2
  Placement = pos=(0,-21.3546,-30) rot=(0,0,1;0.785398rad)
  Width = 30.2
FEATURE [Part::Cut] Cut562
  Base = -> Chamfer073
  Tool = -> Box741
FEATURE [Part::Cylinder] Cylinder1839  label="Válec1839"
  Angle = 360
  AttacherType = Attacher::AttachEngine3D
  Height = 20
  Placement = pos=(-14.1421,14.1421,-30) rot=(0,0,1;2.35619rad)
  Radius = 1.5
FEATURE [Part::Compound] Compound909
  Links = -> [Cylinder1837,Cylinder1839]
FEATURE [Part::Cut] Cut560
  Base = -> Cut562
  Tool = -> Compound909
FEATURE [Part::Box] Box742  label="Krychle742"
  AttacherType = Attacher::AttachEngine3D
  Height = 20
  Length = 6
  Placement = pos=(-9.89949,14.1421,-30) rot=(0,0,1;2.35619rad)
  Width = 6
FEATURE [Part::Compound] Compound908
  Links = -> [Box742,Box740]
  Placement = pos=(0,0,-13) rot=(0,0,1;0rad)
FEATURE [Part::Cut] Cut561
  Base = -> Cut560
  Tool = -> Compound908
FEATURE [Part::Compound] Compound910  label="G-midi_belt-wheel-rear"
  Links = -> [Cut551,Cut561]
  Placement = pos=(0,0,54) rot=(0,0,1;0rad)
FEATURE [Mesh::Feature] Mesh002  label="G-midi_belt-wheel-rear (Meshed)"
FEATURE [Part::Cylinder] Cylinder890  label="Válec890"
  Angle = 360
  AttacherType = Attacher::AttachEngine3D
  Height = 15
  Placement = pos=(22.6274,-22.6274,0) rot=(0,0,1;3.92699rad)
  Radius = 1.5
FEATURE [Part::Cylinder] Cylinder889  label="Válec889"
  Angle = 360
  AttacherType = Attacher::AttachEngine3D
  Height = 15
  Placement = pos=(1e-14,-32,0) rot=(0,0,1;3.14159rad)
  Radius = 1.5
FEATURE [Part::Cylinder] Cylinder891  label="Válec891"
  Angle = 360
  AttacherType = Attacher::AttachEngine3D
  Height = 3
  Placement = pos=(-22.6274,-22.6274,4) rot=(0,0,1;2.35619rad)
  Radius = 3
FEATURE [Part::Cylinder] Cylinder895  label="Válec895"
  Angle = 360
  AttacherType = Attacher::AttachEngine3D
  Height = 3
  Placement = pos=(-32,0,4) rot=(0,0,1;1.5708rad)
  Radius = 3
FEATURE [Part::Cylinder] Cylinder897  label="Válec897"
  Angle = 360
  AttacherType = Attacher::AttachEngine3D
  Height = 15
  Placement = pos=(-32,0,0) rot=(0,0,1;1.5708rad)
  Radius = 1.5
FEATURE [Part::Cylinder] Cylinder899  label="Válec899"
  Angle = 360
  AttacherType = Attacher::AttachEngine3D
  Height = 3
  Placement = pos=(22.6274,22.6274,4) rot=(0,0,-1;0.785398rad)
  Radius = 3
FEATURE [Part::Cylinder] Cylinder898  label="Válec898"
  Angle = 360
  AttacherType = Attacher::AttachEngine3D
  Height = 3
  Placement = pos=(22.6274,-22.6274,4) rot=(0,0,1;3.92699rad)
  Radius = 3
FEATURE [Part::Cylinder] Cylinder892  label="Válec892"
  Angle = 360
  AttacherType = Attacher::AttachEngine3D
  Height = 15
  Placement = pos=(0,32,0) rot=(0,0,1;0rad)
  Radius = 1.5
FEATURE [Part::Cylinder] Cylinder896  label="Válec896"
  Angle = 360
  AttacherType = Attacher::AttachEngine3D
  Height = 3
  Placement = pos=(1e-14,-32,4) rot=(0,0,1;3.14159rad)
  Radius = 3
FEATURE [Part::Cylinder] Cylinder893  label="Válec893"
  Angle = 360
  AttacherType = Attacher::AttachEngine3D
  Height = 3
  Placement = pos=(0,32,4) rot=(0,0,1;0rad)
  Radius = 3
FEATURE [Part::Cylinder] Cylinder894  label="Válec894"
  Angle = 360
  AttacherType = Attacher::AttachEngine3D
  Height = 3
  Placement = pos=(-22.6274,22.6274,4) rot=(0,0,1;0.785398rad)
  Radius = 3
FEATURE [Part::FeaturePython] Tube095  # WARN: FeaturePython — macro-defined, semantics opaque (R4)
  AttacherType = Attacher::AttachEngine3D
  Height = 6
  InnerRadius = 29
  OuterRadius = 35
  Placement = pos=(0,0,4) rot=(0,0,1;0rad)
FEATURE [Part::Cylinder] Cylinder903  label="Válec903"
  Angle = 360
  AttacherType = Attacher::AttachEngine3D
  Height = 3
  Placement = pos=(32,1.1e-14,4) rot=(0,0,-1;1.5708rad)
  Radius = 3
FEATURE [Part::Compound] Compound566
  Links = -> [Cylinder893,Cylinder894,Cylinder895,Cylinder891,Cylinder896,Cylinder898,Cylinder903,Cylinder899]
FEATURE [Part::Cut] Cut371
  Base = -> Tube095
  Tool = -> Compound566
FEATURE [Part::Cylinder] Cylinder904  label="Válec904"
  Angle = 360
  AttacherType = Attacher::AttachEngine3D
  Height = 15
  Placement = pos=(-22.6274,-22.6274,0) rot=(0,0,1;2.35619rad)
  Radius = 1.5
FEATURE [Part::Box] Box340  label="Krychle340"
  AttacherType = Attacher::AttachEngine3D
  Height = 2
  Length = 6
  Placement = pos=(-3,23,-13) rot=(0,0,1;0rad)
  Width = 6
FEATURE [Part::Cylinder] Cylinder900  label="Válec900"
  Angle = 360
  AttacherType = Attacher::AttachEngine3D
  Height = 15
  Placement = pos=(-22.6274,22.6274,0) rot=(0,0,1;0.785398rad)
  Radius = 1.5
FEATURE [Part::Cylinder] Cylinder902  label="Válec902"
  Angle = 360
  AttacherType = Attacher::AttachEngine3D
  Height = 15
  Placement = pos=(32,1.1e-14,0) rot=(0,0,-1;1.5708rad)
  Radius = 1.5
FEATURE [Part::Cylinder] Cylinder905  label="Válec905"
  Angle = 360
  AttacherType = Attacher::AttachEngine3D
  Height = 15
  Placement = pos=(-18.3848,-18.3848,-20) rot=(0,0,1;2.35619rad)
  Radius = 1.5
FEATURE [Part::Cylinder] Cylinder906  label="Válec906"
  Angle = 360
  AttacherType = Attacher::AttachEngine3D
  Height = 15
  Placement = pos=(-26,-4e-15,-20) rot=(0,0,1;1.5708rad)
  Radius = 1.5
FEATURE [Part::Cylinder] Cylinder901  label="Válec901"
  Angle = 360
  AttacherType = Attacher::AttachEngine3D
  Height = 15
  Placement = pos=(22.6274,22.6274,0) rot=(0,0,-1;0.785398rad)
  Radius = 1.5
FEATURE [Part::Compound] Compound567
  Links = -> [Cylinder892,Cylinder900,Cylinder897,Cylinder904,Cylinder889,Cylinder890,Cylinder902,Cylinder901]
FEATURE [Part::Cut] Cut370
  Base = -> Cut371
  Placement = pos=(0,0,10) rot=(0,0,1;0rad)
  Tool = -> Compound567
FEATURE [Part::Cylinder] Cylinder910  label="Válec910"
  Angle = 360
  AttacherType = Attacher::AttachEngine3D
  Height = 15
  Placement = pos=(1.1e-14,-26,-20) rot=(0,0,1;3.14159rad)
  Radius = 1.5
FEATURE [Part::Cylinder] Cylinder908  label="Válec908"
  Angle = 360
  AttacherType = Attacher::AttachEngine3D
  Height = 15
  Placement = pos=(18.3848,18.3848,-20) rot=(0,0,-1;0.785398rad)
  Radius = 1.5
FEATURE [Part::Box] Box341  label="Krychle341"
  AttacherType = Attacher::AttachEngine3D
  Height = 2
  Length = 6
  Placement = pos=(-14.1421,-18.3848,-13) rot=(0,0,1;2.35619rad)
  Width = 6
FEATURE [Part::Cylinder] Cylinder907  label="Válec907"
  Angle = 360
  AttacherType = Attacher::AttachEngine3D
  Height = 15
  Placement = pos=(-18.3848,18.3848,-20) rot=(0,0,1;0.785398rad)
  Radius = 1.5
FEATURE [Part::Cylinder] Cylinder912  label="Válec912"
  Angle = 360
  AttacherType = Attacher::AttachEngine3D
  Height = 15
  Placement = pos=(26,1e-14,-20) rot=(0,0,-1;1.5708rad)
  Radius = 1.5
FEATURE [Part::Box] Box342  label="Krychle342"
  AttacherType = Attacher::AttachEngine3D
  Height = 2
  Length = 6
  Placement = pos=(-18.3848,14.1421,-13) rot=(0,0,1;0.785398rad)
  Width = 6
FEATURE [Part::Cylinder] Cylinder909  label="Válec909"
  Angle = 360
  AttacherType = Attacher::AttachEngine3D
  Height = 15
  Placement = pos=(0,26,-20) rot=(0,0,1;0rad)
  Radius = 1.5
FEATURE [Part::Cylinder] Cylinder911  label="Válec911"
  Angle = 360
  AttacherType = Attacher::AttachEngine3D
  Height = 15
  Placement = pos=(18.3848,-18.3848,-20) rot=(0,0,1;3.92699rad)
  Radius = 1.5
FEATURE [Part::Compound] Compound568
  Links = -> [Cylinder909,Cylinder907,Cylinder906,Cylinder905,Cylinder910,Cylinder911,Cylinder912,Cylinder908]
  Placement = pos=(0,0,0) rot=(0,0,1;0.392699rad)
FEATURE [Part::FeaturePython] Tube010  # WARN: FeaturePython — macro-defined, semantics opaque (R4)
  AttacherType = Attacher::AttachEngine3D
  Height = 6
  InnerRadius = 23
  OuterRadius = 29
  Placement = pos=(0,0,-16) rot=(0,0,1;0rad)
FEATURE [Part::Cut] Cut372
  Base = -> Tube010
  Tool = -> Compound568
FEATURE [Part::Box] Box346  label="Krychle346"
  AttacherType = Attacher::AttachEngine3D
  Height = 2
  Length = 6
  Placement = pos=(3,-23,-13) rot=(0,0,1;3.14159rad)
  Width = 6
FEATURE [Part::Box] Box343  label="Krychle343"
  AttacherType = Attacher::AttachEngine3D
  Height = 2
  Length = 6
  Placement = pos=(18.3848,-14.1421,-13) rot=(0,0,1;3.92699rad)
  Width = 6
FEATURE [Part::Box] Box344  label="Krychle344"
  AttacherType = Attacher::AttachEngine3D
  Height = 2
  Length = 6
  Placement = pos=(14.1421,18.3848,-13) rot=(0,0,-1;0.785398rad)
  Width = 6
FEATURE [Part::Box] Box345  label="Krychle345"
  AttacherType = Attacher::AttachEngine3D
  Height = 2
  Length = 6
  Placement = pos=(-23,-3,-13) rot=(0,0,1;1.5708rad)
  Width = 6
FEATURE [Part::Box] Box347  label="Krychle347"
  AttacherType = Attacher::AttachEngine3D
  Height = 2
  Length = 6
  Placement = pos=(23,3,-13) rot=(0,0,-1;1.5708rad)
  Width = 6
FEATURE [Part::Compound] Compound569
  Links = -> [Box342,Box345,Box341,Box346,Box343,Box347,Box344,Box340]
  Placement = pos=(0,0,0) rot=(0,0,1;0.392699rad)
FEATURE [Part::Cut] Cut373
  Base = -> Cut372
  Placement = pos=(0,0,10) rot=(0,0,1;0rad)
  Tool = -> Compound569
FEATURE [Part::Cylinder] Cylinder913  label="Válec913"
  Angle = 360
  AttacherType = Attacher::AttachEngine3D
  Height = 20
  Radius = 29
FEATURE [Part::FeaturePython] cycloidgear006  # WARN: FeaturePython — macro-defined, semantics opaque (R4)
  AttacherType = Attacher::AttachEngine3D
  Placement = pos=(0,0,-1) rot=(0,0,1;0rad)
  backlash = 0
  beta = 50
  clearance = 0.25
  double_helix = true
  height = 22
  inner_diameter = 5
  module = 1.32
  numpoints = 15
  outer_diameter = 5
  teeth = 33
  version = 0.0.3
FEATURE [Part::Cut] Cut374  label="G-midi_exp-ring-cyclo002"
  Base = -> Cylinder913
  Tool = -> cycloidgear006
FEATURE [Part::Compound] Compound570  label="G-midi_monoblock-cyclo"
  Links = -> [Cut370,Cut373,Cut374]
  Placement = pos=(0,0,-105) rot=(0,0,1;0rad)
FEATURE [Part::FeaturePython] Tube057  label="6001-2RS"  # WARN: FeaturePython — macro-defined, semantics opaque (R4)
  AttacherType = Attacher::AttachEngine3D
  Height = 8
  InnerRadius = 6
  OuterRadius = 14
  Placement = pos=(0,0,88) rot=(0,0,1;0rad)
FEATURE [Part::Cylinder] Cylinder826  label="Válec826"
  Angle = 360
  AttacherType = Attacher::AttachEngine3D
  Height = 5
  Placement = pos=(14.4,0,30) rot=(0,0,1;0rad)
  Radius = 5
FEATURE [Part::Cylinder] Cylinder828  label="Válec828"
  Angle = 360
  AttacherType = Attacher::AttachEngine3D
  Height = 5
  Placement = pos=(-7.2,-12.4708,30) rot=(0,0,1;4.18879rad)
  Radius = 5
FEATURE [Part::Cylinder] Cylinder1848  label="Válec1848"
  Angle = 360
  AttacherType = Attacher::AttachEngine3D
  Height = 3
  Placement = pos=(-14.5,0,35) rot=(0,0,1;3.14159rad)
  Radius = 3
FEATURE [Part::Cylinder] Cylinder1849  label="Válec1849"
  Angle = 360
  AttacherType = Attacher::AttachEngine3D
  Height = 20
  Placement = pos=(-14.5,0,25) rot=(0,0,1;3.14159rad)
  Radius = 1.5
FEATURE [Part::Cylinder] Cylinder1850  label="Válec1850"
  Angle = 360
  AttacherType = Attacher::AttachEngine3D
  Height = 3
  Placement = pos=(7.25,-12.5574,35) rot=(0,0,-1;1.0472rad)
  Radius = 3
FEATURE [Part::Cylinder] Cylinder829  label="Válec829"
  Angle = 360
  AttacherType = Attacher::AttachEngine3D
  Height = 6
  Placement = pos=(0,0,30) rot=(0,0,1;0rad)
  Radius = 8
FEATURE [Part::Cylinder] Cylinder1851  label="Válec1851"
  Angle = 360
  AttacherType = Attacher::AttachEngine3D
  Height = 20
  Placement = pos=(7.25,-12.5574,25) rot=(0,0,-1;1.0472rad)
  Radius = 1.5
FEATURE [Part::Cylinder] Cylinder1852  label="Válec1852"
  Angle = 360
  AttacherType = Attacher::AttachEngine3D
  Height = 20
  Placement = pos=(7.25,12.5574,25) rot=(0,0,1;1.0472rad)
  Radius = 1.5
FEATURE [Part::Cylinder] Cylinder1916  label="Válec1916"
  Angle = 360
  AttacherType = Attacher::AttachEngine3D
  Height = 8
  Placement = pos=(0,0,88) rot=(0,0,1;0rad)
  Radius = 6
FEATURE [Part::Cylinder] Cylinder1917  label="Válec1917"
  Angle = 360
  AttacherType = Attacher::AttachEngine3D
  Height = 3
  Placement = pos=(7.25,12.5574,35) rot=(0,0,1;1.0472rad)
  Radius = 3
FEATURE [Part::Cylinder] Cylinder827  label="Válec827"
  Angle = 360
  AttacherType = Attacher::AttachEngine3D
  Height = 5
  Placement = pos=(-7.2,12.4708,30) rot=(0,0,1;2.0944rad)
  Radius = 5
FEATURE [Part::Cylinder] Cylinder825  label="Válec825"
  Angle = 360
  AttacherType = Attacher::AttachEngine3D
  Height = 8
  Placement = pos=(0,0,30) rot=(0,0,1;0rad)
  Radius = 21
FEATURE [Part::FeaturePython] Tube048  # WARN: FeaturePython — macro-defined, semantics opaque (R4)
  AttacherType = Attacher::AttachEngine3D
  Height = 1
  InnerRadius = 4
  OuterRadius = 5
  Placement = pos=(-7.2,12.47,34) rot=(0,0,1;2.0944rad)
FEATURE [Part::FeaturePython] Tube049  # WARN: FeaturePython — macro-defined, semantics opaque (R4)
  AttacherType = Attacher::AttachEngine3D
  Height = 1
  InnerRadius = 4
  OuterRadius = 5
  Placement = pos=(-7.2,-12.47,34) rot=(0,0,1;4.18879rad)
FEATURE [Part::FeaturePython] Tube047  # WARN: FeaturePython — macro-defined, semantics opaque (R4)
  AttacherType = Attacher::AttachEngine3D
  Height = 1
  InnerRadius = 4
  OuterRadius = 5
  Placement = pos=(14.4,0,34) rot=(0,0,1;0rad)
FEATURE [Part::FeaturePython] Tube046  # WARN: FeaturePython — macro-defined, semantics opaque (R4)
  AttacherType = Attacher::AttachEngine3D
  Height = 1
  InnerRadius = 7
  OuterRadius = 8
  Placement = pos=(0,0,35) rot=(0,0,1;0rad)
FEATURE [Part::Compound] Compound913
  Links = -> [Cylinder1852,Cylinder1849,Cylinder1851]
FEATURE [Part::Cut] Cut329
  Base = -> Cylinder825
  Tool = -> Compound913
FEATURE [Part::Compound] Compound914
  Links = -> [Tube046,Tube047,Tube048,Tube049]
FEATURE [Part::Compound] Compound915
  Links = -> [Cylinder826,Cylinder827,Cylinder828,Cylinder829]
FEATURE [Part::Compound] Compound916
  Links = -> [Cylinder1850,Cylinder1917,Cylinder1848]
FEATURE [Part::Cut] Cut330
  Base = -> Cut329
  Tool = -> Compound916
FEATURE [Part::Cut] Cut331
  Base = -> Cut330
  Tool = -> Compound915
FEATURE [Part::Compound] Compound554  label="G-midi_quikovina1"
  Links = -> [Compound914,Cut331]
  Placement = pos=(0,0,50) rot=(0,0,1;0rad)
FEATURE [Part::FeaturePython] Tube061  # WARN: FeaturePython — macro-defined, semantics opaque (R4)
  AttacherType = Attacher::AttachEngine3D
  Height = 1
  InnerRadius = 6
  OuterRadius = 8
  Placement = pos=(0,0,88) rot=(0,0,1;0rad)
FEATURE [Part::Chamfer] Chamfer010
  Base = -> Cylinder1916
  Edges = 1 edges r=1: [Edge1]
FEATURE [Part::Chamfer] Chamfer011
  Base = -> Compound554
  Edges = 1 edges r=1: [Edge25]
FEATURE [Part::Compound] Compound608  label="G-midi_quikovina"
  Links = -> [Chamfer010,Chamfer011,Tube061]
FEATURE [Part::FeaturePython] Tube098  # WARN: FeaturePython — macro-defined, semantics opaque (R4)
  AttacherType = Attacher::AttachEngine3D
  Height = 2
  InnerRadius = 22.5
  OuterRadius = 34
  Placement = pos=(0,0,100) rot=(0,0,1;0rad)
FEATURE [Part::Box] Box743  label="Krychle743"
  AttacherType = Attacher::AttachEngine3D
  Height = 25
  Length = 30.2
  Placement = pos=(-15.1,-15.1,0) rot=(0,0,1;0rad)
  Width = 30.2
FEATURE [Part::Cylinder] Cylinder1927  label="Válec1927"
  Angle = 360
  AttacherType = Attacher::AttachEngine3D
  Height = 20
  Placement = pos=(-25.5,-1e-15,-4) rot=(0,0,1;1.5708rad)
  Radius = 1.5
FEATURE [Part::Cylinder] Cylinder1928  label="Válec1928"
  Angle = 360
  AttacherType = Attacher::AttachEngine3D
  Height = 20
  Placement = pos=(25.5,1e-14,-4) rot=(0,0,-1;1.5708rad)
  Radius = 1.5
FEATURE [Part::Cylinder] Cylinder1929  label="Válec1929"
  Angle = 360
  AttacherType = Attacher::AttachEngine3D
  Height = 20
  Placement = pos=(4e-15,-25.5,-4) rot=(0,0,1;3.14159rad)
  Radius = 1.5
FEATURE [Part::Cylinder] Cylinder1930  label="Válec1930"
  Angle = 360
  AttacherType = Attacher::AttachEngine3D
  Height = 20
  Placement = pos=(-18.0312,18.0312,-4) rot=(0,0,1;0.785398rad)
  Radius = 1.5
FEATURE [Part::Cylinder] Cylinder1931  label="Válec1931"
  Angle = 360
  AttacherType = Attacher::AttachEngine3D
  Height = 3
  Placement = pos=(18.0312,18.0312,3) rot=(0,0,-1;0.785398rad)
  Radius = 3
FEATURE [Part::Cylinder] Cylinder1932  label="Válec1932"
  Angle = 360
  AttacherType = Attacher::AttachEngine3D
  Height = 3
  Placement = pos=(18.0312,-18.0312,3) rot=(0,0,1;3.92699rad)
  Radius = 3
FEATURE [Part::Cylinder] Cylinder1933  label="Válec1933"
  Angle = 360
  AttacherType = Attacher::AttachEngine3D
  Height = 20
  Placement = pos=(-18.0312,-18.0312,-4) rot=(0,0,1;2.35619rad)
  Radius = 1.5
FEATURE [Part::Cylinder] Cylinder1934  label="Válec1934"
  Angle = 360
  AttacherType = Attacher::AttachEngine3D
  Height = 3
  Placement = pos=(0,25.5,3) rot=(0,0,1;0rad)
  Radius = 3
FEATURE [Part::Cylinder] Cylinder1935  label="Válec1935"
  Angle = 360
  AttacherType = Attacher::AttachEngine3D
  Height = 20
  Placement = pos=(18.0312,-18.0312,-4) rot=(0,0,1;3.92699rad)
  Radius = 1.5
FEATURE [Part::Cylinder] Cylinder1936  label="Válec1936"
  Angle = 360
  AttacherType = Attacher::AttachEngine3D
  Height = 6
  Radius = 34
FEATURE [Part::Cylinder] Cylinder1937  label="Válec1937"
  Angle = 360
  AttacherType = Attacher::AttachEngine3D
  Height = 20
  Placement = pos=(0,25.5,-4) rot=(0,0,1;0rad)
  Radius = 1.5
FEATURE [Part::Cylinder] Cylinder1938  label="Válec1938"
  Angle = 360
  AttacherType = Attacher::AttachEngine3D
  Height = 3
  Placement = pos=(25.5,1e-14,3) rot=(0,0,-1;1.5708rad)
  Radius = 3
FEATURE [Part::Cylinder] Cylinder1939  label="Válec1939"
  Angle = 360
  AttacherType = Attacher::AttachEngine3D
  Height = 3
  Placement = pos=(4e-15,-25.5,3) rot=(0,0,1;3.14159rad)
  Radius = 3
FEATURE [Part::Cylinder] Cylinder1940  label="Válec1940"
  Angle = 360
  AttacherType = Attacher::AttachEngine3D
  Height = 3
  Placement = pos=(-18.0312,18.0312,3) rot=(0,0,1;0.785398rad)
  Radius = 3
FEATURE [Part::Cylinder] Cylinder1941  label="Válec1941"
  Angle = 360
  AttacherType = Attacher::AttachEngine3D
  Height = 3
  Placement = pos=(-18.0312,-18.0312,3) rot=(0,0,1;2.35619rad)
  Radius = 3
FEATURE [Part::Cylinder] Cylinder1942  label="Válec1942"
  Angle = 360
  AttacherType = Attacher::AttachEngine3D
  Height = 3
  Placement = pos=(-25.5,-1e-15,3) rot=(0,0,1;1.5708rad)
  Radius = 3
FEATURE [Part::Compound] Compound918
  Links = -> [Cylinder1934,Cylinder1940,Cylinder1942,Cylinder1941,Cylinder1939,Cylinder1932,Cylinder1938,Cylinder1931]
FEATURE [Part::Cut] Cut565
  Base = -> Cylinder1936
  Tool = -> Compound918
FEATURE [Part::Cylinder] Cylinder1943  label="Válec1943"
  Angle = 360
  AttacherType = Attacher::AttachEngine3D
  Height = 20
  Placement = pos=(18.0312,18.0312,-4) rot=(0,0,-1;0.785398rad)
  Radius = 1.5
FEATURE [Part::Compound] Compound919
  Links = -> [Cylinder1937,Cylinder1930,Cylinder1927,Cylinder1933,Cylinder1929,Cylinder1935,Cylinder1928,Cylinder1943]
FEATURE [Part::Cut] Cut566
  Base = -> Cut565
  Tool = -> Compound919
FEATURE [Part::Box] Box744  label="Krychle744"
  AttacherType = Attacher::AttachEngine3D
  Height = 20
  Length = 20
  Placement = pos=(-10,15.1,20) rot=(0,0,1;0rad)
  Width = 3
FEATURE [Part::Box] Box745  label="Krychle745"
  AttacherType = Attacher::AttachEngine3D
  Height = 20
  Length = 20
  Placement = pos=(15.1,10,20) rot=(0,0,-1;1.5708rad)
  Width = 3
FEATURE [Part::Cylinder] Cylinder1944  label="Válec1944"
  Angle = 360
  AttacherType = Attacher::AttachEngine3D
  Height = 10
  Placement = pos=(12,6e-15,30) rot=(0.57735,0.57735,0.57735;2.0944rad)
  Radius = 2.5
FEATURE [Part::Box] Box746  label="Krychle746"
  AttacherType = Attacher::AttachEngine3D
  Height = 20
  Length = 20
  Placement = pos=(10,-15.1,20) rot=(0,0,1;3.14159rad)
  Width = 3
FEATURE [Part::Box] Box747  label="Krychle747"
  AttacherType = Attacher::AttachEngine3D
  Height = 20
  Length = 20
  Placement = pos=(-15.1,-10,20) rot=(0,0,1;1.5708rad)
  Width = 3
FEATURE [Part::Compound] Compound920
  Links = -> [Box744,Box747,Box746,Box745]
  Placement = pos=(0,0,-2) rot=(0,0,1;0rad)
FEATURE [Part::Cylinder] Cylinder1945  label="Válec1945"
  Angle = 360
  AttacherType = Attacher::AttachEngine3D
  Height = 10
  Placement = pos=(0,-12,30) rot=(1,0,0;1.5708rad)
  Radius = 2.5
FEATURE [Part::Cylinder] Cylinder1946  label="Válec1946"
  Angle = 360
  AttacherType = Attacher::AttachEngine3D
  Height = 10
  Placement = pos=(-1.5e-14,12,30) rot=(0,0.707107,0.707107;3.14159rad)
  Radius = 2.5
FEATURE [Part::Cylinder] Cylinder1947  label="Válec1947"
  Angle = 360
  AttacherType = Attacher::AttachEngine3D
  Height = 10
  Placement = pos=(-12,-2.4e-14,30) rot=(-0.57735,0.57735,0.57735;4.18879rad)
  Radius = 2.5
FEATURE [Part::Compound] Compound921
  Links = -> [Cylinder1945,Cylinder1944,Cylinder1946,Cylinder1947]
  Placement = pos=(0,0,-2) rot=(0,0,1;0rad)
FEATURE [Part::Cut] Cut567
  Base = -> Compound920
  Tool = -> Compound921
FEATURE [Part::Chamfer] Chamfer075
  Base = -> Cut567
  Edges = 5 edges r=2: [Edge3,Edge12,Edge18,Edge27,Edge42]
FEATURE [Part::Chamfer] Chamfer077
  Base = -> Chamfer075
  Edges = 3 edges r=2: [Edge49,Edge63,Edge72]
FEATURE [Part::Chamfer] Chamfer076
  Base = -> Chamfer077
  Edges = 4 edges r=1: [Edge1,Edge29,Edge50,Edge71]
  Placement = pos=(0,0,-14) rot=(0,0,1;0rad)
FEATURE [Part::Cut] Cut568
  Base = -> Cut566
  Tool = -> Box743
FEATURE [Part::Chamfer] Chamfer078
  Base = -> Cut568
  Edges = 4 edges r=0.5: [Edge20,Edge21,Edge22,Edge23]
FEATURE [Part::Compound] Compound922  label="G-midi_arm-rotator"
  Links = -> [Chamfer076,Chamfer078]
  Placement = pos=(0,0,-44) rot=(0,0,1;0rad)
FEATURE [Part::Box] Box115  label="Krychle115"
  AttacherType = Attacher::AttachEngine3D
  Height = 3
  Length = 10
  Placement = pos=(58,2,27) rot=(0,0,1;0rad)
  Width = 28
FEATURE [Part::Cylinder] Cylinder1948  label="Válec1948"
  Angle = 360
  AttacherType = Attacher::AttachEngine3D
  Height = 36
  Placement = pos=(0,0,19) rot=(0,0,1;0rad)
  Radius = 25
FEATURE [Part::Cylinder] Cylinder258  label="Válec258"
  Angle = 360
  AttacherType = Attacher::AttachEngine3D
  Height = 40
  Placement = pos=(-20,42,29) rot=(0,1,0;1.5708rad)
  Radius = 1.5
FEATURE [Part::Box] Box114  label="Krychle114"
  AttacherType = Attacher::AttachEngine3D
  Height = 3
  Length = 10
  Placement = pos=(58,2,4) rot=(0,0,1;0rad)
  Width = 28
FEATURE [Part::Box] Box106  label="Krychle106"
  AttacherType = Attacher::AttachEngine3D
  Height = 36
  Length = 20
  Placement = pos=(-10,20,19) rot=(0,0,1;0rad)
  Width = 27
FEATURE [Part::Cylinder] Cylinder1949  label="Válec1949"
  Angle = 360
  AttacherType = Attacher::AttachEngine3D
  Height = 40
  Placement = pos=(-20,42,-54) rot=(0,1,0;1.5708rad)
  Radius = 1.5
FEATURE [Part::Box] Box105  label="Krychle105"
  AttacherType = Attacher::AttachEngine3D
  Height = 33
  Length = 26
  Placement = pos=(-13,15,19) rot=(0,0,1;0rad)
  Width = 32
FEATURE [Part::Cut] Cut569
  Base = -> Box105
  Tool = -> Box106
FEATURE [Part::Box] Box108  label="Krychle108"
  AttacherType = Attacher::AttachEngine3D
  Height = 34
  Length = 20
  Placement = pos=(-10,20,19) rot=(0,0,1;0rad)
  Width = 25
FEATURE [Part::Box] Box116  label="Krychle116"
  AttacherType = Attacher::AttachEngine3D
  Height = 34
  Length = 20
  Placement = pos=(-10,20,19) rot=(0,0,1;0rad)
  Width = 25
FEATURE [Part::Cylinder] Cylinder259  label="Válec259"
  Angle = 360
  AttacherType = Attacher::AttachEngine3D
  Height = 40
  Placement = pos=(-20,42,42) rot=(0,1,0;1.5708rad)
  Radius = 1.5
FEATURE [Part::Cut] Cut571
  Base = -> Cut569
  Tool = -> Cylinder1948
FEATURE [Part::Compound] Compound925
  Links = -> [Box114,Box115]
  Placement = pos=(-17,-21,50) rot=(0.57735,0.57735,0.57735;2.0944rad)
FEATURE [Part::Compound] Compound565
  Links = -> [Cylinder258,Cylinder259]
FEATURE [Part::Cut] Cut572
  Base = -> Cut571
  Tool = -> Compound565
FEATURE [Part::FeaturePython] Tube021  # WARN: FeaturePython — macro-defined, semantics opaque (R4)
  AttacherType = Attacher::AttachEngine3D
  Height = 4
  InnerRadius = 25
  OuterRadius = 29
  Placement = pos=(0,0,29) rot=(0,0,1;0rad)
FEATURE [Part::Cut] Cut573
  Base = -> Tube021
  Tool = -> Box116
FEATURE [Part::FeaturePython] Tube019  # WARN: FeaturePython — macro-defined, semantics opaque (R4)
  AttacherType = Attacher::AttachEngine3D
  Height = 33
  InnerRadius = 25
  OuterRadius = 27
  Placement = pos=(0,0,19) rot=(0,0,1;0rad)
FEATURE [Part::Cut] Cut570
  Base = -> Tube019
  Tool = -> Box108
FEATURE [Part::Compound] Compound924
  Links = -> [Cut572,Cut570]
FEATURE [Part::Compound] Compound571  label="adapto_midi_kryto1"
  Links = -> [Compound924,Compound925]
  Placement = pos=(0,0,10) rot=(0,0,1;0rad)
FEATURE [Part::Compound] Compound574  label="adapto_midi_kryto"
  Links = -> [Compound571,Cut573]
  Placement = pos=(0,0,25) rot=(0,1,0;3.14159rad)
FEATURE [Part::Cut] Cut574  label="G-midi_extrusion-cover-subshift"
  Base = -> Compound574
  Tool = -> Cylinder1949
FEATURE [Mesh::Feature] Mesh004  label="G-midi_rotator-fix (Meshed)"
FEATURE [Mesh::Feature] Mesh007  label="G-midi_rotator-fix (Meshed)001"
FEATURE [Part::Torus] Torus003  label="Anuloid003"
  Angle1 = -180
  Angle2 = 180
  Angle3 = 360
  AttacherType = Attacher::AttachEngine3D
  Placement = pos=(0,0,20.5) rot=(0,0,1;0rad)
  Radius1 = 28
  Radius2 = 2.2
FEATURE [Part::Cylinder] Cylinder1950  label="Válec1950"
  Angle = 360
  AttacherType = Attacher::AttachEngine3D
  Height = 10
  Placement = pos=(22.6274,22.6274,10) rot=(0,0,-1;0.785398rad)
  Radius = 1.5
FEATURE [Part::Cylinder] Cylinder1951  label="Válec1951"
  Angle = 360
  AttacherType = Attacher::AttachEngine3D
  Height = 20
  Placement = pos=(4,38,25) rot=(0,1,0;1.5708rad)
  Radius = 1.5
FEATURE [Part::Box] Box748  label="Krychle748"
  AttacherType = Attacher::AttachEngine3D
  Height = 20
  Length = 20.4
  Placement = pos=(-10.2,20,10) rot=(0,0,1;0rad)
  Width = 27
FEATURE [Part::Cylinder] Cylinder1952  label="Válec1952"
  Angle = 360
  AttacherType = Attacher::AttachEngine3D
  Height = 10
  Placement = pos=(22.6274,-22.6274,10) rot=(0,0,1;3.92699rad)
  Radius = 1.5
FEATURE [Part::Cylinder] Cylinder1953  label="Válec1953"
  Angle = 360
  AttacherType = Attacher::AttachEngine3D
  Height = 20
  Placement = pos=(18,38,25) rot=(0,1,0;1.5708rad)
  Radius = 4
FEATURE [Part::Box] Box749  label="Krychle749"
  AttacherType = Attacher::AttachEngine3D
  Height = 2
  Length = 6
  Placement = pos=(-22.6274,18.3848,14) rot=(0,0,1;0.785398rad)
  Width = 6
FEATURE [Part::Cylinder] Cylinder1954  label="Válec1954"
  Angle = 360
  AttacherType = Attacher::AttachEngine3D
  Height = 10
  Placement = pos=(1e-14,-32,10) rot=(0,0,1;3.14159rad)
  Radius = 1.5
FEATURE [Part::Cylinder] Cylinder1955  label="Válec1955"
  Angle = 360
  AttacherType = Attacher::AttachEngine3D
  Height = 10
  Placement = pos=(32,1.1e-14,10) rot=(0,0,-1;1.5708rad)
  Radius = 1.5
FEATURE [Part::Box] Box750  label="Krychle750"
  AttacherType = Attacher::AttachEngine3D
  Height = 2
  Length = 6
  Placement = pos=(22.6274,-18.3848,14) rot=(0,0,1;3.92699rad)
  Width = 6
FEATURE [Part::Cylinder] Cylinder1956  label="Válec1956"
  Angle = 360
  AttacherType = Attacher::AttachEngine3D
  Height = 10
  Placement = pos=(28,0,20.5) rot=(0,0,1;0rad)
  Radius = 2.2
FEATURE [Part::Box] Box751  label="Krychle751"
  AttacherType = Attacher::AttachEngine3D
  Height = 2
  Length = 6
  Placement = pos=(29,3,14) rot=(0,0,-1;1.5708rad)
  Width = 6
FEATURE [Part::Box] Box752  label="Krychle752"
  AttacherType = Attacher::AttachEngine3D
  Height = 2
  Length = 6
  Placement = pos=(18.3848,22.6274,14) rot=(0,0,-1;0.785398rad)
  Width = 6
FEATURE [Part::Cylinder] Cylinder1957  label="Válec1957"
  Angle = 360
  AttacherType = Attacher::AttachEngine3D
  Height = 20
  Placement = pos=(-38,38,25) rot=(0,1,0;1.5708rad)
  Radius = 4
FEATURE [Part::Cylinder] Cylinder1958  label="Válec1958"
  Angle = 360
  AttacherType = Attacher::AttachEngine3D
  Height = 20
  Placement = pos=(-24,38,25) rot=(0,1,0;1.5708rad)
  Radius = 1.5
FEATURE [Part::Box] Box753  label="Krychle753"
  AttacherType = Attacher::AttachEngine3D
  Height = 2
  Length = 6
  Placement = pos=(3,-29,14) rot=(0,0,1;3.14159rad)
  Width = 6
FEATURE [Part::Box] Box754  label="Krychle754"
  AttacherType = Attacher::AttachEngine3D
  Height = 2
  Length = 6
  Placement = pos=(-29,-3,14) rot=(0,0,1;1.5708rad)
  Width = 6
FEATURE [Part::Box] Box755  label="Krychle755"
  AttacherType = Attacher::AttachEngine3D
  Height = 20
  Length = 50
  Placement = pos=(-25,15,10) rot=(0,0,1;0rad)
  Width = 32
FEATURE [Part::Cylinder] Cylinder1959  label="Válec1959"
  Angle = 360
  AttacherType = Attacher::AttachEngine3D
  Height = 20
  Placement = pos=(0,0,10) rot=(0,0,1;0rad)
  Radius = 35
FEATURE [Part::Cut] Cut577
  Base = -> Box755
  Tool = -> Cylinder1959
FEATURE [Part::Cut] Cut578
  Base = -> Cut577
  Tool = -> Box748
FEATURE [Part::Cylinder] Cylinder1960  label="Válec1960"
  Angle = 360
  AttacherType = Attacher::AttachEngine3D
  Height = 10
  Placement = pos=(0,32,10) rot=(0,0,1;0rad)
  Radius = 1.5
FEATURE [Part::Box] Box756  label="Krychle756"
  AttacherType = Attacher::AttachEngine3D
  Height = 2
  Length = 6
  Placement = pos=(-18.3848,-22.6274,14) rot=(0,0,1;2.35619rad)
  Width = 6
FEATURE [Part::Cylinder] Cylinder1961  label="Válec1961"
  Angle = 360
  AttacherType = Attacher::AttachEngine3D
  Height = 10
  Placement = pos=(-22.6274,22.6274,10) rot=(0,0,1;0.785398rad)
  Radius = 1.5
FEATURE [Part::Box] Box757  label="Krychle757"
  AttacherType = Attacher::AttachEngine3D
  Height = 2
  Length = 6
  Placement = pos=(-3,29,14) rot=(0,0,1;0rad)
  Width = 6
FEATURE [Part::Compound] Compound927
  Links = -> [Box749,Box754,Box756,Box753,Box750,Box751,Box752,Box757]
FEATURE [Part::Cylinder] Cylinder1962  label="Válec1962"
  Angle = 360
  AttacherType = Attacher::AttachEngine3D
  Height = 10
  Placement = pos=(-22.6274,-22.6274,10) rot=(0,0,1;2.35619rad)
  Radius = 1.5
FEATURE [Part::Cylinder] Cylinder1963  label="Válec1963"
  Angle = 360
  AttacherType = Attacher::AttachEngine3D
  Height = 10
  Placement = pos=(-32,0,10) rot=(0,0,1;1.5708rad)
  Radius = 1.5
FEATURE [Part::FeaturePython] Tube101  # WARN: FeaturePython — macro-defined, semantics opaque (R4)
  AttacherType = Attacher::AttachEngine3D
  Height = 20
  InnerRadius = 29
  OuterRadius = 35
  Placement = pos=(0,0,10) rot=(0,0,1;0rad)
FEATURE [Part::Cut] Cut580
  Base = -> Tube101
  Tool = -> Torus003
FEATURE [Part::Cut] Cut582
  Base = -> Cut580
  Tool = -> Cylinder1956
FEATURE [Part::Compound] Compound929
  Links = -> [Cylinder1961,Cylinder1963,Cylinder1962,Cylinder1954,Cylinder1952,Cylinder1955,Cylinder1950,Cylinder1960]
FEATURE [Part::Cut] Cut579
  Base = -> Cut582
  Tool = -> Compound929
FEATURE [Part::Cut] Cut575  label="gearovina-midi_loziskovina002"
  Base = -> Cut579
  Tool = -> Compound927
FEATURE [Part::Cylinder] Cylinder1964  label="Válec1964"
  Angle = 360
  AttacherType = Attacher::AttachEngine3D
  Height = 20
  Placement = pos=(-38,38,15) rot=(0,1,0;1.5708rad)
  Radius = 4
FEATURE [Part::Cylinder] Cylinder1965  label="Válec1965"
  Angle = 360
  AttacherType = Attacher::AttachEngine3D
  Height = 20
  Placement = pos=(4,38,15) rot=(0,1,0;1.5708rad)
  Radius = 1.5
FEATURE [Part::Cylinder] Cylinder1966  label="Válec1966"
  Angle = 360
  AttacherType = Attacher::AttachEngine3D
  Height = 20
  Placement = pos=(-24,38,15) rot=(0,1,0;1.5708rad)
  Radius = 1.5
FEATURE [Part::Compound] Compound930
  Links = -> [Cylinder1951,Cylinder1958,Cylinder1965,Cylinder1966]
  Placement = pos=(0,4,0) rot=(0,0,1;0rad)
FEATURE [Part::Cylinder] Cylinder1967  label="Válec1967"
  Angle = 360
  AttacherType = Attacher::AttachEngine3D
  Height = 20
  Placement = pos=(18,38,15) rot=(0,1,0;1.5708rad)
  Radius = 4
FEATURE [Part::Compound] Compound928
  Links = -> [Cylinder1953,Cylinder1957,Cylinder1967,Cylinder1964]
  Placement = pos=(0,4,0) rot=(0,0,1;0rad)
FEATURE [Part::Cut] Cut581
  Base = -> Cut578
  Tool = -> Compound928
FEATURE [Part::Cut] Cut576
  Base = -> Cut581
  Tool = -> Compound930
FEATURE [Part::Compound] Compound926  label="G-midi_bearing-ring-centric"
  Links = -> [Cut576,Cut575]
  Placement = pos=(0,0,-95) rot=(0,1,0;0rad)
FEATURE [Part::Box] Box198  label="Krychle198"
  AttacherType = Attacher::AttachEngine3D
  Height = 2
  Length = 16
  Placement = pos=(60,-41,16) rot=(0,0,1;0rad)
  Width = 6
FEATURE [Part::Box] Box201  label="Krychle201"
  AttacherType = Attacher::AttachEngine3D
  Height = 20
  Length = 10
  Placement = pos=(97,-29,7) rot=(0,0,1;0rad)
  Width = 108
FEATURE [Part::Box] Box204  label="Krychle204"
  AttacherType = Attacher::AttachEngine3D
  Height = 2
  Length = 16
  Placement = pos=(60,-41,10) rot=(0,0,1;0rad)
  Width = 6
FEATURE [Part::Box] Box209  label="Krychle209"
  AttacherType = Attacher::AttachEngine3D
  Height = 2
  Length = 16
  Placement = pos=(60,-51,10) rot=(0,0,1;0rad)
  Width = 6
FEATURE [Part::Box] Box205  label="Krychle205"
  AttacherType = Attacher::AttachEngine3D
  Height = 2
  Length = 16
  Placement = pos=(60,-51,16) rot=(0,0,1;0rad)
  Width = 6
FEATURE [Part::Box] Box202  label="Krychle202"
  AttacherType = Attacher::AttachEngine3D
  Height = 2
  Length = 16
  Placement = pos=(60,2,16) rot=(0,0,1;0rad)
  Width = 6
FEATURE [Part::Box] Box211  label="Krychle211"
  AttacherType = Attacher::AttachEngine3D
  Height = 2
  Length = 16
  Placement = pos=(60,46,16) rot=(0,0,1;0rad)
  Width = 6
FEATURE [Part::Cylinder] Cylinder461  label="Válec461"
  Angle = 360
  AttacherType = Attacher::AttachEngine3D
  Height = 100
  Placement = pos=(24,-36,34) rot=(0,1,0;1.5708rad)
  Radius = 5
FEATURE [Part::Cylinder] Cylinder467  label="Válec467"
  Angle = 360
  AttacherType = Attacher::AttachEngine3D
  Height = 50
  Placement = pos=(63,-38,-12) rot=(0,0,1;0rad)
  Radius = 1.5
FEATURE [Part::Cylinder] Cylinder474  label="Válec474"
  Angle = 360
  AttacherType = Attacher::AttachEngine3D
  Height = 100
  Placement = pos=(24,51,25) rot=(0,1,0;1.5708rad)
  Radius = 5
FEATURE [Part::Cylinder] Cylinder488  label="Válec488"
  Angle = 360
  AttacherType = Attacher::AttachEngine3D
  Height = 50
  Placement = pos=(63,49,-12) rot=(0,0,1;0rad)
  Radius = 1.5
FEATURE [Part::Box] Box200  label="Krychle200"
  AttacherType = Attacher::AttachEngine3D
  Height = 2
  Length = 16
  Placement = pos=(60,46,10) rot=(0,0,1;0rad)
  Width = 6
FEATURE [Part::Cylinder] Cylinder486  label="Válec486"
  Angle = 360
  AttacherType = Attacher::AttachEngine3D
  Height = 50
  Placement = pos=(63,33,-12) rot=(0,0,1;0rad)
  Radius = 1.5
FEATURE [Part::Cylinder] Cylinder480  label="Válec480"
  Angle = 360
  AttacherType = Attacher::AttachEngine3D
  Height = 50
  Placement = pos=(63,-18,-12) rot=(0,0,1;0rad)
  Radius = 1.5
FEATURE [Part::Cylinder] Cylinder481  label="Válec481"
  Angle = 360
  AttacherType = Attacher::AttachEngine3D
  Height = 100
  Placement = pos=(24,51,7) rot=(0,1,0;1.5708rad)
  Radius = 5
FEATURE [Part::Cylinder] Cylinder475  label="Válec475"
  Angle = 360
  AttacherType = Attacher::AttachEngine3D
  Height = 100
  Placement = pos=(24,36,34) rot=(0,1,0;1.5708rad)
  Radius = 5
FEATURE [Part::Cylinder] Cylinder478  label="Válec478"
  Angle = 360
  AttacherType = Attacher::AttachEngine3D
  Height = 100
  Placement = pos=(24,23,-5) rot=(0,1,0;1.5708rad)
  Radius = 5
FEATURE [Part::Cylinder] Cylinder483  label="Válec483"
  Angle = 360
  AttacherType = Attacher::AttachEngine3D
  Height = 50
  Placement = pos=(63,-48,-12) rot=(0,0,1;0rad)
  Radius = 1.5
FEATURE [Part::Cylinder] Cylinder476  label="Válec476"
  Angle = 360
  AttacherType = Attacher::AttachEngine3D
  Height = 100
  Placement = pos=(24,-51,25) rot=(0,1,0;1.5708rad)
  Radius = 5
FEATURE [Part::Cylinder] Cylinder479  label="Válec479"
  Angle = 360
  AttacherType = Attacher::AttachEngine3D
  Height = 100
  Placement = pos=(24,-51,7) rot=(0,1,0;1.5708rad)
  Radius = 5
FEATURE [Part::Cylinder] Cylinder477  label="Válec477"
  Angle = 360
  AttacherType = Attacher::AttachEngine3D
  Height = 100
  Placement = pos=(24,-23,-5) rot=(0,1,0;1.5708rad)
  Radius = 5
FEATURE [Part::Compound] Compound596
  Links = -> [Cylinder474,Cylinder476,Cylinder475,Cylinder461,Cylinder477,Cylinder481,Cylinder478,Cylinder479]
  Placement = pos=(24,-6,0) rot=(0,0,1;0rad)
FEATURE [Part::Cut] Cut590
  Base = -> Box201
  Tool = -> Compound596
FEATURE [Part::Box] Box208  label="Krychle208"
  AttacherType = Attacher::AttachEngine3D
  Height = 2
  Length = 16
  Placement = pos=(60,-21,10) rot=(0,0,1;0rad)
  Width = 6
FEATURE [Part::Cylinder] Cylinder482  label="Válec482"
  Angle = 360
  AttacherType = Attacher::AttachEngine3D
  Height = 50
  Placement = pos=(63,5,-12) rot=(0,0,1;0rad)
  Radius = 1.5
FEATURE [Part::Compound] Compound593
  Links = -> [Cylinder482,Cylinder480,Cylinder467,Cylinder483,Cylinder486,Cylinder488]
  Placement = pos=(39,24,0) rot=(0,0,1;0rad)
FEATURE [Part::Cut] Cut589
  Base = -> Cut590
  Tool = -> Compound593
FEATURE [Part::Box] Box206  label="Krychle206"
  AttacherType = Attacher::AttachEngine3D
  Height = 2
  Length = 16
  Placement = pos=(60,-21,16) rot=(0,0,1;0rad)
  Width = 6
FEATURE [Part::Box] Box203  label="Krychle203"
  AttacherType = Attacher::AttachEngine3D
  Height = 2
  Length = 16
  Placement = pos=(60,2,10) rot=(0,0,1;0rad)
  Width = 6
FEATURE [Part::Box] Box207  label="Krychle207"
  AttacherType = Attacher::AttachEngine3D
  Height = 2
  Length = 16
  Placement = pos=(60,30,10) rot=(0,0,1;0rad)
  Width = 6
FEATURE [Part::Box] Box212  label="Krychle212"
  AttacherType = Attacher::AttachEngine3D
  Height = 2
  Length = 16
  Placement = pos=(60,30,16) rot=(0,0,1;0rad)
  Width = 6
FEATURE [Part::Compound] Compound592
  Links = -> [Box203,Box202,Box208,Box206,Box204,Box198,Box209,Box205,Box207,Box200,Box212,Box211]
  Placement = pos=(39,24,3) rot=(0,0,1;0rad)
FEATURE [Part::Cut] Cut591  label="supershift"
  Base = -> Cut589
  Placement = pos=(-17,-60,-56) rot=(0.57735,0.57735,0.57735;2.0944rad)
  Tool = -> Compound592
FEATURE [Mesh::Feature] Mesh008  label="G-midi_rotator-fix (Meshed)002"
FEATURE [Mesh::Feature] Mesh009  label="G-midi_bearing-ring-centric (Meshed)"
FEATURE [Part::Cylinder] Cylinder1919  label="Válec1919"
  Angle = 360
  AttacherType = Attacher::AttachEngine3D
  Height = 20
  Placement = pos=(-18.0312,-18.0312,-4) rot=(0,0,1;2.35619rad)
  Radius = 1.5
FEATURE [Part::Cylinder] Cylinder1840  label="Válec1840"
  Angle = 360
  AttacherType = Attacher::AttachEngine3D
  Height = 20
  Placement = pos=(18.0312,-18.0312,-4) rot=(0,0,1;3.92699rad)
  Radius = 1.5
FEATURE [Part::Cylinder] Cylinder1843  label="Válec1843"
  Angle = 360
  AttacherType = Attacher::AttachEngine3D
  Height = 20
  Placement = pos=(-25.5,-1e-15,-4) rot=(0,0,1;1.5708rad)
  Radius = 1.5
FEATURE [Part::Cylinder] Cylinder1844  label="Válec1844"
  Angle = 360
  AttacherType = Attacher::AttachEngine3D
  Height = 20
  Placement = pos=(25.5,1e-14,-4) rot=(0,0,-1;1.5708rad)
  Radius = 1.5
FEATURE [Part::Cylinder] Cylinder1923  label="Válec1923"
  Angle = 360
  AttacherType = Attacher::AttachEngine3D
  Height = 20
  Placement = pos=(18.0312,18.0312,-4) rot=(0,0,-1;0.785398rad)
  Radius = 1.5
FEATURE [Part::Cylinder] Cylinder1847  label="Válec1847"
  Angle = 360
  AttacherType = Attacher::AttachEngine3D
  Height = 20
  Placement = pos=(0,25.5,-4) rot=(0,0,1;0rad)
  Radius = 1.5
FEATURE [Part::Cylinder] Cylinder1846  label="Válec1846"
  Angle = 360
  AttacherType = Attacher::AttachEngine3D
  Height = 20
  Placement = pos=(-18.0312,-18.0312,-4) rot=(0,0,1;2.35619rad)
  Radius = 1.5
FEATURE [Part::Cylinder] Cylinder1920  label="Válec1920"
  Angle = 360
  AttacherType = Attacher::AttachEngine3D
  Height = 20
  Placement = pos=(4e-15,-25.5,-4) rot=(0,0,1;3.14159rad)
  Radius = 1.5
FEATURE [Part::Cylinder] Cylinder1842  label="Válec1842"
  Angle = 360
  AttacherType = Attacher::AttachEngine3D
  Height = 20
  Placement = pos=(18.0312,18.0312,-4) rot=(0,0,-1;0.785398rad)
  Radius = 1.5
FEATURE [Part::Cylinder] Cylinder1921  label="Válec1921"
  Angle = 360
  AttacherType = Attacher::AttachEngine3D
  Height = 20
  Placement = pos=(-18.0312,18.0312,-4) rot=(0,0,1;0.785398rad)
  Radius = 1.5
FEATURE [Part::Cylinder] Cylinder1922  label="Válec1922"
  Angle = 360
  AttacherType = Attacher::AttachEngine3D
  Height = 20
  Placement = pos=(18.0312,-18.0312,-4) rot=(0,0,1;3.92699rad)
  Radius = 1.5
FEATURE [Part::Cylinder] Cylinder1845  label="Válec1845"
  Angle = 360
  AttacherType = Attacher::AttachEngine3D
  Height = 20
  Placement = pos=(-18.0312,18.0312,-4) rot=(0,0,1;0.785398rad)
  Radius = 1.5
FEATURE [Part::Cylinder] Cylinder1841  label="Válec1841"
  Angle = 360
  AttacherType = Attacher::AttachEngine3D
  Height = 20
  Placement = pos=(4e-15,-25.5,-4) rot=(0,0,1;3.14159rad)
  Radius = 1.5
FEATURE [Part::Compound] Compound911
  Links = -> [Cylinder1847,Cylinder1845,Cylinder1843,Cylinder1846,Cylinder1841,Cylinder1840,Cylinder1844,Cylinder1842]
FEATURE [Part::Cylinder] Cylinder1924  label="Válec1924"
  Angle = 360
  AttacherType = Attacher::AttachEngine3D
  Height = 20
  Placement = pos=(25.5,1e-14,-4) rot=(0,0,-1;1.5708rad)
  Radius = 1.5
FEATURE [Part::Cylinder] Cylinder1918  label="Válec1918"
  Angle = 360
  AttacherType = Attacher::AttachEngine3D
  Height = 2
  Placement = pos=(0,0,96) rot=(0,0,1;0rad)
  Radius = 34
FEATURE [Part::Cylinder] Cylinder1926  label="Válec1926"
  Angle = 360
  AttacherType = Attacher::AttachEngine3D
  Height = 20
  Placement = pos=(0,25.5,-4) rot=(0,0,1;0rad)
  Radius = 1.5
FEATURE [Part::Cylinder] Cylinder1925  label="Válec1925"
  Angle = 360
  AttacherType = Attacher::AttachEngine3D
  Height = 20
  Placement = pos=(-25.5,-1e-15,-4) rot=(0,0,1;1.5708rad)
  Radius = 1.5
FEATURE [Part::Compound] Compound917
  Links = -> [Cylinder1926,Cylinder1921,Cylinder1925,Cylinder1919,Cylinder1920,Cylinder1922,Cylinder1924,Cylinder1923]
  Placement = pos=(0,0,100) rot=(0,0,1;0rad)
FEATURE [Part::Cut] Cut564
  Base = -> Cylinder1918
  Placement = pos=(0,0,1) rot=(0,0,1;0rad)
  Tool = -> Compound917
FEATURE [Part::FeaturePython] Tube097  # WARN: FeaturePython — macro-defined, semantics opaque (R4)
  AttacherType = Attacher::AttachEngine3D
  Height = 1
  InnerRadius = 22.5
  OuterRadius = 28.5
  Placement = pos=(0,0,-2) rot=(0,0,1;0rad)
FEATURE [Part::FeaturePython] Tube100  # WARN: FeaturePython — macro-defined, semantics opaque (R4)
  AttacherType = Attacher::AttachEngine3D
  Height = 1
  InnerRadius = 12
  OuterRadius = 18
  Placement = pos=(0,0,96) rot=(0,0,1;0rad)
FEATURE [Part::FeaturePython] Tube099  # WARN: FeaturePython — macro-defined, semantics opaque (R4)
  AttacherType = Attacher::AttachEngine3D
  Height = 8
  InnerRadius = 14.1
  OuterRadius = 18
  Placement = pos=(0,0,88) rot=(0,0,1;0rad)
FEATURE [Part::Chamfer] Chamfer074
  Base = -> Tube099
  Edges = 1 edges r=1: [Edge5]
FEATURE [Part::FeaturePython] Tube096  # WARN: FeaturePython — macro-defined, semantics opaque (R4)
  AttacherType = Attacher::AttachEngine3D
  Height = 18
  InnerRadius = 22.5
  OuterRadius = 34
  Placement = pos=(0,0,-1) rot=(0,0,1;0rad)
FEATURE [Part::Compound] Compound912
  Links = -> [Tube097,Tube096]
  Placement = pos=(0,0,-1) rot=(0,0,1;0rad)
FEATURE [Part::Cut] Cut563  label="G-midi_super-washer1"
  Base = -> Compound912
  Placement = pos=(0,0,81) rot=(0,0,1;0rad)
  Tool = -> Compound911
FEATURE [Part::Compound] Compound923  label="G-midi_super-washer"
  Links = -> [Cut564,Chamfer074,Tube100,Cut563]
  Placement = pos=(0,0,-143) rot=(0,0,1;0rad)
FEATURE [Part::Box] Box759  label="Krychle759"
  AttacherType = Attacher::AttachEngine3D
  Height = 35
  Length = 20
  Placement = pos=(-10,20,19) rot=(0,0,1;0rad)
  Width = 27
FEATURE [Part::Box] Box760  label="Krychle760"
  AttacherType = Attacher::AttachEngine3D
  Height = 34
  Length = 20
  Placement = pos=(-10,20,19) rot=(0,0,1;0rad)
  Width = 25
FEATURE [Part::Box] Box763  label="Krychle763"
  AttacherType = Attacher::AttachEngine3D
  Height = 3
  Length = 10
  Placement = pos=(58,2,4) rot=(0,0,1;0rad)
  Width = 28
FEATURE [Part::Cylinder] Cylinder1969  label="Válec1969"
  Angle = 360
  AttacherType = Attacher::AttachEngine3D
  Height = 36
  Placement = pos=(0,0,19) rot=(0,0,1;0rad)
  Radius = 25
FEATURE [Part::Cylinder] Cylinder1971  label="Válec1971"
  Angle = 360
  AttacherType = Attacher::AttachEngine3D
  Height = 40
  Placement = pos=(-20,42,-50) rot=(0,1,0;1.5708rad)
  Radius = 1.5
FEATURE [Part::Box] Box758  label="Krychle758"
  AttacherType = Attacher::AttachEngine3D
  Height = 3
  Length = 10
  Placement = pos=(58,2,27) rot=(0,0,1;0rad)
  Width = 28
FEATURE [Part::Box] Box762  label="Krychle762"
  AttacherType = Attacher::AttachEngine3D
  Height = 34
  Length = 20
  Placement = pos=(-10,20,19) rot=(0,0,1;0rad)
  Width = 25
FEATURE [Part::Cylinder] Cylinder1970  label="Válec1970"
  Angle = 360
  AttacherType = Attacher::AttachEngine3D
  Height = 40
  Placement = pos=(-20,42,29) rot=(0,1,0;1.5708rad)
  Radius = 1.5
FEATURE [Part::Box] Box761  label="Krychle761"
  AttacherType = Attacher::AttachEngine3D
  Height = 33
  Length = 26
  Placement = pos=(-13,15,19) rot=(0,0,1;0rad)
  Width = 32
FEATURE [Part::Cylinder] Cylinder1968  label="Válec1968"
  Angle = 360
  AttacherType = Attacher::AttachEngine3D
  Height = 40
  Placement = pos=(-20,42,42) rot=(0,1,0;1.5708rad)
  Radius = 1.5
FEATURE [Part::FeaturePython] Tube103  # WARN: FeaturePython — macro-defined, semantics opaque (R4)
  AttacherType = Attacher::AttachEngine3D
  Height = 33
  InnerRadius = 25
  OuterRadius = 27
  Placement = pos=(0,0,19) rot=(0,0,1;0rad)
FEATURE [Part::FeaturePython] Tube102  # WARN: FeaturePython — macro-defined, semantics opaque (R4)
  AttacherType = Attacher::AttachEngine3D
  Height = 4
  InnerRadius = 25
  OuterRadius = 29
  Placement = pos=(0,0,29) rot=(0,0,1;0rad)
FEATURE [Part::Cut] Cut583
  Base = -> Tube103
  Tool = -> Box762
FEATURE [Part::Cut] Cut584
  Base = -> Box761
  Tool = -> Box759
FEATURE [Part::Cut] Cut588
  Base = -> Cut584
  Tool = -> Cylinder1969
FEATURE [Part::Cut] Cut587
  Base = -> Tube102
  Tool = -> Box760
FEATURE [Part::Compound] Compound933
  Links = -> [Box763,Box758]
  Placement = pos=(-17,-21,50) rot=(0.57735,0.57735,0.57735;2.0944rad)
FEATURE [Part::Compound] Compound934
  Links = -> [Cylinder1970,Cylinder1968]
FEATURE [Part::Cut] Cut585
  Base = -> Cut588
  Tool = -> Compound934
FEATURE [Part::Compound] Compound931
  Links = -> [Cut585,Cut583]
FEATURE [Part::Compound] Compound935  label="adapto_midi_kryto003"
  Links = -> [Compound931,Compound933]
  Placement = pos=(0,0,10) rot=(0,0,1;0rad)
FEATURE [Part::Compound] Compound932  label="adapto_midi_kryto002"
  Links = -> [Compound935,Cut587]
  Placement = pos=(0,0,25) rot=(0,1,0;3.14159rad)
FEATURE [Part::Cut] Cut586  label="G-midi_extrusion-cover-supershift"
  Base = -> Compound932
  Tool = -> Cylinder1971
FEATURE [Mesh::Feature] Mesh010  label="G-midi_super-washer (Meshed)"
FEATURE [Mesh::Feature] Mesh011  label="G-midi_extrusion-cover-supershift (Meshed)"
FEATURE [Part::Torus] Torus004  label="Anuloid004"
  Angle1 = -180
  Angle2 = 180
  Angle3 = 360
  AttacherType = Attacher::AttachEngine3D
  Placement = pos=(0,0,20.5) rot=(0,0,1;0rad)
  Radius1 = 28.15
  Radius2 = 2.2
FEATURE [Part::Cylinder] Cylinder1972  label="Válec1972"
  Angle = 360
  AttacherType = Attacher::AttachEngine3D
  Height = 10
  Placement = pos=(22.6274,22.6274,10) rot=(0,0,-1;0.785398rad)
  Radius = 1.5
FEATURE [Part::Cylinder] Cylinder1973  label="Válec1973"
  Angle = 360
  AttacherType = Attacher::AttachEngine3D
  Height = 20
  Placement = pos=(4,38,25) rot=(0,1,0;1.5708rad)
  Radius = 1.5
FEATURE [Part::Box] Box764  label="Krychle764"
  AttacherType = Attacher::AttachEngine3D
  Height = 20
  Length = 20.4
  Placement = pos=(-10.2,20,10) rot=(0,0,1;0rad)
  Width = 27
FEATURE [Part::Cylinder] Cylinder1974  label="Válec1974"
  Angle = 360
  AttacherType = Attacher::AttachEngine3D
  Height = 10
  Placement = pos=(22.6274,-22.6274,10) rot=(0,0,1;3.92699rad)
  Radius = 1.5
FEATURE [Part::Cylinder] Cylinder1975  label="Válec1975"
  Angle = 360
  AttacherType = Attacher::AttachEngine3D
  Height = 10
  Placement = pos=(1e-14,-32,10) rot=(0,0,1;3.14159rad)
  Radius = 1.5
FEATURE [Part::Box] Box765  label="Krychle765"
  AttacherType = Attacher::AttachEngine3D
  Height = 2
  Length = 6
  Placement = pos=(-22.6274,18.3848,14) rot=(0,0,1;0.785398rad)
  Width = 6
FEATURE [Part::Cylinder] Cylinder1976  label="Válec1976"
  Angle = 360
  AttacherType = Attacher::AttachEngine3D
  Height = 20
  Placement = pos=(18,38,25) rot=(0,1,0;1.5708rad)
  Radius = 4
FEATURE [Part::FeaturePython] Tube104  # WARN: FeaturePython — macro-defined, semantics opaque (R4)
  AttacherType = Attacher::AttachEngine3D
  Height = 20
  InnerRadius = 29
  OuterRadius = 35
  Placement = pos=(0,0,10) rot=(0,0,1;0rad)
FEATURE [Part::Cylinder] Cylinder1977  label="Válec1977"
  Angle = 360
  AttacherType = Attacher::AttachEngine3D
  Height = 10
  Placement = pos=(-22.6274,-22.6274,10) rot=(0,0,1;2.35619rad)
  Radius = 1.5
FEATURE [Part::Cylinder] Cylinder1978  label="Válec1978"
  Angle = 360
  AttacherType = Attacher::AttachEngine3D
  Height = 20
  Placement = pos=(-38,38,25) rot=(0,1,0;1.5708rad)
  Radius = 4
FEATURE [Part::Cylinder] Cylinder1979  label="Válec1979"
  Angle = 360
  AttacherType = Attacher::AttachEngine3D
  Height = 10
  Placement = pos=(0,32,10) rot=(0,0,1;0rad)
  Radius = 1.5
FEATURE [Part::Cylinder] Cylinder1980  label="Válec1980"
  Angle = 360
  AttacherType = Attacher::AttachEngine3D
  Height = 10
  Placement = pos=(28,0,20.5) rot=(0,0,1;0rad)
  Radius = 2.2
FEATURE [Part::Box] Box766  label="Krychle766"
  AttacherType = Attacher::AttachEngine3D
  Height = 20
  Length = 50
  Placement = pos=(-25,15,10) rot=(0,0,1;0rad)
  Width = 32
FEATURE [Part::Box] Box767  label="Krychle767"
  AttacherType = Attacher::AttachEngine3D
  Height = 2
  Length = 6
  Placement = pos=(22.6274,-18.3848,14) rot=(0,0,1;3.92699rad)
  Width = 6
FEATURE [Part::Box] Box768  label="Krychle768"
  AttacherType = Attacher::AttachEngine3D
  Height = 2
  Length = 6
  Placement = pos=(18.3848,22.6274,14) rot=(0,0,-1;0.785398rad)
  Width = 6
FEATURE [Part::Cylinder] Cylinder1981  label="Válec1981"
  Angle = 360
  AttacherType = Attacher::AttachEngine3D
  Height = 20
  Placement = pos=(-24,38,25) rot=(0,1,0;1.5708rad)
  Radius = 1.5
FEATURE [Part::Box] Box769  label="Krychle769"
  AttacherType = Attacher::AttachEngine3D
  Height = 2
  Length = 6
  Placement = pos=(3,-29,14) rot=(0,0,1;3.14159rad)
  Width = 6
FEATURE [Part::Cylinder] Cylinder1982  label="Válec1982"
  Angle = 360
  AttacherType = Attacher::AttachEngine3D
  Height = 10
  Placement = pos=(32,1.1e-14,10) rot=(0,0,-1;1.5708rad)
  Radius = 1.5
FEATURE [Part::Cylinder] Cylinder1983  label="Válec1983"
  Angle = 360
  AttacherType = Attacher::AttachEngine3D
  Height = 20
  Placement = pos=(0,0,10) rot=(0,0,1;0rad)
  Radius = 35
FEATURE [Part::Cut] Cut592
  Base = -> Box766
  Tool = -> Cylinder1983
FEATURE [Part::Box] Box770  label="Krychle770"
  AttacherType = Attacher::AttachEngine3D
  Height = 2
  Length = 6
  Placement = pos=(29,3,14) rot=(0,0,-1;1.5708rad)
  Width = 6
FEATURE [Part::Box] Box771  label="Krychle771"
  AttacherType = Attacher::AttachEngine3D
  Height = 2
  Length = 6
  Placement = pos=(-29,-3,14) rot=(0,0,1;1.5708rad)
  Width = 6
FEATURE [Part::Box] Box772  label="Krychle772"
  AttacherType = Attacher::AttachEngine3D
  Height = 2
  Length = 6
  Placement = pos=(-18.3848,-22.6274,14) rot=(0,0,1;2.35619rad)
  Width = 6
FEATURE [Part::Cylinder] Cylinder1984  label="Válec1984"
  Angle = 360
  AttacherType = Attacher::AttachEngine3D
  Height = 10
  Placement = pos=(-22.6274,22.6274,10) rot=(0,0,1;0.785398rad)
  Radius = 1.5
FEATURE [Part::Box] Box773  label="Krychle773"
  AttacherType = Attacher::AttachEngine3D
  Height = 2
  Length = 6
  Placement = pos=(-3,29,14) rot=(0,0,1;0rad)
  Width = 6
FEATURE [Part::Compound] Compound936
  Links = -> [Box765,Box771,Box772,Box769,Box767,Box770,Box768,Box773]
FEATURE [Part::Cylinder] Cylinder1985  label="Válec1985"
  Angle = 360
  AttacherType = Attacher::AttachEngine3D
  Height = 20
  Placement = pos=(4,38,15) rot=(0,1,0;1.5708rad)
  Radius = 1.5
FEATURE [Part::Cylinder] Cylinder1986  label="Válec1986"
  Angle = 360
  AttacherType = Attacher::AttachEngine3D
  Height = 20
  Placement = pos=(-38,38,15) rot=(0,1,0;1.5708rad)
  Radius = 4
FEATURE [Part::Cylinder] Cylinder1987  label="Válec1987"
  Angle = 360
  AttacherType = Attacher::AttachEngine3D
  Height = 20
  Placement = pos=(-24,38,15) rot=(0,1,0;1.5708rad)
  Radius = 1.5
FEATURE [Part::Compound] Compound940
  Links = -> [Cylinder1973,Cylinder1981,Cylinder1985,Cylinder1987]
  Placement = pos=(0,4,0) rot=(0,0,1;0rad)
FEATURE [Part::Cylinder] Cylinder1988  label="Válec1988"
  Angle = 360
  AttacherType = Attacher::AttachEngine3D
  Height = 20
  Placement = pos=(18,38,15) rot=(0,1,0;1.5708rad)
  Radius = 4
FEATURE [Part::Compound] Compound937
  Links = -> [Cylinder1976,Cylinder1978,Cylinder1988,Cylinder1986]
  Placement = pos=(0,4,0) rot=(0,0,1;0rad)
FEATURE [Part::Cylinder] Cylinder1989  label="Válec1989"
  Angle = 360
  AttacherType = Attacher::AttachEngine3D
  Height = 10
  Placement = pos=(-32,0,10) rot=(0,0,1;1.5708rad)
  Radius = 1.5
FEATURE [Part::Compound] Compound938
  Links = -> [Cylinder1984,Cylinder1989,Cylinder1977,Cylinder1975,Cylinder1974,Cylinder1982,Cylinder1972,Cylinder1979]
  Placement = pos=(0,0,-2) rot=(0,0,1;0rad)
FEATURE [Part::Cut] Cut595
  Base = -> Cut592
  Tool = -> Box764
FEATURE [Part::Cut] Cut596
  Base = -> Cut595
  Tool = -> Compound937
FEATURE [Part::Cut] Cut594
  Base = -> Cut596
  Tool = -> Compound940
FEATURE [Part::Cut] Cut598
  Base = -> Tube104
  Tool = -> Torus004
FEATURE [Part::Cut] Cut599
  Base = -> Cut598
  Tool = -> Cylinder1980
FEATURE [Part::Cut] Cut597
  Base = -> Cut599
  Tool = -> Compound938
FEATURE [Part::Cut] Cut593  label="gearovina-midi_loziskovina003"
  Base = -> Cut597
  Tool = -> Compound936
FEATURE [Part::Compound] Compound939  label="G-midi_bearing-ring-centric-lax"
  Links = -> [Cut594,Cut593]
  Placement = pos=(0,0,-95) rot=(0,1,0;0rad)
FEATURE [Mesh::Feature] Mesh012  label="G-midi_bearing-ring-centric-lax (Meshed)"
FEATURE [Mesh::Feature] Mesh013  label="G-midi_belt-wheel-front (Meshed)"
FEATURE [Mesh::Feature] Mesh014  label="G-midi_bear-fix (Meshed)001"
FEATURE [Mesh::Feature] Mesh015  label="G-midi_bear-hold-encoder-front (Meshed)"
FEATURE [Mesh::Feature] Mesh016  label="G-midi_rotator-fix (Meshed)003"
FEATURE [Mesh::Feature] Mesh017  label="G-midi_bear-hold-encoder-rear (Meshed)001"
FEATURE [Mesh::Feature] Mesh018  label="G-midi_bearing-ring (Meshed)"
FEATURE [Mesh::Feature] Mesh019  label="G-midi_belt-wheel-rear (Meshed)001"
FEATURE [Mesh::Feature] Mesh020  label="G-midi_monoblock-cyclo (Meshed)"
FEATURE [Mesh::Feature] Mesh021  label="G-midi_quikovina (Meshed)"
FEATURE [Mesh::Feature] Mesh022  label="G-midi_arm-rotator (Meshed)"
FEATURE [Mesh::Feature] Mesh023  label="G-midi_extrusion-cover-subshift (Meshed)"
FEATURE [Mesh::Feature] Mesh024  label="G-midi_bearing-ring-centric (Meshed)001"
FEATURE [Mesh::Feature] Mesh025  label="G-midi_super-washer (Meshed)001"
FEATURE [Mesh::Feature] Mesh026  label="G-midi_extrusion-cover-supershift (Meshed)001"
FEATURE [Mesh::Feature] Mesh027  label="G-midi_bearing-ring-centric-lax (Meshed)001"
